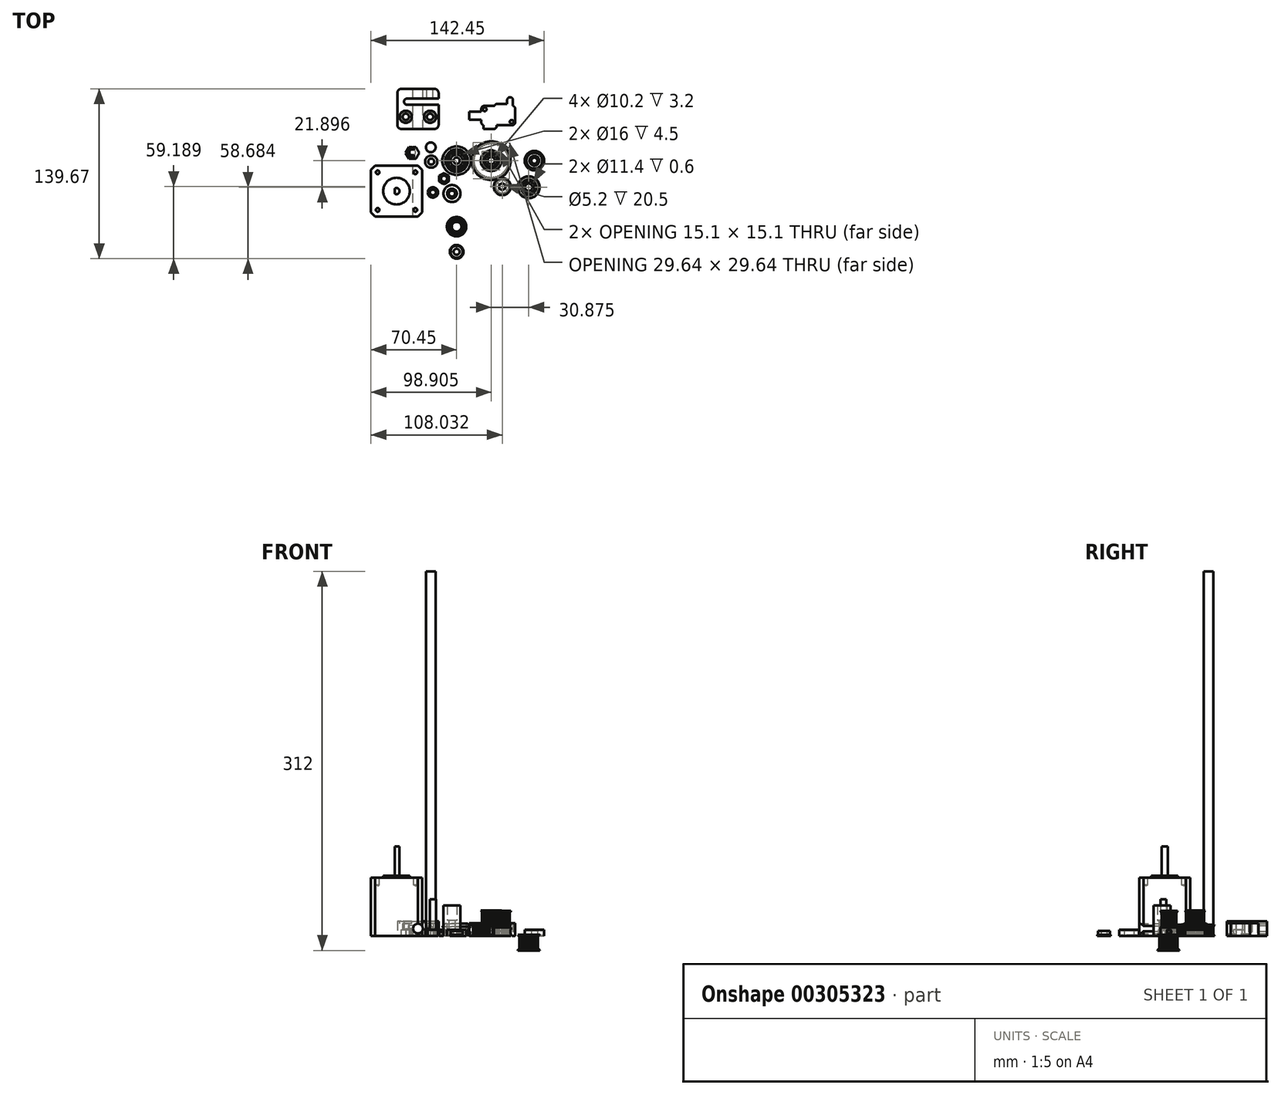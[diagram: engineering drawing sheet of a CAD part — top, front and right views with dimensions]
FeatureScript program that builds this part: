
annotation { "Feature Type Name" : "Feature", "Feature Type Description" : "" }
export const myFeature = defineFeature(function(context is Context, id is Id, definition is map)
    precondition{}
    {
        {
            var Q0;
            Q0=qCreatedBy(makeId("Front.planeOp"),FACE);
            var sketch = newSketch(context, id + "F0", { "sketchPlane" : qUnion([Q0])});
            skLineSegment(sketch, "E0", {"start": v(0, 0) * mm, "end": v(0, 10) * mm, "construction": true});
            skLineSegment(sketch, "E1", {"start": v(-9.25, 0) * mm, "end": v(-8, 0) * mm});
            skLineSegment(sketch, "E2", {"start": v(-8, 0) * mm, "end": v(-8, 10) * mm, "construction": true});
            skLineSegment(sketch, "E3", {"start": v(-8, 10) * mm, "end": v(-9.25, 10) * mm});
            skLineSegment(sketch, "E4", {"start": v(-8, 5) * mm, "end": v(-9.25, 5) * mm, "construction": true});
            skLineSegment(sketch, "E5", {"start": v(-9.25, 10) * mm, "end": v(-11.75, 7.5) * mm});
            skLineSegment(sketch, "E6", {"start": v(-11.75, 7.5) * mm, "end": v(-9.25, 5) * mm});
            skLineSegment(sketch, "E7", {"start": v(-9.25, 5) * mm, "end": v(-11.75, 2.5) * mm});
            skLineSegment(sketch, "E8", {"start": v(-11.75, 2.5) * mm, "end": v(-9.25, 0) * mm});
            skLineSegment(sketch, "E9.bottom", {"start": v(-8, 5.5) * mm, "end": v(-7, 5.5) * mm});
            skLineSegment(sketch, "E9.top", {"start": v(-8, 4.5) * mm, "end": v(-7, 4.5) * mm});
            skLineSegment(sketch, "E9.left", {"start": v(-8, 5.5) * mm, "end": v(-8, 4.5) * mm, "construction": true});
            skLineSegment(sketch, "E9.right", {"start": v(-7, 5.5) * mm, "end": v(-7, 4.5) * mm});
            skLineSegment(sketch, "E10", {"start": v(-8, 5.5) * mm, "end": v(-8, 10) * mm});
            skLineSegment(sketch, "E11", {"start": v(-8, 4.5) * mm, "end": v(-8, 0) * mm});
            skSolve(sketch);
        }
        {
            var Q0;
            Q0 = qSketchRegion(id + "F0", true);
            var Q1;
            Q1=sQuery(id+"F0.wireOp",EDGE,"E0");
            revolve(context, id + "F1", {"entities" : qUnion([Q0]), "axis" : qUnion([Q1]), "revolveType" : RevolveType.FULL});
        }
        {
            var Q0;
            Q0=qCreatedBy(makeId("Top.planeOp"),FACE);
            var sketch = newSketch(context, id + "F2", { "sketchPlane" : qUnion([Q0])});
            skCircle(sketch, "E12.cCircle", {"center": v(-36.35, 6.37) * mm, "radius": 4.9 * mm, "construction": true});
            skLineSegment(sketch, "E12.0", {"start": v(-33.52, 1.47) * mm, "end": v(-39.18, 1.47) * mm});
            skLineSegment(sketch, "E12.1", {"start": v(-39.18, 1.47) * mm, "end": v(-42.01, 6.37) * mm});
            skLineSegment(sketch, "E12.2", {"start": v(-42.01, 6.37) * mm, "end": v(-39.18, 11.27) * mm});
            skLineSegment(sketch, "E12.3", {"start": v(-39.18, 11.27) * mm, "end": v(-33.52, 11.27) * mm});
            skLineSegment(sketch, "E12.4", {"start": v(-33.52, 11.27) * mm, "end": v(-30.7, 6.37) * mm});
            skLineSegment(sketch, "E12.5", {"start": v(-30.7, 6.37) * mm, "end": v(-33.52, 1.47) * mm});
            skPoint(sketch, "E12.0.midPoint", {"position": v(-36.35, 1.47) * mm});
            skSolve(sketch);
        }
        {
            var Q0;
            Q0 = qSketchRegion(id + "F2", true);
            extrude(context, id + "F3", {"entities" : qUnion([Q0]), "depth" : 6 * mm});
        }
        {
            var Q0;
            Q0=makeQuery(id+"F3.opExtrude","CAP_FACE",FACE,{"disambiguationData":[OSD([sQuery(id+"F2.wireOp",EDGE,"E12.0"),sQuery(id+"F2.wireOp",EDGE,"E12.1"),sQuery(id+"F2.wireOp",EDGE,"E12.2"),sQuery(id+"F2.wireOp",EDGE,"E12.3"),sQuery(id+"F2.wireOp",EDGE,"E12.4"),sQuery(id+"F2.wireOp",EDGE,"E12.5")])],"isStart":false});
            var sketch = newSketch(context, id + "F4", { "sketchPlane" : qUnion([Q0])});
            skCircle(sketch, "E13", {"center": v(-36.35, 6.37) * mm, "radius": 3.5 * mm});
            skPoint(sketch, "E13.centerSnap0", {"position": v(-36.35, 11.27) * mm});
            skSolve(sketch);
        }
        {
            var Q0;
            Q0 = qSketchRegion(id + "F4", true);
            extrude(context, id + "F5", {"entities" : qUnion([Q0]), "operationType" : NewBodyOperationType.ADD, "depth" : 2.5 * mm});
        }
        {
            var Q0;
            Q0=makeQuery(id+"F5.opExtrude","CAP_FACE",FACE,{"disambiguationData":[OSD([sQuery(id+"F4.wireOp",EDGE,"E13")])],"isStart":false});
            var sketch = newSketch(context, id + "F6", { "sketchPlane" : qUnion([Q0])});
            skCircle(sketch, "E14", {"center": v(-36.35, 6.87) * mm, "radius": 2.5 * mm});
            skLineSegment(sketch, "E15", {"start": v(-37.24, 11.9) * mm, "end": v(-36.35, 10.37) * mm});
            skLineSegment(sketch, "E16", {"start": v(-36.35, 10.37) * mm, "end": v(-35.47, 11.9) * mm});
            skLineSegment(sketch, "E17", {"start": v(-35.47, 11.9) * mm, "end": v(-37.24, 11.9) * mm});
            skLineSegment(sketch, "E18", {"start": v(-36.35, 1.47) * mm, "end": v(-36.35, 6.87) * mm, "construction": true});
            skLineSegment(sketch, "E19", {"start": v(-36.35, 11.9) * mm, "end": v(-36.35, 10.37) * mm, "construction": true});
            skSolve(sketch);
        }
        {
            var Q0;
            Q0 = qSketchRegion(id + "F6", true);
            extrude(context, id + "F7", {"entities" : qUnion([Q0]), "operationType" : NewBodyOperationType.REMOVE, "endBound" : BoundingType.THROUGH_ALL, "oppositeDirection" : true, "depth" : 25 * mm});
        }
        {
            var Q0;
            Q0=makeQuery(id+"F7.boolean.opBoolean","COPY",EDGE,{"derivedFrom":makeQuery(id+"F7.opExtrude","SWEPT_EDGE",EDGE,{"disambiguationData":[OSD([sQuery(id+"F6.wireOp",EDGE,"E15"),sQuery(id+"F6.wireOp",EDGE,"E16")])]})});
            fillet(context, id + "F8", {"entities" : qUnion([Q0]), "radius" : 0.5 * mm, "tangentPropagation" : true, "allowEdgeOverflow" : false});
        }
        {
            var Q0;
            Q0=qCreatedBy(makeId("Top.planeOp"),FACE);
            var sketch = newSketch(context, id + "F9", { "sketchPlane" : qUnion([Q0])});
            skCircle(sketch, "E20", {"center": v(-20.9, -0.8) * mm, "radius": 5 * mm});
            skCircle(sketch, "E21", {"center": v(-20.9, -0.8) * mm, "radius": 2.5 * mm});
            skSolve(sketch);
        }
        {
            var Q0;
            Q0 = qSketchRegion(id + "F9", true);
            extrude(context, id + "F10", {"entities" : qUnion([Q0]), "depth" : 6 * mm});
        }
        {
            var Q0;
            Q0=qCreatedBy(makeId("Top.planeOp"),FACE);
            var sketch = newSketch(context, id + "F11", { "sketchPlane" : qUnion([Q0])});
            skLineSegment(sketch, "E22.bottom", {"start": v(-28.45, -4.05) * mm, "end": v(-70.45, -4.05) * mm});
            skLineSegment(sketch, "E22.top", {"start": v(-28.45, -46.05) * mm, "end": v(-70.45, -46.05) * mm});
            skLineSegment(sketch, "E22.left", {"start": v(-28.45, -4.05) * mm, "end": v(-28.45, -46.05) * mm});
            skLineSegment(sketch, "E22.right", {"start": v(-70.45, -4.05) * mm, "end": v(-70.45, -46.05) * mm});
            skSolve(sketch);
        }
        {
            var Q0;
            Q0 = qSketchRegion(id + "F11", true);
            extrude(context, id + "F12", {"entities" : qUnion([Q0]), "depth" : 48 * mm});
        }
        {
            var Q0;
            Q0=makeQuery(id+"F12.opExtrude","CAP_FACE",FACE,{"disambiguationData":[OSD([sQuery(id+"F11.wireOp",EDGE,"E22.bottom"),sQuery(id+"F11.wireOp",EDGE,"E22.top"),sQuery(id+"F11.wireOp",EDGE,"E22.left"),sQuery(id+"F11.wireOp",EDGE,"E22.right")])],"isStart":false});
            var sketch = newSketch(context, id + "F13", { "sketchPlane" : qUnion([Q0])});
            skCircle(sketch, "E23", {"center": v(-49.45, -25.05) * mm, "radius": 11 * mm});
            skPoint(sketch, "E23.centerSnap0", {"position": v(-49.45, -46.05) * mm});
            skLineSegment(sketch, "E24", {"start": v(-49.45, -4.05) * mm, "end": v(-49.45, -25.05) * mm, "construction": true});
            skLineSegment(sketch, "E25", {"start": v(-49.45, -25.05) * mm, "end": v(-28.45, -25.05) * mm, "construction": true});
            skSolve(sketch);
        }
        {
            var Q0;
            Q0 = qSketchRegion(id + "F13", true);
            extrude(context, id + "F14", {"entities" : qUnion([Q0]), "operationType" : NewBodyOperationType.ADD, "depth" : 1.5 * mm});
        }
        {
            var Q0;
            Q0=makeQuery(id+"F14.opExtrude","CAP_FACE",FACE,{"disambiguationData":[OSD([sQuery(id+"F13.wireOp",EDGE,"E23")])],"isStart":false});
            var sketch = newSketch(context, id + "F15", { "sketchPlane" : qUnion([Q0])});
            skArc(sketch, "E26", {"start": v(-50.95, -27.05) * mm, "mid": v(-46.95, -25.05) * mm, "end": v(-50.95, -23.05) * mm});
            skLineSegment(sketch, "E27", {"start": v(-50.95, -23.05) * mm, "end": v(-50.95, -27.05) * mm});
            skSolve(sketch);
        }
        {
            var Q0;
            Q0 = qSketchRegion(id + "F15", true);
            extrude(context, id + "F16", {"entities" : qUnion([Q0]), "operationType" : NewBodyOperationType.ADD, "depth" : 24 * mm});
        }
        {
            var Q0;
            Q0=makeQuery(id+"F12.opExtrude","SWEPT_EDGE",EDGE,{"disambiguationData":[OSD([sQuery(id+"F11.wireOp",EDGE,"E22.bottom"),sQuery(id+"F11.wireOp",EDGE,"E22.right")])]});
            var Q1;
            Q1=makeQuery(id+"F12.opExtrude","SWEPT_EDGE",EDGE,{"disambiguationData":[OSD([sQuery(id+"F11.wireOp",EDGE,"E22.top"),sQuery(id+"F11.wireOp",EDGE,"E22.right")])]});
            var Q2;
            Q2=makeQuery(id+"F12.opExtrude","SWEPT_EDGE",EDGE,{"disambiguationData":[OSD([sQuery(id+"F11.wireOp",EDGE,"E22.top"),sQuery(id+"F11.wireOp",EDGE,"E22.left")])]});
            var Q3;
            Q3=makeQuery(id+"F12.opExtrude","SWEPT_EDGE",EDGE,{"disambiguationData":[OSD([sQuery(id+"F11.wireOp",EDGE,"E22.bottom"),sQuery(id+"F11.wireOp",EDGE,"E22.left")])]});
            chamfer(context, id + "F17", {"entities" : qUnion([Q0, Q1, Q2, Q3]), "width" : 3.5 * mm, "tangentPropagation" : true});
        }
        {
            var Q0;
            Q0=makeQuery(id+"F12.opExtrude","CAP_FACE",FACE,{"disambiguationData":[OSD([sQuery(id+"F11.wireOp",EDGE,"E22.bottom"),sQuery(id+"F11.wireOp",EDGE,"E22.top"),sQuery(id+"F11.wireOp",EDGE,"E22.left"),sQuery(id+"F11.wireOp",EDGE,"E22.right")])],"isStart":false});
            var sketch = newSketch(context, id + "F18", { "sketchPlane" : qUnion([Q0])});
            skPoint(sketch, "E28", {"position": v(-64.95, -9.55) * mm});
            skPoint(sketch, "E29", {"position": v(-33.95, -9.55) * mm});
            skPoint(sketch, "E30", {"position": v(-33.95, -40.55) * mm});
            skPoint(sketch, "E31", {"position": v(-64.95, -40.55) * mm});
            skSolve(sketch);
        }
        {
            var Q0;
            Q0=sQuery(id+"F18.wireOp",VERTEX,"E28");
            var Q1;
            Q1=sQuery(id+"F18.wireOp",VERTEX,"E29");
            var Q2;
            Q2=sQuery(id+"F18.wireOp",VERTEX,"E30");
            var Q3;
            Q3=sQuery(id+"F18.wireOp",VERTEX,"E31");
            var Q4;
            Q4=makeQuery(id+"F12.opExtrude","SWEPT_BODY",BODY,{"disambiguationData":[OSD([sQuery(id+"F11.wireOp",EDGE,"E22.bottom"),sQuery(id+"F11.wireOp",EDGE,"E22.top"),sQuery(id+"F11.wireOp",EDGE,"E22.left"),sQuery(id+"F11.wireOp",EDGE,"E22.right")])]});
            hole(context, id + "F19", {"style" : HoleStyle.SIMPLE, "endStyle" : HoleEndStyle.BLIND, "holeDiameter" : 3 * mm, "holeDepth" : 6 * mm, "tappedDepth" : 12 * mm, "tapClearance" : 3, "startFromSketch" : true, "locations" : qUnion([Q0, Q1, Q2, Q3]), "scope" : qUnion([Q4])});
        }
        {
            var Q0;
            Q0=qCreatedBy(makeId("Top.planeOp"),FACE);
            var sketch = newSketch(context, id + "F20", { "sketchPlane" : qUnion([Q0])});
            skCircle(sketch, "E32", {"center": v(-3.83, -27.08) * mm, "radius": 2.5 * mm});
            skCircle(sketch, "E33", {"center": v(-3.83, -27.08) * mm, "radius": 7 * mm});
            skSolve(sketch);
        }
        {
            var Q0;
            Q0 = qSketchRegion(id + "F20", true);
            extrude(context, id + "F21", {"entities" : qUnion([Q0]), "depth" : 12.5 * mm});
        }
        {
            var Q0;
            Q0=makeQuery(id+"F21.opExtrude","CAP_FACE",FACE,{"disambiguationData":[OSD([sQuery(id+"F20.wireOp",EDGE,"E32"),sQuery(id+"F20.wireOp",EDGE,"E33")])],"isStart":false});
            var sketch = newSketch(context, id + "F22", { "sketchPlane" : qUnion([Q0])});
            skCircle(sketch, "E34", {"center": v(-3.83, -27.08) * mm, "radius": 4 * mm});
            skCircle(sketch, "E35.0", {"center": v(-3.83, -27.08) * mm, "radius": 7 * mm});
            skSolve(sketch);
        }
        {
            var Q0;
            Q0 = qSketchRegion(id + "F22", true);
            extrude(context, id + "F23", {"entities" : qUnion([Q0]), "operationType" : NewBodyOperationType.ADD, "depth" : 12.5 * mm});
        }
        {
            var Q0;
            Q0=qCreatedBy(makeId("Top.planeOp"),FACE);
            var sketch = newSketch(context, id + "F24", { "sketchPlane" : qUnion([Q0])});
            skCircle(sketch, "E36", {"center": v(-21.25, 10.98) * mm, "radius": 4 * mm});
            skSolve(sketch);
        }
        {
            var Q0;
            Q0 = qSketchRegion(id + "F24", true);
            extrude(context, id + "F25", {"entities" : qUnion([Q0]), "depth" : 300 * mm});
        }
        {
            var Q0;
            Q0=qCreatedBy(makeId("Top.planeOp"),FACE);
            var sketch = newSketch(context, id + "F26", { "sketchPlane" : qUnion([Q0])});
            skCircle(sketch, "E37", {"center": v(37.58, -21.4) * mm, "radius": 2.6 * mm});
            skCircle(sketch, "E38", {"center": v(37.58, -21.4) * mm, "radius": 7 * mm});
            skLineSegment(sketch, "E39.bottom", {"start": v(32.18, -18.5) * mm, "end": v(34.48, -18.5) * mm});
            skLineSegment(sketch, "E39.top", {"start": v(32.18, -24.3) * mm, "end": v(34.48, -24.3) * mm});
            skLineSegment(sketch, "E39.left", {"start": v(32.18, -18.5) * mm, "end": v(32.18, -24.3) * mm});
            skLineSegment(sketch, "E39.right", {"start": v(34.48, -18.5) * mm, "end": v(34.48, -24.3) * mm});
            skLineSegment(sketch, "E40", {"start": v(32.18, -21.4) * mm, "end": v(37.58, -21.4) * mm, "construction": true});
            skLineSegment(sketch, "E41", {"start": v(37.58, -21.4) * mm, "end": v(37.58, -14.4) * mm, "construction": true});
            skLineSegment(sketch, "E42.MirrorCS", {"start": v(40.68, -18.5) * mm, "end": v(40.68, -24.3) * mm});
            skLineSegment(sketch, "E43.MirrorCS", {"start": v(42.98, -18.5) * mm, "end": v(40.68, -18.5) * mm});
            skLineSegment(sketch, "E44.MirrorCS", {"start": v(42.98, -18.5) * mm, "end": v(42.98, -24.3) * mm});
            skLineSegment(sketch, "E45.MirrorCS", {"start": v(42.98, -24.3) * mm, "end": v(40.68, -24.3) * mm});
            skSolve(sketch);
        }
        {
            var Q0;
            Q0 = qSketchRegion(id + "F26", true);
            extrude(context, id + "F27", {"entities" : qUnion([Q0]), "depth" : 7 * mm});
        }
        {
            var Q0;
            Q0=makeQuery(id+"F27.opExtrude","CAP_FACE",FACE,{"disambiguationData":[OSD([sQuery(id+"F26.wireOp",EDGE,"E37"),sQuery(id+"F26.wireOp",EDGE,"E38"),sQuery(id+"F26.wireOp",EDGE,"E39.bottom"),sQuery(id+"F26.wireOp",EDGE,"E39.top"),sQuery(id+"F26.wireOp",EDGE,"E39.left"),sQuery(id+"F26.wireOp",EDGE,"E39.right"),sQuery(id+"F26.wireOp",EDGE,"E42.MirrorCS"),sQuery(id+"F26.wireOp",EDGE,"E43.MirrorCS"),sQuery(id+"F26.wireOp",EDGE,"E44.MirrorCS"),sQuery(id+"F26.wireOp",EDGE,"E45.MirrorCS")])],"isStart":false});
            var sketch = newSketch(context, id + "F28", { "sketchPlane" : qUnion([Q0])});
            skCircle(sketch, "E46.0", {"center": v(37.58, -21.4) * mm, "radius": 2.6 * mm});
            skCircle(sketch, "E47.0", {"center": v(37.58, -21.4) * mm, "radius": 7 * mm});
            skSolve(sketch);
        }
        {
            var Q0;
            Q0 = qSketchRegion(id + "F28", true);
            extrude(context, id + "F29", {"entities" : qUnion([Q0]), "operationType" : NewBodyOperationType.ADD, "depth" : 1 * mm});
        }
        {
            var Q0;
            Q0=makeQuery(id+"F29.opExtrude","CAP_FACE",FACE,{"disambiguationData":[OSD([sQuery(id+"F28.wireOp",EDGE,"E46.0"),sQuery(id+"F28.wireOp",EDGE,"E47.0")])],"isStart":false});
            var sketch = newSketch(context, id + "F30", { "sketchPlane" : qUnion([Q0])});
            skCircle(sketch, "E48.0", {"center": v(37.58, -21.4) * mm, "radius": 2.6 * mm});
            skCircle(sketch, "E49", {"center": v(37.58, -21.4) * mm, "radius": 6.1 * mm, "construction": true});
            skCircle(sketch, "E50.0", {"center": v(37.58, -21.4) * mm, "radius": 5.2 * mm, "construction": true});
            skLineSegment(sketch, "E51", {"start": v(37.58, -21.4) * mm, "end": v(37.58, -15.3) * mm, "construction": true});
            skLineSegment(sketch, "E52", {"start": v(36.98, -16.23) * mm, "end": v(38.18, -16.23) * mm});
            skLineSegment(sketch, "E53", {"start": v(36.98, -16.23) * mm, "end": v(36.67, -15.36) * mm});
            skLineSegment(sketch, "E54.MirrorCS", {"start": v(38.18, -16.23) * mm, "end": v(38.5, -15.36) * mm});
            skLineSegment(sketch, "E55.1.0", {"start": v(35.05, -16.85) * mm, "end": v(34.43, -16.17) * mm});
            skLineSegment(sketch, "E55.1.1", {"start": v(35.05, -16.85) * mm, "end": v(36.16, -16.39) * mm});
            skLineSegment(sketch, "E55.1.2", {"start": v(36.16, -16.39) * mm, "end": v(36.12, -15.47) * mm});
            skLineSegment(sketch, "E55.2.0", {"start": v(33.5, -18.16) * mm, "end": v(32.67, -17.77) * mm});
            skLineSegment(sketch, "E55.2.1", {"start": v(33.5, -18.16) * mm, "end": v(34.35, -17.31) * mm});
            skLineSegment(sketch, "E55.2.2", {"start": v(34.35, -17.31) * mm, "end": v(33.96, -16.48) * mm});
            skLineSegment(sketch, "E55.3.0", {"start": v(32.58, -19.97) * mm, "end": v(31.66, -19.93) * mm});
            skLineSegment(sketch, "E55.3.1", {"start": v(32.58, -19.97) * mm, "end": v(33.04, -18.86) * mm});
            skLineSegment(sketch, "E55.3.2", {"start": v(33.04, -18.86) * mm, "end": v(32.36, -18.24) * mm});
            skLineSegment(sketch, "E55.4.0", {"start": v(32.42, -22) * mm, "end": v(31.55, -22.3) * mm});
            skLineSegment(sketch, "E55.4.1", {"start": v(32.42, -22) * mm, "end": v(32.42, -20.8) * mm});
            skLineSegment(sketch, "E55.4.2", {"start": v(32.42, -20.8) * mm, "end": v(31.55, -20.48) * mm});
            skLineSegment(sketch, "E55.5.0", {"start": v(33.04, -23.92) * mm, "end": v(32.36, -24.54) * mm});
            skLineSegment(sketch, "E55.5.1", {"start": v(33.04, -23.92) * mm, "end": v(32.58, -22.81) * mm});
            skLineSegment(sketch, "E55.5.2", {"start": v(32.58, -22.81) * mm, "end": v(31.66, -22.85) * mm});
            skLineSegment(sketch, "E55.6.0", {"start": v(34.35, -25.47) * mm, "end": v(33.96, -26.3) * mm});
            skLineSegment(sketch, "E55.6.1", {"start": v(34.35, -25.47) * mm, "end": v(33.5, -24.62) * mm});
            skLineSegment(sketch, "E55.6.2", {"start": v(33.5, -24.62) * mm, "end": v(32.67, -25) * mm});
            skLineSegment(sketch, "E55.7.0", {"start": v(36.16, -26.4) * mm, "end": v(36.12, -27.31) * mm});
            skLineSegment(sketch, "E55.7.1", {"start": v(36.16, -26.4) * mm, "end": v(35.05, -25.93) * mm});
            skLineSegment(sketch, "E55.7.2", {"start": v(35.05, -25.93) * mm, "end": v(34.43, -26.61) * mm});
            skLineSegment(sketch, "E55.8.0", {"start": v(38.18, -26.56) * mm, "end": v(38.5, -27.42) * mm});
            skLineSegment(sketch, "E55.8.1", {"start": v(38.18, -26.56) * mm, "end": v(36.98, -26.56) * mm});
            skLineSegment(sketch, "E55.8.2", {"start": v(36.98, -26.56) * mm, "end": v(36.67, -27.42) * mm});
            skLineSegment(sketch, "E55.9.0", {"start": v(40.11, -25.93) * mm, "end": v(40.74, -26.61) * mm});
            skLineSegment(sketch, "E55.9.1", {"start": v(40.11, -25.93) * mm, "end": v(39, -26.4) * mm});
            skLineSegment(sketch, "E55.9.2", {"start": v(39, -26.4) * mm, "end": v(39.04, -27.31) * mm});
            skLineSegment(sketch, "E55.10.0", {"start": v(41.66, -24.62) * mm, "end": v(42.5, -25) * mm});
            skLineSegment(sketch, "E55.10.1", {"start": v(41.66, -24.62) * mm, "end": v(40.8, -25.47) * mm});
            skLineSegment(sketch, "E55.10.2", {"start": v(40.8, -25.47) * mm, "end": v(41.2, -26.3) * mm});
            skLineSegment(sketch, "E55.11.0", {"start": v(42.58, -22.81) * mm, "end": v(43.5, -22.85) * mm});
            skLineSegment(sketch, "E55.11.1", {"start": v(42.58, -22.81) * mm, "end": v(42.12, -23.92) * mm});
            skLineSegment(sketch, "E55.11.2", {"start": v(42.12, -23.92) * mm, "end": v(42.8, -24.54) * mm});
            skLineSegment(sketch, "E55.12.0", {"start": v(42.75, -20.8) * mm, "end": v(43.61, -20.48) * mm});
            skLineSegment(sketch, "E55.12.1", {"start": v(42.75, -20.8) * mm, "end": v(42.75, -22) * mm});
            skLineSegment(sketch, "E55.12.2", {"start": v(42.75, -22) * mm, "end": v(43.61, -22.3) * mm});
            skLineSegment(sketch, "E55.13.0", {"start": v(42.12, -18.86) * mm, "end": v(42.8, -18.24) * mm});
            skLineSegment(sketch, "E55.13.1", {"start": v(42.12, -18.86) * mm, "end": v(42.58, -19.97) * mm});
            skLineSegment(sketch, "E55.13.2", {"start": v(42.58, -19.97) * mm, "end": v(43.5, -19.93) * mm});
            skLineSegment(sketch, "E55.14.0", {"start": v(40.8, -17.31) * mm, "end": v(41.2, -16.48) * mm});
            skLineSegment(sketch, "E55.14.1", {"start": v(40.8, -17.31) * mm, "end": v(41.66, -18.16) * mm});
            skLineSegment(sketch, "E55.14.2", {"start": v(41.66, -18.16) * mm, "end": v(42.5, -17.77) * mm});
            skLineSegment(sketch, "E55.15.0", {"start": v(39, -16.39) * mm, "end": v(39.04, -15.47) * mm});
            skLineSegment(sketch, "E55.15.1", {"start": v(39, -16.39) * mm, "end": v(40.11, -16.85) * mm});
            skLineSegment(sketch, "E55.15.2", {"start": v(40.11, -16.85) * mm, "end": v(40.74, -16.17) * mm});
            skPoint(sketch, "E56.1.0", {"position": v(-0.27, 43.24) * mm});
            skPoint(sketch, "E56.2.0", {"position": v(-37.32, -21.85) * mm});
            skPoint(sketch, "E56.center", {"position": v(0, 0) * mm});
            skArc(sketch, "E57", {"start": v(38.5, -15.36) * mm, "mid": v(38.77, -15.4) * mm, "end": v(39.04, -15.47) * mm});
            skCircle(sketch, "E58.1.0", {"center": v(-0.27, 43.24) * mm, "radius": 6.1 * mm, "construction": true});
            skCircle(sketch, "E58.2.0", {"center": v(-37.32, -21.85) * mm, "radius": 6.1 * mm, "construction": true});
            skArc(sketch, "E59.1.0", {"start": v(36.12, -15.47) * mm, "mid": v(36.4, -15.4) * mm, "end": v(36.67, -15.36) * mm});
            skArc(sketch, "E59.2.0", {"start": v(33.96, -16.48) * mm, "mid": v(34.2, -16.32) * mm, "end": v(34.43, -16.17) * mm});
            skArc(sketch, "E59.3.0", {"start": v(32.36, -18.24) * mm, "mid": v(32.5, -18) * mm, "end": v(32.67, -17.77) * mm});
            skArc(sketch, "E59.4.0", {"start": v(31.55, -20.48) * mm, "mid": v(31.6, -20.2) * mm, "end": v(31.66, -19.93) * mm});
            skArc(sketch, "E59.5.0", {"start": v(31.66, -22.85) * mm, "mid": v(31.6, -22.58) * mm, "end": v(31.55, -22.3) * mm});
            skArc(sketch, "E59.6.0", {"start": v(32.67, -25) * mm, "mid": v(32.5, -24.78) * mm, "end": v(32.36, -24.54) * mm});
            skArc(sketch, "E59.7.0", {"start": v(34.43, -26.61) * mm, "mid": v(34.2, -26.46) * mm, "end": v(33.96, -26.3) * mm});
            skArc(sketch, "E59.8.0", {"start": v(36.67, -27.42) * mm, "mid": v(36.4, -27.37) * mm, "end": v(36.12, -27.31) * mm});
            skArc(sketch, "E59.9.0", {"start": v(39.04, -27.31) * mm, "mid": v(38.77, -27.37) * mm, "end": v(38.5, -27.42) * mm});
            skArc(sketch, "E59.10.0", {"start": v(41.2, -26.3) * mm, "mid": v(40.97, -26.46) * mm, "end": v(40.74, -26.61) * mm});
            skArc(sketch, "E59.11.0", {"start": v(42.8, -24.54) * mm, "mid": v(42.65, -24.78) * mm, "end": v(42.5, -25) * mm});
            skArc(sketch, "E59.12.0", {"start": v(43.61, -22.3) * mm, "mid": v(43.56, -22.58) * mm, "end": v(43.5, -22.85) * mm});
            skArc(sketch, "E59.13.0", {"start": v(43.5, -19.93) * mm, "mid": v(43.56, -20.2) * mm, "end": v(43.61, -20.48) * mm});
            skArc(sketch, "E59.14.0", {"start": v(42.5, -17.77) * mm, "mid": v(42.65, -18) * mm, "end": v(42.8, -18.24) * mm});
            skArc(sketch, "E59.15.0", {"start": v(40.74, -16.17) * mm, "mid": v(40.97, -16.32) * mm, "end": v(41.2, -16.48) * mm});
            skSolve(sketch);
        }
        {
            var Q0;
            Q0 = qSketchRegion(id + "F30", true);
            extrude(context, id + "F31", {"entities" : qUnion([Q0]), "operationType" : NewBodyOperationType.ADD, "depth" : 11 * mm});
        }
        {
            var Q0;
            Q0=makeQuery(id+"F31.opExtrude","CAP_FACE",FACE,{"disambiguationData":[OSD([sQuery(id+"F30.wireOp",EDGE,"E48.0"),sQuery(id+"F30.wireOp",EDGE,"E52"),sQuery(id+"F30.wireOp",EDGE,"E53"),sQuery(id+"F30.wireOp",EDGE,"E54.MirrorCS"),sQuery(id+"F30.wireOp",EDGE,"E55.1.0"),sQuery(id+"F30.wireOp",EDGE,"E55.1.1"),sQuery(id+"F30.wireOp",EDGE,"E55.1.2"),sQuery(id+"F30.wireOp",EDGE,"E55.2.0"),sQuery(id+"F30.wireOp",EDGE,"E55.2.1"),sQuery(id+"F30.wireOp",EDGE,"E55.2.2"),sQuery(id+"F30.wireOp",EDGE,"E55.3.0"),sQuery(id+"F30.wireOp",EDGE,"E55.3.1"),sQuery(id+"F30.wireOp",EDGE,"E55.3.2"),sQuery(id+"F30.wireOp",EDGE,"E55.4.0"),sQuery(id+"F30.wireOp",EDGE,"E55.4.1"),sQuery(id+"F30.wireOp",EDGE,"E55.4.2"),sQuery(id+"F30.wireOp",EDGE,"E55.5.0"),sQuery(id+"F30.wireOp",EDGE,"E55.5.1"),sQuery(id+"F30.wireOp",EDGE,"E55.5.2"),sQuery(id+"F30.wireOp",EDGE,"E55.6.0"),sQuery(id+"F30.wireOp",EDGE,"E55.6.1"),sQuery(id+"F30.wireOp",EDGE,"E55.6.2"),sQuery(id+"F30.wireOp",EDGE,"E55.7.0"),sQuery(id+"F30.wireOp",EDGE,"E55.7.1"),sQuery(id+"F30.wireOp",EDGE,"E55.7.2"),sQuery(id+"F30.wireOp",EDGE,"E55.8.0"),sQuery(id+"F30.wireOp",EDGE,"E55.8.1"),sQuery(id+"F30.wireOp",EDGE,"E55.8.2"),sQuery(id+"F30.wireOp",EDGE,"E55.9.0"),sQuery(id+"F30.wireOp",EDGE,"E55.9.1"),sQuery(id+"F30.wireOp",EDGE,"E55.9.2"),sQuery(id+"F30.wireOp",EDGE,"E55.10.0"),sQuery(id+"F30.wireOp",EDGE,"E55.10.1"),sQuery(id+"F30.wireOp",EDGE,"E55.10.2"),sQuery(id+"F30.wireOp",EDGE,"E55.11.0"),sQuery(id+"F30.wireOp",EDGE,"E55.11.1"),sQuery(id+"F30.wireOp",EDGE,"E55.11.2"),sQuery(id+"F30.wireOp",EDGE,"E55.12.0"),sQuery(id+"F30.wireOp",EDGE,"E55.12.1"),sQuery(id+"F30.wireOp",EDGE,"E55.12.2"),sQuery(id+"F30.wireOp",EDGE,"E55.13.0"),sQuery(id+"F30.wireOp",EDGE,"E55.13.1"),sQuery(id+"F30.wireOp",EDGE,"E55.13.2"),sQuery(id+"F30.wireOp",EDGE,"E55.14.0"),sQuery(id+"F30.wireOp",EDGE,"E55.14.1"),sQuery(id+"F30.wireOp",EDGE,"E55.14.2"),sQuery(id+"F30.wireOp",EDGE,"E55.15.0"),sQuery(id+"F30.wireOp",EDGE,"E55.15.1"),sQuery(id+"F30.wireOp",EDGE,"E55.15.2"),sQuery(id+"F30.wireOp",EDGE,"E57"),sQuery(id+"F30.wireOp",EDGE,"E59.1.0"),sQuery(id+"F30.wireOp",EDGE,"E59.2.0"),sQuery(id+"F30.wireOp",EDGE,"E59.3.0"),sQuery(id+"F30.wireOp",EDGE,"E59.4.0"),sQuery(id+"F30.wireOp",EDGE,"E59.5.0"),sQuery(id+"F30.wireOp",EDGE,"E59.6.0"),sQuery(id+"F30.wireOp",EDGE,"E59.7.0"),sQuery(id+"F30.wireOp",EDGE,"E59.8.0"),sQuery(id+"F30.wireOp",EDGE,"E59.9.0"),sQuery(id+"F30.wireOp",EDGE,"E59.10.0"),sQuery(id+"F30.wireOp",EDGE,"E59.11.0"),sQuery(id+"F30.wireOp",EDGE,"E59.12.0"),sQuery(id+"F30.wireOp",EDGE,"E59.13.0"),sQuery(id+"F30.wireOp",EDGE,"E59.14.0"),sQuery(id+"F30.wireOp",EDGE,"E59.15.0")])],"isStart":false});
            var sketch = newSketch(context, id + "F32", { "sketchPlane" : qUnion([Q0])});
            skCircle(sketch, "E60.0", {"center": v(37.58, -21.4) * mm, "radius": 2.6 * mm});
            skCircle(sketch, "E61.0", {"center": v(37.58, -21.4) * mm, "radius": 7 * mm});
            skSolve(sketch);
        }
        {
            var Q0;
            Q0 = qSketchRegion(id + "F32", true);
            extrude(context, id + "F33", {"entities" : qUnion([Q0]), "operationType" : NewBodyOperationType.ADD, "depth" : 1.5 * mm});
        }
        {
            var Q0;
            Q0=makeQuery(id+"F33.opExtrude","CAP_EDGE",EDGE,{"disambiguationData":[OSD([sQuery(id+"F32.wireOp",EDGE,"E61.0")])],"isStart":true});
            var Q1;
            Q1=makeQuery(id+"F29.opExtrude","CAP_EDGE",EDGE,{"disambiguationData":[OSD([sQuery(id+"F28.wireOp",EDGE,"E47.0")])],"isStart":false});
            chamfer(context, id + "F34", {"entities" : qUnion([Q0, Q1]), "width" : 1 * mm, "tangentPropagation" : true});
        }
        {
            var Q0;
            Q0=makeQuery(id+"F31.opExtrude","SWEPT_EDGE",EDGE,{"disambiguationData":[OSD([sQuery(id+"F30.wireOp",EDGE,"E55.9.2"),sQuery(id+"F30.wireOp",EDGE,"E59.9.0")])]});
            var Q1;
            Q1=makeQuery(id+"F31.opExtrude","SWEPT_EDGE",EDGE,{"disambiguationData":[OSD([sQuery(id+"F30.wireOp",EDGE,"E55.9.0"),sQuery(id+"F30.wireOp",EDGE,"E59.10.0")])]});
            var Q2;
            Q2=makeQuery(id+"F31.opExtrude","SWEPT_EDGE",EDGE,{"disambiguationData":[OSD([sQuery(id+"F30.wireOp",EDGE,"E55.8.0"),sQuery(id+"F30.wireOp",EDGE,"E59.9.0")])]});
            var Q3;
            Q3=makeQuery(id+"F31.opExtrude","SWEPT_EDGE",EDGE,{"disambiguationData":[OSD([sQuery(id+"F30.wireOp",EDGE,"E55.8.2"),sQuery(id+"F30.wireOp",EDGE,"E59.8.0")])]});
            var Q4;
            Q4=makeQuery(id+"F31.opExtrude","SWEPT_EDGE",EDGE,{"disambiguationData":[OSD([sQuery(id+"F30.wireOp",EDGE,"E55.7.0"),sQuery(id+"F30.wireOp",EDGE,"E59.8.0")])]});
            var Q5;
            Q5=makeQuery(id+"F31.opExtrude","SWEPT_EDGE",EDGE,{"disambiguationData":[OSD([sQuery(id+"F30.wireOp",EDGE,"E55.7.2"),sQuery(id+"F30.wireOp",EDGE,"E59.7.0")])]});
            var Q6;
            Q6=makeQuery(id+"F31.opExtrude","SWEPT_EDGE",EDGE,{"disambiguationData":[OSD([sQuery(id+"F30.wireOp",EDGE,"E55.6.0"),sQuery(id+"F30.wireOp",EDGE,"E59.7.0")])]});
            var Q7;
            Q7=makeQuery(id+"F31.opExtrude","SWEPT_EDGE",EDGE,{"disambiguationData":[OSD([sQuery(id+"F30.wireOp",EDGE,"E55.6.2"),sQuery(id+"F30.wireOp",EDGE,"E59.6.0")])]});
            var Q8;
            Q8=makeQuery(id+"F31.opExtrude","SWEPT_EDGE",EDGE,{"disambiguationData":[OSD([sQuery(id+"F30.wireOp",EDGE,"E55.10.2"),sQuery(id+"F30.wireOp",EDGE,"E59.10.0")])]});
            var Q9;
            Q9=makeQuery(id+"F31.opExtrude","SWEPT_EDGE",EDGE,{"disambiguationData":[OSD([sQuery(id+"F30.wireOp",EDGE,"E55.10.0"),sQuery(id+"F30.wireOp",EDGE,"E59.11.0")])]});
            var Q10;
            Q10=makeQuery(id+"F31.opExtrude","SWEPT_EDGE",EDGE,{"disambiguationData":[OSD([sQuery(id+"F30.wireOp",EDGE,"E55.11.2"),sQuery(id+"F30.wireOp",EDGE,"E59.11.0")])]});
            var Q11;
            Q11=makeQuery(id+"F31.opExtrude","SWEPT_EDGE",EDGE,{"disambiguationData":[OSD([sQuery(id+"F30.wireOp",EDGE,"E55.11.0"),sQuery(id+"F30.wireOp",EDGE,"E59.12.0")])]});
            var Q12;
            Q12=makeQuery(id+"F31.opExtrude","SWEPT_EDGE",EDGE,{"disambiguationData":[OSD([sQuery(id+"F30.wireOp",EDGE,"E55.12.2"),sQuery(id+"F30.wireOp",EDGE,"E59.12.0")])]});
            var Q13;
            Q13=makeQuery(id+"F31.opExtrude","SWEPT_EDGE",EDGE,{"disambiguationData":[OSD([sQuery(id+"F30.wireOp",EDGE,"E55.12.0"),sQuery(id+"F30.wireOp",EDGE,"E59.13.0")])]});
            var Q14;
            Q14=makeQuery(id+"F31.opExtrude","SWEPT_EDGE",EDGE,{"disambiguationData":[OSD([sQuery(id+"F30.wireOp",EDGE,"E55.13.2"),sQuery(id+"F30.wireOp",EDGE,"E59.13.0")])]});
            var Q15;
            Q15=makeQuery(id+"F31.opExtrude","SWEPT_EDGE",EDGE,{"disambiguationData":[OSD([sQuery(id+"F30.wireOp",EDGE,"E55.13.0"),sQuery(id+"F30.wireOp",EDGE,"E59.14.0")])]});
            var Q16;
            Q16=makeQuery(id+"F31.opExtrude","SWEPT_EDGE",EDGE,{"disambiguationData":[OSD([sQuery(id+"F30.wireOp",EDGE,"E55.14.2"),sQuery(id+"F30.wireOp",EDGE,"E59.14.0")])]});
            var Q17;
            Q17=makeQuery(id+"F31.opExtrude","SWEPT_EDGE",EDGE,{"disambiguationData":[OSD([sQuery(id+"F30.wireOp",EDGE,"E55.14.0"),sQuery(id+"F30.wireOp",EDGE,"E59.15.0")])]});
            var Q18;
            Q18=makeQuery(id+"F31.opExtrude","SWEPT_EDGE",EDGE,{"disambiguationData":[OSD([sQuery(id+"F30.wireOp",EDGE,"E55.15.2"),sQuery(id+"F30.wireOp",EDGE,"E59.15.0")])]});
            var Q19;
            Q19=makeQuery(id+"F31.opExtrude","SWEPT_EDGE",EDGE,{"disambiguationData":[OSD([sQuery(id+"F30.wireOp",EDGE,"E55.15.0"),sQuery(id+"F30.wireOp",EDGE,"E57")])]});
            var Q20;
            Q20=makeQuery(id+"F31.opExtrude","SWEPT_EDGE",EDGE,{"disambiguationData":[OSD([sQuery(id+"F30.wireOp",EDGE,"E54.MirrorCS"),sQuery(id+"F30.wireOp",EDGE,"E57")])]});
            var Q21;
            Q21=makeQuery(id+"F31.opExtrude","SWEPT_EDGE",EDGE,{"disambiguationData":[OSD([sQuery(id+"F30.wireOp",EDGE,"E53"),sQuery(id+"F30.wireOp",EDGE,"E59.1.0")])]});
            var Q22;
            Q22=makeQuery(id+"F31.opExtrude","SWEPT_EDGE",EDGE,{"disambiguationData":[OSD([sQuery(id+"F30.wireOp",EDGE,"E55.1.2"),sQuery(id+"F30.wireOp",EDGE,"E59.1.0")])]});
            var Q23;
            Q23=makeQuery(id+"F31.opExtrude","SWEPT_EDGE",EDGE,{"disambiguationData":[OSD([sQuery(id+"F30.wireOp",EDGE,"E55.1.0"),sQuery(id+"F30.wireOp",EDGE,"E59.2.0")])]});
            var Q24;
            Q24=makeQuery(id+"F31.opExtrude","SWEPT_EDGE",EDGE,{"disambiguationData":[OSD([sQuery(id+"F30.wireOp",EDGE,"E55.2.2"),sQuery(id+"F30.wireOp",EDGE,"E59.2.0")])]});
            var Q25;
            Q25=makeQuery(id+"F31.opExtrude","SWEPT_EDGE",EDGE,{"disambiguationData":[OSD([sQuery(id+"F30.wireOp",EDGE,"E55.2.0"),sQuery(id+"F30.wireOp",EDGE,"E59.3.0")])]});
            var Q26;
            Q26=makeQuery(id+"F31.opExtrude","SWEPT_EDGE",EDGE,{"disambiguationData":[OSD([sQuery(id+"F30.wireOp",EDGE,"E55.3.2"),sQuery(id+"F30.wireOp",EDGE,"E59.3.0")])]});
            var Q27;
            Q27=makeQuery(id+"F31.opExtrude","SWEPT_EDGE",EDGE,{"disambiguationData":[OSD([sQuery(id+"F30.wireOp",EDGE,"E55.3.0"),sQuery(id+"F30.wireOp",EDGE,"E59.4.0")])]});
            var Q28;
            Q28=makeQuery(id+"F31.opExtrude","SWEPT_EDGE",EDGE,{"disambiguationData":[OSD([sQuery(id+"F30.wireOp",EDGE,"E55.4.2"),sQuery(id+"F30.wireOp",EDGE,"E59.4.0")])]});
            var Q29;
            Q29=makeQuery(id+"F31.opExtrude","SWEPT_EDGE",EDGE,{"disambiguationData":[OSD([sQuery(id+"F30.wireOp",EDGE,"E55.4.0"),sQuery(id+"F30.wireOp",EDGE,"E59.5.0")])]});
            var Q30;
            Q30=makeQuery(id+"F31.opExtrude","SWEPT_EDGE",EDGE,{"disambiguationData":[OSD([sQuery(id+"F30.wireOp",EDGE,"E55.5.2"),sQuery(id+"F30.wireOp",EDGE,"E59.5.0")])]});
            var Q31;
            Q31=makeQuery(id+"F31.opExtrude","SWEPT_EDGE",EDGE,{"disambiguationData":[OSD([sQuery(id+"F30.wireOp",EDGE,"E55.5.0"),sQuery(id+"F30.wireOp",EDGE,"E59.6.0")])]});
            fillet(context, id + "F35", {"entities" : qUnion([Q0, Q1, Q2, Q3, Q4, Q5, Q6, Q7, Q8, Q9, Q10, Q11, Q12, Q13, Q14, Q15, Q16, Q17, Q18, Q19, Q20, Q21, Q22, Q23, Q24, Q25, Q26, Q27, Q28, Q29, Q30, Q31]), "radius" : 0.2 * mm, "tangentPropagation" : true, "allowEdgeOverflow" : false});
        }
        {
            var Q0;
            Q0=makeQuery(id+"F31.opExtrude","SWEPT_FACE",FACE,{"disambiguationData":[OSD([sQuery(id+"F30.wireOp",EDGE,"E55.12.1")])]});
            var sketch = newSketch(context, id + "F36", { "sketchPlane" : qUnion([Q0])});
            skCircle(sketch, "E62.cCircle", {"center": v(-21.4, 3.5) * mm, "radius": 1.65 * mm, "construction": true});
            skPoint(sketch, "E62.cCircle.centerSnap0", {"position": v(-21.4, 8) * mm});
            skLineSegment(sketch, "E62.0", {"start": v(-20.44, 1.85) * mm, "end": v(-22.34, 1.85) * mm});
            skLineSegment(sketch, "E62.1", {"start": v(-22.34, 1.85) * mm, "end": v(-23.3, 3.5) * mm});
            skLineSegment(sketch, "E62.2", {"start": v(-23.3, 3.5) * mm, "end": v(-22.34, 5.15) * mm});
            skLineSegment(sketch, "E62.3", {"start": v(-22.34, 5.15) * mm, "end": v(-20.44, 5.15) * mm});
            skLineSegment(sketch, "E62.4", {"start": v(-20.44, 5.15) * mm, "end": v(-19.49, 3.5) * mm});
            skLineSegment(sketch, "E62.5", {"start": v(-19.49, 3.5) * mm, "end": v(-20.44, 1.85) * mm});
            skPoint(sketch, "E62.0.midPoint", {"position": v(-21.4, 1.85) * mm});
            skSolve(sketch);
        }
        {
            var Q0;
            Q0 = qSketchRegion(id + "F36", true);
            extrude(context, id + "F37", {"entities" : qUnion([Q0]), "operationType" : NewBodyOperationType.REMOVE, "oppositeDirection" : true, "depth" : 26 * mm, "symmetric" : true});
        }
        {
            var Q0;
            Q0=qCreatedBy(makeId("Top.planeOp"),FACE);
            var sketch = newSketch(context, id + "F38", { "sketchPlane" : qUnion([Q0])});
            skLineSegment(sketch, "E63.bottom", {"start": v(-48.83, 26.09) * mm, "end": v(-14.83, 26.09) * mm});
            skLineSegment(sketch, "E63.top", {"start": v(-48.83, 59.09) * mm, "end": v(-14.83, 59.09) * mm});
            skLineSegment(sketch, "E63.left", {"start": v(-48.83, 26.09) * mm, "end": v(-48.83, 59.09) * mm});
            skLineSegment(sketch, "E63.right", {"start": v(-14.83, 26.09) * mm, "end": v(-14.83, 46.09) * mm});
            skLineSegment(sketch, "E64.bottom", {"start": v(-40.83, 51.09) * mm, "end": v(-14.83, 51.09) * mm});
            skLineSegment(sketch, "E64.top", {"start": v(-40.83, 46.09) * mm, "end": v(-14.83, 46.09) * mm});
            skArc(sketch, "E65", {"start": v(-40.83, 51.09) * mm, "mid": v(-43.33, 48.59) * mm, "end": v(-40.83, 46.09) * mm});
            skLineSegment(sketch, "E66.trimOffspring", {"start": v(-14.83, 51.09) * mm, "end": v(-14.83, 59.09) * mm});
            skLineSegment(sketch, "E67", {"start": v(-31.83, 59.09) * mm, "end": v(-31.83, 26.09) * mm, "construction": true});
            skCircle(sketch, "E68", {"center": v(-21.83, 36.09) * mm, "radius": 2.6 * mm});
            skCircle(sketch, "E69.MirrorC", {"center": v(-41.83, 36.09) * mm, "radius": 2.6 * mm});
            skSolve(sketch);
        }
        {
            var Q0;
            Q0 = qSketchRegion(id + "F38", true);
            extrude(context, id + "F39", {"entities" : qUnion([Q0]), "depth" : 12 * mm});
        }
        {
            var Q0;
            Q0=makeQuery(id+"F39.opExtrude","SWEPT_FACE",FACE,{"disambiguationData":[OSD([sQuery(id+"F38.wireOp",EDGE,"E63.top")])]});
            var sketch = newSketch(context, id + "F40", { "sketchPlane" : qUnion([Q0])});
            skCircle(sketch, "E70", {"center": v(31.83, 6) * mm, "radius": 4 * mm});
            skPoint(sketch, "E70.centerSnap0", {"position": v(14.83, 6) * mm});
            skPoint(sketch, "E70.centerSnap1", {"position": v(31.83, 0) * mm});
            skSolve(sketch);
        }
        {
            var Q0;
            Q0 = qSketchRegion(id + "F40", true);
            extrude(context, id + "F41", {"entities" : qUnion([Q0]), "operationType" : NewBodyOperationType.REMOVE, "endBound" : BoundingType.THROUGH_ALL, "oppositeDirection" : true, "depth" : 25 * mm});
        }
        {
            var Q0;
            Q0=makeQuery(id+"F39.opExtrude","CAP_FACE",FACE,{"disambiguationData":[OSD([sQuery(id+"F38.wireOp",EDGE,"E63.bottom"),sQuery(id+"F38.wireOp",EDGE,"E63.top"),sQuery(id+"F38.wireOp",EDGE,"E63.left"),sQuery(id+"F38.wireOp",EDGE,"E63.right"),sQuery(id+"F38.wireOp",EDGE,"E64.bottom"),sQuery(id+"F38.wireOp",EDGE,"E64.top"),sQuery(id+"F38.wireOp",EDGE,"E65"),sQuery(id+"F38.wireOp",EDGE,"E66.trimOffspring"),sQuery(id+"F38.wireOp",EDGE,"E68"),sQuery(id+"F38.wireOp",EDGE,"E69.MirrorC")])],"isStart":false});
            var sketch = newSketch(context, id + "F42", { "sketchPlane" : qUnion([Q0])});
            skCircle(sketch, "E71", {"center": v(-21.83, 36.09) * mm, "radius": 5 * mm});
            skCircle(sketch, "E72", {"center": v(-41.83, 36.09) * mm, "radius": 5 * mm});
            skSolve(sketch);
        }
        {
            var Q0;
            Q0 = qSketchRegion(id + "F42", true);
            extrude(context, id + "F43", {"entities" : qUnion([Q0]), "operationType" : NewBodyOperationType.REMOVE, "oppositeDirection" : true, "depth" : 2 * mm});
        }
        {
            var Q0;
            Q0=makeQuery(id+"F39.opExtrude","CAP_FACE",FACE,{"disambiguationData":[OSD([sQuery(id+"F38.wireOp",EDGE,"E63.bottom"),sQuery(id+"F38.wireOp",EDGE,"E63.top"),sQuery(id+"F38.wireOp",EDGE,"E63.left"),sQuery(id+"F38.wireOp",EDGE,"E63.right"),sQuery(id+"F38.wireOp",EDGE,"E64.bottom"),sQuery(id+"F38.wireOp",EDGE,"E64.top"),sQuery(id+"F38.wireOp",EDGE,"E65"),sQuery(id+"F38.wireOp",EDGE,"E66.trimOffspring"),sQuery(id+"F38.wireOp",EDGE,"E68"),sQuery(id+"F38.wireOp",EDGE,"E69.MirrorC")])],"isStart":true});
            var sketch = newSketch(context, id + "F44", { "sketchPlane" : qUnion([Q0])});
            skCircle(sketch, "E73.cCircle", {"center": v(-21.83, -36.09) * mm, "radius": 4 * mm, "construction": true});
            skLineSegment(sketch, "E73.0", {"start": v(-17.83, -33.78) * mm, "end": v(-17.83, -38.4) * mm});
            skLineSegment(sketch, "E73.1", {"start": v(-17.83, -38.4) * mm, "end": v(-21.83, -40.7) * mm});
            skLineSegment(sketch, "E73.2", {"start": v(-21.83, -40.7) * mm, "end": v(-25.83, -38.4) * mm});
            skLineSegment(sketch, "E73.3", {"start": v(-25.83, -38.4) * mm, "end": v(-25.83, -33.78) * mm});
            skLineSegment(sketch, "E73.4", {"start": v(-25.83, -33.78) * mm, "end": v(-21.83, -31.47) * mm});
            skLineSegment(sketch, "E73.5", {"start": v(-21.83, -31.47) * mm, "end": v(-17.83, -33.78) * mm});
            skPoint(sketch, "E73.0.midPoint", {"position": v(-17.83, -36.09) * mm});
            skLineSegment(sketch, "E74", {"start": v(-31.83, -26.09) * mm, "end": v(-31.83, -46.09) * mm, "construction": true});
            skLineSegment(sketch, "E75.MirrorCS", {"start": v(-45.83, -38.4) * mm, "end": v(-41.83, -40.7) * mm});
            skLineSegment(sketch, "E76.MirrorCS", {"start": v(-45.83, -33.78) * mm, "end": v(-45.83, -38.4) * mm});
            skLineSegment(sketch, "E77.MirrorCS", {"start": v(-41.83, -31.47) * mm, "end": v(-45.83, -33.78) * mm});
            skLineSegment(sketch, "E78.MirrorCS", {"start": v(-41.83, -40.7) * mm, "end": v(-37.83, -38.4) * mm});
            skLineSegment(sketch, "E79.MirrorCS", {"start": v(-37.83, -33.78) * mm, "end": v(-41.83, -31.47) * mm});
            skLineSegment(sketch, "E80.MirrorCS", {"start": v(-37.83, -38.4) * mm, "end": v(-37.83, -33.78) * mm});
            skPoint(sketch, "E81.MirrorP", {"position": v(-45.83, -36.09) * mm});
            skCircle(sketch, "E82.MirrorC", {"center": v(-41.83, -36.09) * mm, "radius": 4 * mm, "construction": true});
            skSolve(sketch);
        }
        {
            var Q0;
            Q0 = qSketchRegion(id + "F44", true);
            extrude(context, id + "F45", {"entities" : qUnion([Q0]), "operationType" : NewBodyOperationType.REMOVE, "oppositeDirection" : true, "depth" : 5 * mm});
        }
        {
            var Q0;
            Q0=makeQuery(id+"F39.opExtrude","SWEPT_FACE",FACE,{"disambiguationData":[OSD([sQuery(id+"F38.wireOp",EDGE,"E63.top")])]});
            var sketch = newSketch(context, id + "F46", { "sketchPlane" : qUnion([Q0])});
            skCircle(sketch, "E83", {"center": v(21.98, 6) * mm, "radius": 2.4 * mm});
            skPoint(sketch, "E83.centerSnap0", {"position": v(14.83, 6) * mm});
            skSolve(sketch);
        }
        {
            var Q0;
            Q0 = qSketchRegion(id + "F46", true);
            extrude(context, id + "F47", {"entities" : qUnion([Q0]), "operationType" : NewBodyOperationType.REMOVE, "oppositeDirection" : true, "depth" : 9 * mm});
        }
        {
            var Q0;
            Q0=makeQuery(id+"F39.opExtrude","SWEPT_EDGE",EDGE,{"disambiguationData":[OSD([sQuery(id+"F38.wireOp",EDGE,"E63.top"),sQuery(id+"F38.wireOp",EDGE,"E63.left")])]});
            var Q1;
            Q1=makeQuery(id+"F39.opExtrude","SWEPT_EDGE",EDGE,{"disambiguationData":[OSD([sQuery(id+"F38.wireOp",EDGE,"E63.top"),sQuery(id+"F38.wireOp",EDGE,"E66.trimOffspring")])]});
            var Q2;
            Q2=makeQuery(id+"F39.opExtrude","SWEPT_EDGE",EDGE,{"disambiguationData":[OSD([sQuery(id+"F38.wireOp",EDGE,"E63.bottom"),sQuery(id+"F38.wireOp",EDGE,"E63.left")])]});
            var Q3;
            Q3=makeQuery(id+"F39.opExtrude","SWEPT_EDGE",EDGE,{"disambiguationData":[OSD([sQuery(id+"F38.wireOp",EDGE,"E63.bottom"),sQuery(id+"F38.wireOp",EDGE,"E63.right")])]});
            fillet(context, id + "F48", {"entities" : qUnion([Q0, Q1, Q2, Q3]), "radius" : 3.4 * mm, "tangentPropagation" : true, "allowEdgeOverflow" : false});
        }
        {
            var Q0;
            Q0=qCreatedBy(makeId("Right.planeOp"),FACE);
            var sketch = newSketch(context, id + "F49", { "sketchPlane" : qUnion([Q0])});
            skLineSegment(sketch, "E84", {"start": v(-54.32, 0) * mm, "end": v(-54.32, 5) * mm, "construction": true});
            skLineSegment(sketch, "E85", {"start": v(-58.32, 0) * mm, "end": v(-58.32, 5) * mm});
            skLineSegment(sketch, "E86", {"start": v(-58.32, 5) * mm, "end": v(-59.32, 5) * mm});
            skLineSegment(sketch, "E87", {"start": v(-59.32, 5) * mm, "end": v(-59.32, 4.5) * mm});
            skLineSegment(sketch, "E88", {"start": v(-61.32, 5) * mm, "end": v(-61.32, 4.5) * mm});
            skLineSegment(sketch, "E89", {"start": v(-61.32, 4.5) * mm, "end": v(-59.32, 4.5) * mm});
            skLineSegment(sketch, "E90", {"start": v(-61.32, 5) * mm, "end": v(-62.32, 5) * mm});
            skLineSegment(sketch, "E91", {"start": v(-62.32, 5) * mm, "end": v(-62.32, 0) * mm});
            skLineSegment(sketch, "E92", {"start": v(-62.32, 0) * mm, "end": v(-61.32, 0) * mm});
            skLineSegment(sketch, "E93", {"start": v(-61.32, 0) * mm, "end": v(-61.32, 0.5) * mm});
            skLineSegment(sketch, "E94", {"start": v(-58.32, 0) * mm, "end": v(-59.32, 0) * mm});
            skLineSegment(sketch, "E95", {"start": v(-59.32, 0) * mm, "end": v(-59.32, 0.5) * mm});
            skLineSegment(sketch, "E96", {"start": v(-59.32, 0.5) * mm, "end": v(-61.32, 0.5) * mm});
            skSolve(sketch);
        }
        {
            var Q0;
            Q0 = qSketchRegion(id + "F49", true);
            var Q1;
            Q1=sQuery(id+"F49.wireOp",EDGE,"E84");
            revolve(context, id + "F50", {"entities" : qUnion([Q0]), "axis" : qUnion([Q1]), "revolveType" : RevolveType.FULL});
        }
        {
            var Q0;
            Q0=makeQuery(id+"F50.opRevolve","SWEPT_EDGE",EDGE,{"disambiguationData":[OSD([sQuery(id+"F49.wireOp",EDGE,"E88"),sQuery(id+"F49.wireOp",EDGE,"E89")])]});
            var Q1;
            Q1=makeQuery(id+"F50.opRevolve","SWEPT_EDGE",EDGE,{"disambiguationData":[OSD([sQuery(id+"F49.wireOp",EDGE,"E87"),sQuery(id+"F49.wireOp",EDGE,"E89")])]});
            var Q2;
            Q2=makeQuery(id+"F50.opRevolve","SWEPT_EDGE",EDGE,{"disambiguationData":[OSD([sQuery(id+"F49.wireOp",EDGE,"E93"),sQuery(id+"F49.wireOp",EDGE,"E96")])]});
            var Q3;
            Q3=makeQuery(id+"F50.opRevolve","SWEPT_EDGE",EDGE,{"disambiguationData":[OSD([sQuery(id+"F49.wireOp",EDGE,"E95"),sQuery(id+"F49.wireOp",EDGE,"E96")])]});
            chamfer(context, id + "F51", {"entities" : qUnion([Q0, Q1, Q2, Q3]), "width" : 0.5 * mm, "tangentPropagation" : true});
        }
        {
            var Q0;
            Q0=qCreatedBy(makeId("Top.planeOp"),FACE);
            var sketch = newSketch(context, id + "F52", { "sketchPlane" : qUnion([Q0])});
            skCircle(sketch, "E97", {"center": v(0, 0) * mm, "radius": 5 * mm});
            skCircle(sketch, "E98", {"center": v(0, 0) * mm, "radius": 2.6 * mm});
            skSolve(sketch);
        }
        {
            var Q0;
            Q0 = qSketchRegion(id + "F52", true);
            extrude(context, id + "F53", {"entities" : qUnion([Q0]), "depth" : 1 * mm});
        }
        {
            var Q0;
            Q0=qCreatedBy(makeId("Front.planeOp"),FACE);
            var sketch = newSketch(context, id + "F54", { "sketchPlane" : qUnion([Q0])});
            skLineSegment(sketch, "E99", {"start": v(66.5, 0) * mm, "end": v(66.5, 5) * mm});
            skLineSegment(sketch, "E100", {"start": v(66.5, 5) * mm, "end": v(67.5, 5) * mm});
            skLineSegment(sketch, "E101", {"start": v(67.5, 5) * mm, "end": v(68, 4.5) * mm});
            skLineSegment(sketch, "E102", {"start": v(68, 4.5) * mm, "end": v(70.5, 4.5) * mm});
            skLineSegment(sketch, "E103", {"start": v(70.5, 4.5) * mm, "end": v(71, 5) * mm});
            skLineSegment(sketch, "E104", {"start": v(71, 5) * mm, "end": v(72, 5) * mm});
            skLineSegment(sketch, "E105", {"start": v(72, 5) * mm, "end": v(72, 0) * mm});
            skLineSegment(sketch, "E106", {"start": v(72, 0) * mm, "end": v(71, 0) * mm});
            skLineSegment(sketch, "E107", {"start": v(71, 0) * mm, "end": v(70.5, 0.5) * mm});
            skLineSegment(sketch, "E108", {"start": v(70.5, 0.5) * mm, "end": v(68, 0.5) * mm});
            skLineSegment(sketch, "E109", {"start": v(68, 0.5) * mm, "end": v(67.5, 0) * mm});
            skLineSegment(sketch, "E110", {"start": v(67.5, 0) * mm, "end": v(66.5, 0) * mm});
            skLineSegment(sketch, "E111", {"start": v(64, 0) * mm, "end": v(64, 5) * mm, "construction": true});
            skPoint(sketch, "E111.startSnap0", {"position": v(67, 0) * mm});
            skSolve(sketch);
        }
        {
            var Q0;
            Q0 = qSketchRegion(id + "F54", true);
            var Q1;
            Q1=sQuery(id+"F54.wireOp",EDGE,"E111");
            revolve(context, id + "F55", {"entities" : qUnion([Q0]), "axis" : qUnion([Q1]), "revolveType" : RevolveType.FULL});
        }
        {
            var Q0;
            Q0=qCreatedBy(makeId("Top.planeOp"),FACE);
            var sketch = newSketch(context, id + "F56", { "sketchPlane" : qUnion([Q0])});
            skCircle(sketch, "E112", {"center": v(-19.5, -26.12) * mm, "radius": 4.25 * mm});
            skCircle(sketch, "E113.cCircle", {"center": v(-19.5, -26.12) * mm, "radius": 2 * mm, "construction": true});
            skLineSegment(sketch, "E113.0", {"start": v(-17.5, -24.96) * mm, "end": v(-17.5, -27.27) * mm});
            skLineSegment(sketch, "E113.1", {"start": v(-17.5, -27.27) * mm, "end": v(-19.5, -28.43) * mm});
            skLineSegment(sketch, "E113.2", {"start": v(-19.5, -28.43) * mm, "end": v(-21.5, -27.27) * mm});
            skLineSegment(sketch, "E113.3", {"start": v(-21.5, -27.27) * mm, "end": v(-21.5, -24.96) * mm});
            skLineSegment(sketch, "E113.4", {"start": v(-21.5, -24.96) * mm, "end": v(-19.5, -23.8) * mm});
            skLineSegment(sketch, "E113.5", {"start": v(-19.5, -23.8) * mm, "end": v(-17.5, -24.96) * mm});
            skPoint(sketch, "E113.0.midPoint", {"position": v(-17.5, -26.12) * mm});
            skSolve(sketch);
        }
        {
            var Q0;
            Q0 = qSketchRegion(id + "F56", true);
            extrude(context, id + "F57", {"entities" : qUnion([Q0]), "depth" : 4 * mm});
        }
        {
            var Q0;
            Q0=makeQuery(id+"F57.opExtrude","CAP_FACE",FACE,{"disambiguationData":[OSD([sQuery(id+"F56.wireOp",EDGE,"E112"),sQuery(id+"F56.wireOp",EDGE,"E113.0"),sQuery(id+"F56.wireOp",EDGE,"E113.1"),sQuery(id+"F56.wireOp",EDGE,"E113.2"),sQuery(id+"F56.wireOp",EDGE,"E113.3"),sQuery(id+"F56.wireOp",EDGE,"E113.4"),sQuery(id+"F56.wireOp",EDGE,"E113.5")])],"isStart":false});
            var sketch = newSketch(context, id + "F58", { "sketchPlane" : qUnion([Q0])});
            skCircle(sketch, "E114.0", {"center": v(-19.5, -26.12) * mm, "radius": 4.25 * mm});
            skSolve(sketch);
        }
        {
            var Q0;
            Q0 = qSketchRegion(id + "F58", true);
            extrude(context, id + "F59", {"entities" : qUnion([Q0]), "operationType" : NewBodyOperationType.ADD, "depth" : 1 * mm});
        }
        {
            var Q0;
            Q0=makeQuery(id+"F59.opExtrude","CAP_FACE",FACE,{"disambiguationData":[OSD([sQuery(id+"F58.wireOp",EDGE,"E114.0")])],"isStart":false});
            var sketch = newSketch(context, id + "F60", { "sketchPlane" : qUnion([Q0])});
            skCircle(sketch, "E115", {"center": v(-19.5, -26.12) * mm, "radius": 2.45 * mm});
            skSolve(sketch);
        }
        {
            var Q0;
            Q0 = qSketchRegion(id + "F60", true);
            extrude(context, id + "F61", {"entities" : qUnion([Q0]), "operationType" : NewBodyOperationType.ADD, "depth" : 25 * mm});
        }
        {
            var Q0;
            Q0=qCreatedBy(makeId("Top.planeOp"),FACE);
            var sketch = newSketch(context, id + "F62", { "sketchPlane" : qUnion([Q0])});
            skCircle(sketch, "E116.cCircle", {"center": v(-10.34, -14.77) * mm, "radius": 4 * mm, "construction": true});
            skLineSegment(sketch, "E116.0", {"start": v(-14.34, -17.08) * mm, "end": v(-14.34, -12.46) * mm});
            skLineSegment(sketch, "E116.1", {"start": v(-14.34, -12.46) * mm, "end": v(-10.34, -10.15) * mm});
            skLineSegment(sketch, "E116.2", {"start": v(-10.34, -10.15) * mm, "end": v(-6.34, -12.46) * mm});
            skLineSegment(sketch, "E116.3", {"start": v(-6.34, -12.46) * mm, "end": v(-6.34, -17.08) * mm});
            skLineSegment(sketch, "E116.4", {"start": v(-6.34, -17.08) * mm, "end": v(-10.34, -19.39) * mm});
            skLineSegment(sketch, "E116.5", {"start": v(-10.34, -19.39) * mm, "end": v(-14.34, -17.08) * mm});
            skPoint(sketch, "E116.0.midPoint", {"position": v(-14.34, -14.77) * mm});
            skCircle(sketch, "E117", {"center": v(-10.34, -14.77) * mm, "radius": 2.5 * mm});
            skSolve(sketch);
        }
        {
            var Q0;
            Q0 = qSketchRegion(id + "F62", true);
            extrude(context, id + "F63", {"entities" : qUnion([Q0]), "depth" : 3.5 * mm});
        }
        {
            var Q0;
            Q0=makeQuery(id+"F63.opExtrude","CAP_FACE",FACE,{"disambiguationData":[OSD([sQuery(id+"F62.wireOp",EDGE,"E116.0"),sQuery(id+"F62.wireOp",EDGE,"E116.1"),sQuery(id+"F62.wireOp",EDGE,"E116.2"),sQuery(id+"F62.wireOp",EDGE,"E116.3"),sQuery(id+"F62.wireOp",EDGE,"E116.4"),sQuery(id+"F62.wireOp",EDGE,"E116.5"),sQuery(id+"F62.wireOp",EDGE,"E117")])],"isStart":false});
            var sketch = newSketch(context, id + "F64", { "sketchPlane" : qUnion([Q0])});
            skCircle(sketch, "E118.0", {"center": v(-10.34, -14.77) * mm, "radius": 2.5 * mm});
            skCircle(sketch, "E119", {"center": v(-10.34, -14.77) * mm, "radius": 4 * mm});
            skSolve(sketch);
        }
        {
            var Q0;
            Q0 = qSketchRegion(id + "F64", true);
            extrude(context, id + "F65", {"entities" : qUnion([Q0]), "operationType" : NewBodyOperationType.ADD, "depth" : 1.5 * mm});
        }
        {
            var Q0;
            Q0=makeQuery(id+"F65.opExtrude","CAP_EDGE",EDGE,{"disambiguationData":[OSD([sQuery(id+"F64.wireOp",EDGE,"E119")])],"isStart":false});
            fillet(context, id + "F66", {"entities" : qUnion([Q0]), "radius" : 1 * mm, "tangentPropagation" : true, "allowEdgeOverflow" : false});
        }
        {
            var Q0;
            Q0=qCreatedBy(makeId("Right.planeOp"),FACE);
            var sketch = newSketch(context, id + "F67", { "sketchPlane" : qUnion([Q0])});
            skLineSegment(sketch, "E120", {"start": v(-74.98, 0) * mm, "end": v(-74.98, 6) * mm, "construction": true});
            skLineSegment(sketch, "E121", {"start": v(-77.48, 0) * mm, "end": v(-80.58, 0) * mm});
            skLineSegment(sketch, "E122", {"start": v(-80.58, 0) * mm, "end": v(-80.58, 0.8) * mm});
            skLineSegment(sketch, "E123", {"start": v(-80.58, 0.8) * mm, "end": v(-79.98, 0.8) * mm});
            skLineSegment(sketch, "E124", {"start": v(-79.98, 0.8) * mm, "end": v(-79.98, 4) * mm});
            skLineSegment(sketch, "E125", {"start": v(-79.98, 4) * mm, "end": v(-77.48, 4) * mm});
            skLineSegment(sketch, "E126", {"start": v(-77.48, 4) * mm, "end": v(-77.48, 0) * mm});
            skSolve(sketch);
        }
        {
            var Q0;
            Q0 = qSketchRegion(id + "F67", true);
            var Q1;
            Q1=sQuery(id+"F67.wireOp",EDGE,"E120");
            revolve(context, id + "F68", {"entities" : qUnion([Q0]), "axis" : qUnion([Q1]), "revolveType" : RevolveType.FULL});
        }
        {
            var Q0;
            Q0=qCreatedBy(makeId("Top.planeOp"),FACE);
            var sketch = newSketch(context, id + "F69", { "sketchPlane" : qUnion([Q0])});
            skCircle(sketch, "E127", {"center": v(59.33, -21.9) * mm, "radius": 9 * mm});
            skCircle(sketch, "E128", {"center": v(59.33, -21.9) * mm, "radius": 5.75 * mm});
            skSolve(sketch);
        }
        {
            var Q0;
            Q0 = qSketchRegion(id + "F69", true);
            extrude(context, id + "F70", {"entities" : qUnion([Q0]), "depth" : 1 * mm});
        }
        {
            var Q0;
            Q0=makeQuery(id+"F70.opExtrude","CAP_FACE",FACE,{"disambiguationData":[OSD([sQuery(id+"F69.wireOp",EDGE,"E127"),sQuery(id+"F69.wireOp",EDGE,"E128")])],"isStart":true});
            var sketch = newSketch(context, id + "F71", { "sketchPlane" : qUnion([Q0])});
            skCircle(sketch, "E129", {"center": v(59.33, 21.9) * mm, "radius": 5.1 * mm});
            skCircle(sketch, "E130", {"center": v(59.33, 21.9) * mm, "radius": 7.6 * mm, "construction": true});
            skCircle(sketch, "E131.0", {"center": v(59.33, 21.9) * mm, "radius": 6.6 * mm, "construction": true});
            skLineSegment(sketch, "E132", {"start": v(59.33, 21.9) * mm, "end": v(59.33, 29.5) * mm, "construction": true});
            skLineSegment(sketch, "E133", {"start": v(58.48, 29.45) * mm, "end": v(58.83, 28.48) * mm});
            skLineSegment(sketch, "E134.MirrorCS", {"start": v(60.18, 29.45) * mm, "end": v(59.83, 28.48) * mm});
            skLineSegment(sketch, "E135.1.0", {"start": v(56.19, 28.82) * mm, "end": v(56.82, 28) * mm});
            skLineSegment(sketch, "E135.1.1", {"start": v(57.8, 29.34) * mm, "end": v(57.77, 28.3) * mm});
            skLineSegment(sketch, "E135.2.0", {"start": v(54.2, 27.5) * mm, "end": v(55.06, 26.93) * mm});
            skLineSegment(sketch, "E135.2.1", {"start": v(55.58, 28.5) * mm, "end": v(55.86, 27.51) * mm});
            skLineSegment(sketch, "E135.3.0", {"start": v(52.72, 25.65) * mm, "end": v(53.71, 25.36) * mm});
            skLineSegment(sketch, "E135.3.1", {"start": v(53.72, 27.02) * mm, "end": v(54.3, 26.17) * mm});
            skLineSegment(sketch, "E135.4.0", {"start": v(51.88, 23.42) * mm, "end": v(52.92, 23.46) * mm});
            skLineSegment(sketch, "E135.4.1", {"start": v(52.4, 25.04) * mm, "end": v(53.22, 24.4) * mm});
            skLineSegment(sketch, "E135.5.0", {"start": v(51.78, 21.05) * mm, "end": v(52.75, 21.4) * mm});
            skLineSegment(sketch, "E135.5.1", {"start": v(51.78, 22.75) * mm, "end": v(52.75, 22.4) * mm});
            skLineSegment(sketch, "E135.6.0", {"start": v(52.4, 18.75) * mm, "end": v(53.22, 19.4) * mm});
            skLineSegment(sketch, "E135.6.1", {"start": v(51.88, 20.37) * mm, "end": v(52.92, 20.33) * mm});
            skLineSegment(sketch, "E135.7.0", {"start": v(53.72, 16.77) * mm, "end": v(54.3, 17.63) * mm});
            skLineSegment(sketch, "E135.7.1", {"start": v(52.72, 18.14) * mm, "end": v(53.71, 18.43) * mm});
            skLineSegment(sketch, "E135.8.0", {"start": v(55.58, 15.29) * mm, "end": v(55.86, 16.28) * mm});
            skLineSegment(sketch, "E135.8.1", {"start": v(54.2, 16.29) * mm, "end": v(55.06, 16.86) * mm});
            skLineSegment(sketch, "E135.9.0", {"start": v(57.8, 14.45) * mm, "end": v(57.77, 15.48) * mm});
            skLineSegment(sketch, "E135.9.1", {"start": v(56.19, 14.98) * mm, "end": v(56.82, 15.8) * mm});
            skLineSegment(sketch, "E135.10.0", {"start": v(60.18, 14.34) * mm, "end": v(59.83, 15.32) * mm});
            skLineSegment(sketch, "E135.10.1", {"start": v(58.48, 14.34) * mm, "end": v(58.83, 15.32) * mm});
            skLineSegment(sketch, "E135.11.0", {"start": v(62.47, 14.98) * mm, "end": v(61.84, 15.8) * mm});
            skLineSegment(sketch, "E135.11.1", {"start": v(60.86, 14.45) * mm, "end": v(60.9, 15.48) * mm});
            skLineSegment(sketch, "E135.12.0", {"start": v(64.46, 16.29) * mm, "end": v(63.6, 16.86) * mm});
            skLineSegment(sketch, "E135.12.1", {"start": v(63.08, 15.29) * mm, "end": v(62.8, 16.28) * mm});
            skLineSegment(sketch, "E135.13.0", {"start": v(65.94, 18.14) * mm, "end": v(64.95, 18.43) * mm});
            skLineSegment(sketch, "E135.13.1", {"start": v(64.94, 16.77) * mm, "end": v(64.36, 17.63) * mm});
            skLineSegment(sketch, "E135.14.0", {"start": v(66.78, 20.37) * mm, "end": v(65.74, 20.33) * mm});
            skLineSegment(sketch, "E135.14.1", {"start": v(66.25, 18.75) * mm, "end": v(65.44, 19.4) * mm});
            skLineSegment(sketch, "E135.15.0", {"start": v(66.88, 22.75) * mm, "end": v(65.91, 22.4) * mm});
            skLineSegment(sketch, "E135.15.1", {"start": v(66.88, 21.05) * mm, "end": v(65.91, 21.4) * mm});
            skLineSegment(sketch, "E135.16.0", {"start": v(66.25, 25.04) * mm, "end": v(65.44, 24.4) * mm});
            skLineSegment(sketch, "E135.16.1", {"start": v(66.78, 23.42) * mm, "end": v(65.74, 23.46) * mm});
            skLineSegment(sketch, "E135.17.0", {"start": v(64.94, 27.02) * mm, "end": v(64.36, 26.17) * mm});
            skLineSegment(sketch, "E135.17.1", {"start": v(65.94, 25.65) * mm, "end": v(64.95, 25.36) * mm});
            skLineSegment(sketch, "E135.18.0", {"start": v(63.08, 28.5) * mm, "end": v(62.8, 27.51) * mm});
            skLineSegment(sketch, "E135.18.1", {"start": v(64.46, 27.5) * mm, "end": v(63.6, 26.93) * mm});
            skLineSegment(sketch, "E135.19.0", {"start": v(60.86, 29.34) * mm, "end": v(60.9, 28.3) * mm});
            skLineSegment(sketch, "E135.19.1", {"start": v(62.47, 28.82) * mm, "end": v(61.84, 28) * mm});
            skArc(sketch, "E136", {"start": v(60.18, 29.45) * mm, "mid": v(60.52, 29.4) * mm, "end": v(60.86, 29.34) * mm});
            skArc(sketch, "E137", {"start": v(60.9, 28.3) * mm, "mid": v(61.37, 28.17) * mm, "end": v(61.84, 28) * mm});
            skArc(sketch, "E138.1.0", {"start": v(57.8, 29.34) * mm, "mid": v(58.14, 29.4) * mm, "end": v(58.48, 29.45) * mm});
            skArc(sketch, "E138.1.1", {"start": v(58.83, 28.48) * mm, "mid": v(59.33, 28.5) * mm, "end": v(59.83, 28.48) * mm});
            skArc(sketch, "E138.2.0", {"start": v(55.58, 28.5) * mm, "mid": v(55.88, 28.67) * mm, "end": v(56.19, 28.82) * mm});
            skArc(sketch, "E138.2.1", {"start": v(56.82, 28) * mm, "mid": v(57.3, 28.17) * mm, "end": v(57.77, 28.3) * mm});
            skArc(sketch, "E138.3.0", {"start": v(53.72, 27.02) * mm, "mid": v(53.96, 27.27) * mm, "end": v(54.2, 27.5) * mm});
            skArc(sketch, "E138.3.1", {"start": v(55.06, 26.93) * mm, "mid": v(55.45, 27.24) * mm, "end": v(55.86, 27.51) * mm});
            skArc(sketch, "E138.4.0", {"start": v(52.4, 25.04) * mm, "mid": v(52.56, 25.35) * mm, "end": v(52.72, 25.65) * mm});
            skArc(sketch, "E138.4.1", {"start": v(53.71, 25.36) * mm, "mid": v(54, 25.78) * mm, "end": v(54.3, 26.17) * mm});
            skArc(sketch, "E138.5.0", {"start": v(51.78, 22.75) * mm, "mid": v(51.82, 23.09) * mm, "end": v(51.88, 23.42) * mm});
            skArc(sketch, "E138.5.1", {"start": v(52.92, 23.46) * mm, "mid": v(53.05, 23.94) * mm, "end": v(53.22, 24.4) * mm});
            skArc(sketch, "E138.6.0", {"start": v(51.88, 20.37) * mm, "mid": v(51.82, 20.7) * mm, "end": v(51.78, 21.05) * mm});
            skArc(sketch, "E138.6.1", {"start": v(52.75, 21.4) * mm, "mid": v(52.73, 21.9) * mm, "end": v(52.75, 22.4) * mm});
            skArc(sketch, "E138.7.0", {"start": v(52.72, 18.14) * mm, "mid": v(52.56, 18.45) * mm, "end": v(52.4, 18.75) * mm});
            skArc(sketch, "E138.7.1", {"start": v(53.22, 19.4) * mm, "mid": v(53.05, 19.86) * mm, "end": v(52.92, 20.33) * mm});
            skArc(sketch, "E138.8.0", {"start": v(54.2, 16.29) * mm, "mid": v(53.96, 16.52) * mm, "end": v(53.72, 16.77) * mm});
            skArc(sketch, "E138.8.1", {"start": v(54.3, 17.63) * mm, "mid": v(54, 18.02) * mm, "end": v(53.71, 18.43) * mm});
            skArc(sketch, "E138.9.0", {"start": v(56.19, 14.98) * mm, "mid": v(55.88, 15.12) * mm, "end": v(55.58, 15.29) * mm});
            skArc(sketch, "E138.9.1", {"start": v(55.86, 16.28) * mm, "mid": v(55.45, 16.56) * mm, "end": v(55.06, 16.86) * mm});
            skArc(sketch, "E138.10.0", {"start": v(58.48, 14.34) * mm, "mid": v(58.14, 14.39) * mm, "end": v(57.8, 14.45) * mm});
            skArc(sketch, "E138.10.1", {"start": v(57.77, 15.48) * mm, "mid": v(57.3, 15.62) * mm, "end": v(56.82, 15.8) * mm});
            skArc(sketch, "E138.11.0", {"start": v(60.86, 14.45) * mm, "mid": v(60.52, 14.39) * mm, "end": v(60.18, 14.34) * mm});
            skArc(sketch, "E138.11.1", {"start": v(59.83, 15.32) * mm, "mid": v(59.33, 15.3) * mm, "end": v(58.83, 15.32) * mm});
            skArc(sketch, "E138.12.0", {"start": v(63.08, 15.29) * mm, "mid": v(62.78, 15.12) * mm, "end": v(62.47, 14.98) * mm});
            skArc(sketch, "E138.12.1", {"start": v(61.84, 15.8) * mm, "mid": v(61.37, 15.62) * mm, "end": v(60.9, 15.48) * mm});
            skArc(sketch, "E138.13.0", {"start": v(64.94, 16.77) * mm, "mid": v(64.7, 16.52) * mm, "end": v(64.46, 16.29) * mm});
            skArc(sketch, "E138.13.1", {"start": v(63.6, 16.86) * mm, "mid": v(63.2, 16.56) * mm, "end": v(62.8, 16.28) * mm});
            skArc(sketch, "E138.14.0", {"start": v(66.25, 18.75) * mm, "mid": v(66.1, 18.45) * mm, "end": v(65.94, 18.14) * mm});
            skArc(sketch, "E138.14.1", {"start": v(64.95, 18.43) * mm, "mid": v(64.67, 18.02) * mm, "end": v(64.36, 17.63) * mm});
            skArc(sketch, "E138.15.0", {"start": v(66.88, 21.05) * mm, "mid": v(66.84, 20.7) * mm, "end": v(66.78, 20.37) * mm});
            skArc(sketch, "E138.15.1", {"start": v(65.74, 20.33) * mm, "mid": v(65.6, 19.86) * mm, "end": v(65.44, 19.4) * mm});
            skArc(sketch, "E138.16.0", {"start": v(66.78, 23.42) * mm, "mid": v(66.84, 23.09) * mm, "end": v(66.88, 22.75) * mm});
            skArc(sketch, "E138.16.1", {"start": v(65.91, 22.4) * mm, "mid": v(65.93, 21.9) * mm, "end": v(65.91, 21.4) * mm});
            skArc(sketch, "E138.17.0", {"start": v(65.94, 25.65) * mm, "mid": v(66.1, 25.35) * mm, "end": v(66.25, 25.04) * mm});
            skArc(sketch, "E138.17.1", {"start": v(65.44, 24.4) * mm, "mid": v(65.6, 23.94) * mm, "end": v(65.74, 23.46) * mm});
            skArc(sketch, "E138.18.0", {"start": v(64.46, 27.5) * mm, "mid": v(64.7, 27.27) * mm, "end": v(64.94, 27.02) * mm});
            skArc(sketch, "E138.18.1", {"start": v(64.36, 26.17) * mm, "mid": v(64.67, 25.78) * mm, "end": v(64.95, 25.36) * mm});
            skArc(sketch, "E138.19.0", {"start": v(62.47, 28.82) * mm, "mid": v(62.78, 28.67) * mm, "end": v(63.08, 28.5) * mm});
            skArc(sketch, "E138.19.1", {"start": v(62.8, 27.51) * mm, "mid": v(63.2, 27.24) * mm, "end": v(63.6, 26.93) * mm});
            skSolve(sketch);
        }
        {
            var Q0;
            Q0 = qSketchRegion(id + "F71", true);
            extrude(context, id + "F72", {"entities" : qUnion([Q0]), "operationType" : NewBodyOperationType.ADD, "depth" : 3.2 * mm});
        }
        {
            var Q0;
            Q0=makeQuery(id+"F72.opExtrude","CAP_FACE",FACE,{"disambiguationData":[OSD([sQuery(id+"F71.wireOp",EDGE,"E129"),sQuery(id+"F71.wireOp",EDGE,"E133"),sQuery(id+"F71.wireOp",EDGE,"E134.MirrorCS"),sQuery(id+"F71.wireOp",EDGE,"E135.1.0"),sQuery(id+"F71.wireOp",EDGE,"E135.1.1"),sQuery(id+"F71.wireOp",EDGE,"E135.2.0"),sQuery(id+"F71.wireOp",EDGE,"E135.2.1"),sQuery(id+"F71.wireOp",EDGE,"E135.3.0"),sQuery(id+"F71.wireOp",EDGE,"E135.3.1"),sQuery(id+"F71.wireOp",EDGE,"E135.4.0"),sQuery(id+"F71.wireOp",EDGE,"E135.4.1"),sQuery(id+"F71.wireOp",EDGE,"E135.5.0"),sQuery(id+"F71.wireOp",EDGE,"E135.5.1"),sQuery(id+"F71.wireOp",EDGE,"E135.6.0"),sQuery(id+"F71.wireOp",EDGE,"E135.6.1"),sQuery(id+"F71.wireOp",EDGE,"E135.7.0"),sQuery(id+"F71.wireOp",EDGE,"E135.7.1"),sQuery(id+"F71.wireOp",EDGE,"E135.8.0"),sQuery(id+"F71.wireOp",EDGE,"E135.8.1"),sQuery(id+"F71.wireOp",EDGE,"E135.9.0"),sQuery(id+"F71.wireOp",EDGE,"E135.9.1"),sQuery(id+"F71.wireOp",EDGE,"E135.10.0"),sQuery(id+"F71.wireOp",EDGE,"E135.10.1"),sQuery(id+"F71.wireOp",EDGE,"E135.11.0"),sQuery(id+"F71.wireOp",EDGE,"E135.11.1"),sQuery(id+"F71.wireOp",EDGE,"E135.12.0"),sQuery(id+"F71.wireOp",EDGE,"E135.12.1"),sQuery(id+"F71.wireOp",EDGE,"E135.13.0"),sQuery(id+"F71.wireOp",EDGE,"E135.13.1"),sQuery(id+"F71.wireOp",EDGE,"E135.14.0"),sQuery(id+"F71.wireOp",EDGE,"E135.14.1"),sQuery(id+"F71.wireOp",EDGE,"E135.15.0"),sQuery(id+"F71.wireOp",EDGE,"E135.15.1"),sQuery(id+"F71.wireOp",EDGE,"E135.16.0"),sQuery(id+"F71.wireOp",EDGE,"E135.16.1"),sQuery(id+"F71.wireOp",EDGE,"E135.17.0"),sQuery(id+"F71.wireOp",EDGE,"E135.17.1"),sQuery(id+"F71.wireOp",EDGE,"E135.18.0"),sQuery(id+"F71.wireOp",EDGE,"E135.18.1"),sQuery(id+"F71.wireOp",EDGE,"E135.19.0"),sQuery(id+"F71.wireOp",EDGE,"E135.19.1"),sQuery(id+"F71.wireOp",EDGE,"E136"),sQuery(id+"F71.wireOp",EDGE,"E137"),sQuery(id+"F71.wireOp",EDGE,"E138.1.0"),sQuery(id+"F71.wireOp",EDGE,"E138.1.1"),sQuery(id+"F71.wireOp",EDGE,"E138.2.0"),sQuery(id+"F71.wireOp",EDGE,"E138.2.1"),sQuery(id+"F71.wireOp",EDGE,"E138.3.0"),sQuery(id+"F71.wireOp",EDGE,"E138.3.1"),sQuery(id+"F71.wireOp",EDGE,"E138.4.0"),sQuery(id+"F71.wireOp",EDGE,"E138.4.1"),sQuery(id+"F71.wireOp",EDGE,"E138.5.0"),sQuery(id+"F71.wireOp",EDGE,"E138.5.1"),sQuery(id+"F71.wireOp",EDGE,"E138.6.0"),sQuery(id+"F71.wireOp",EDGE,"E138.6.1"),sQuery(id+"F71.wireOp",EDGE,"E138.7.0"),sQuery(id+"F71.wireOp",EDGE,"E138.7.1"),sQuery(id+"F71.wireOp",EDGE,"E138.8.0"),sQuery(id+"F71.wireOp",EDGE,"E138.8.1"),sQuery(id+"F71.wireOp",EDGE,"E138.9.0"),sQuery(id+"F71.wireOp",EDGE,"E138.9.1"),sQuery(id+"F71.wireOp",EDGE,"E138.10.0"),sQuery(id+"F71.wireOp",EDGE,"E138.10.1"),sQuery(id+"F71.wireOp",EDGE,"E138.11.0"),sQuery(id+"F71.wireOp",EDGE,"E138.11.1"),sQuery(id+"F71.wireOp",EDGE,"E138.12.0"),sQuery(id+"F71.wireOp",EDGE,"E138.12.1"),sQuery(id+"F71.wireOp",EDGE,"E138.13.0"),sQuery(id+"F71.wireOp",EDGE,"E138.13.1"),sQuery(id+"F71.wireOp",EDGE,"E138.14.0"),sQuery(id+"F71.wireOp",EDGE,"E138.14.1"),sQuery(id+"F71.wireOp",EDGE,"E138.15.0"),sQuery(id+"F71.wireOp",EDGE,"E138.15.1"),sQuery(id+"F71.wireOp",EDGE,"E138.16.0"),sQuery(id+"F71.wireOp",EDGE,"E138.16.1"),sQuery(id+"F71.wireOp",EDGE,"E138.17.0"),sQuery(id+"F71.wireOp",EDGE,"E138.17.1"),sQuery(id+"F71.wireOp",EDGE,"E138.18.0"),sQuery(id+"F71.wireOp",EDGE,"E138.18.1"),sQuery(id+"F71.wireOp",EDGE,"E138.19.0"),sQuery(id+"F71.wireOp",EDGE,"E138.19.1")])],"isStart":false});
            var sketch = newSketch(context, id + "F73", { "sketchPlane" : qUnion([Q0])});
            skLineSegment(sketch, "E139.0", {"start": v(60.18, 29.45) * mm, "end": v(59.83, 28.48) * mm});
            skArc(sketch, "E140.0", {"start": v(58.83, 28.48) * mm, "mid": v(59.33, 28.5) * mm, "end": v(59.83, 28.48) * mm});
            skLineSegment(sketch, "E141.0", {"start": v(58.48, 29.45) * mm, "end": v(58.83, 28.48) * mm});
            skArc(sketch, "E142.0", {"start": v(60.18, 29.45) * mm, "mid": v(60.52, 29.4) * mm, "end": v(60.86, 29.34) * mm});
            skLineSegment(sketch, "E143.1.0", {"start": v(56.19, 28.82) * mm, "end": v(56.82, 28) * mm});
            skArc(sketch, "E143.1.1", {"start": v(56.82, 28) * mm, "mid": v(57.3, 28.17) * mm, "end": v(57.77, 28.3) * mm});
            skLineSegment(sketch, "E143.1.2", {"start": v(57.8, 29.34) * mm, "end": v(57.77, 28.3) * mm});
            skArc(sketch, "E143.1.3", {"start": v(57.8, 29.34) * mm, "mid": v(58.14, 29.4) * mm, "end": v(58.48, 29.45) * mm});
            skLineSegment(sketch, "E143.2.0", {"start": v(54.2, 27.5) * mm, "end": v(55.06, 26.93) * mm});
            skArc(sketch, "E143.2.1", {"start": v(55.06, 26.93) * mm, "mid": v(55.45, 27.24) * mm, "end": v(55.86, 27.51) * mm});
            skLineSegment(sketch, "E143.2.2", {"start": v(55.58, 28.5) * mm, "end": v(55.86, 27.51) * mm});
            skArc(sketch, "E143.2.3", {"start": v(55.58, 28.5) * mm, "mid": v(55.88, 28.67) * mm, "end": v(56.19, 28.82) * mm});
            skLineSegment(sketch, "E143.3.0", {"start": v(52.72, 25.65) * mm, "end": v(53.71, 25.36) * mm});
            skArc(sketch, "E143.3.1", {"start": v(53.71, 25.36) * mm, "mid": v(54, 25.78) * mm, "end": v(54.3, 26.17) * mm});
            skLineSegment(sketch, "E143.3.2", {"start": v(53.72, 27.02) * mm, "end": v(54.3, 26.17) * mm});
            skArc(sketch, "E143.3.3", {"start": v(53.72, 27.02) * mm, "mid": v(53.96, 27.27) * mm, "end": v(54.2, 27.5) * mm});
            skLineSegment(sketch, "E143.4.0", {"start": v(51.88, 23.42) * mm, "end": v(52.92, 23.46) * mm});
            skArc(sketch, "E143.4.1", {"start": v(52.92, 23.46) * mm, "mid": v(53.05, 23.94) * mm, "end": v(53.22, 24.4) * mm});
            skLineSegment(sketch, "E143.4.2", {"start": v(52.4, 25.04) * mm, "end": v(53.22, 24.4) * mm});
            skArc(sketch, "E143.4.3", {"start": v(52.4, 25.04) * mm, "mid": v(52.56, 25.35) * mm, "end": v(52.72, 25.65) * mm});
            skLineSegment(sketch, "E143.5.0", {"start": v(51.78, 21.05) * mm, "end": v(52.75, 21.4) * mm});
            skArc(sketch, "E143.5.1", {"start": v(52.75, 21.4) * mm, "mid": v(52.73, 21.9) * mm, "end": v(52.75, 22.4) * mm});
            skLineSegment(sketch, "E143.5.2", {"start": v(51.78, 22.75) * mm, "end": v(52.75, 22.4) * mm});
            skArc(sketch, "E143.5.3", {"start": v(51.78, 22.75) * mm, "mid": v(51.82, 23.09) * mm, "end": v(51.88, 23.42) * mm});
            skLineSegment(sketch, "E143.6.0", {"start": v(52.4, 18.75) * mm, "end": v(53.22, 19.4) * mm});
            skArc(sketch, "E143.6.1", {"start": v(53.22, 19.4) * mm, "mid": v(53.05, 19.86) * mm, "end": v(52.92, 20.33) * mm});
            skLineSegment(sketch, "E143.6.2", {"start": v(51.88, 20.37) * mm, "end": v(52.92, 20.33) * mm});
            skArc(sketch, "E143.6.3", {"start": v(51.88, 20.37) * mm, "mid": v(51.82, 20.7) * mm, "end": v(51.78, 21.05) * mm});
            skLineSegment(sketch, "E143.7.0", {"start": v(53.72, 16.77) * mm, "end": v(54.3, 17.63) * mm});
            skArc(sketch, "E143.7.1", {"start": v(54.3, 17.63) * mm, "mid": v(54, 18.02) * mm, "end": v(53.71, 18.43) * mm});
            skLineSegment(sketch, "E143.7.2", {"start": v(52.72, 18.14) * mm, "end": v(53.71, 18.43) * mm});
            skArc(sketch, "E143.7.3", {"start": v(52.72, 18.14) * mm, "mid": v(52.56, 18.45) * mm, "end": v(52.4, 18.75) * mm});
            skLineSegment(sketch, "E143.8.0", {"start": v(55.58, 15.29) * mm, "end": v(55.86, 16.28) * mm});
            skArc(sketch, "E143.8.1", {"start": v(55.86, 16.28) * mm, "mid": v(55.45, 16.56) * mm, "end": v(55.06, 16.86) * mm});
            skLineSegment(sketch, "E143.8.2", {"start": v(54.2, 16.29) * mm, "end": v(55.06, 16.86) * mm});
            skArc(sketch, "E143.8.3", {"start": v(54.2, 16.29) * mm, "mid": v(53.96, 16.52) * mm, "end": v(53.72, 16.77) * mm});
            skLineSegment(sketch, "E143.9.0", {"start": v(57.8, 14.45) * mm, "end": v(57.77, 15.48) * mm});
            skArc(sketch, "E143.9.1", {"start": v(57.77, 15.48) * mm, "mid": v(57.3, 15.62) * mm, "end": v(56.82, 15.8) * mm});
            skLineSegment(sketch, "E143.9.2", {"start": v(56.19, 14.98) * mm, "end": v(56.82, 15.8) * mm});
            skArc(sketch, "E143.9.3", {"start": v(56.19, 14.98) * mm, "mid": v(55.88, 15.12) * mm, "end": v(55.58, 15.29) * mm});
            skLineSegment(sketch, "E143.10.0", {"start": v(60.18, 14.34) * mm, "end": v(59.83, 15.32) * mm});
            skArc(sketch, "E143.10.1", {"start": v(59.83, 15.32) * mm, "mid": v(59.33, 15.3) * mm, "end": v(58.83, 15.32) * mm});
            skLineSegment(sketch, "E143.10.2", {"start": v(58.48, 14.34) * mm, "end": v(58.83, 15.32) * mm});
            skArc(sketch, "E143.10.3", {"start": v(58.48, 14.34) * mm, "mid": v(58.14, 14.39) * mm, "end": v(57.8, 14.45) * mm});
            skLineSegment(sketch, "E143.11.0", {"start": v(62.47, 14.98) * mm, "end": v(61.84, 15.8) * mm});
            skArc(sketch, "E143.11.1", {"start": v(61.84, 15.8) * mm, "mid": v(61.37, 15.62) * mm, "end": v(60.9, 15.48) * mm});
            skLineSegment(sketch, "E143.11.2", {"start": v(60.86, 14.45) * mm, "end": v(60.9, 15.48) * mm});
            skArc(sketch, "E143.11.3", {"start": v(60.86, 14.45) * mm, "mid": v(60.52, 14.39) * mm, "end": v(60.18, 14.34) * mm});
            skLineSegment(sketch, "E143.12.0", {"start": v(64.46, 16.29) * mm, "end": v(63.6, 16.86) * mm});
            skArc(sketch, "E143.12.1", {"start": v(63.6, 16.86) * mm, "mid": v(63.2, 16.56) * mm, "end": v(62.8, 16.28) * mm});
            skLineSegment(sketch, "E143.12.2", {"start": v(63.08, 15.29) * mm, "end": v(62.8, 16.28) * mm});
            skArc(sketch, "E143.12.3", {"start": v(63.08, 15.29) * mm, "mid": v(62.78, 15.12) * mm, "end": v(62.47, 14.98) * mm});
            skLineSegment(sketch, "E143.13.0", {"start": v(65.94, 18.14) * mm, "end": v(64.95, 18.43) * mm});
            skArc(sketch, "E143.13.1", {"start": v(64.95, 18.43) * mm, "mid": v(64.67, 18.02) * mm, "end": v(64.36, 17.63) * mm});
            skLineSegment(sketch, "E143.13.2", {"start": v(64.94, 16.77) * mm, "end": v(64.36, 17.63) * mm});
            skArc(sketch, "E143.13.3", {"start": v(64.94, 16.77) * mm, "mid": v(64.7, 16.52) * mm, "end": v(64.46, 16.29) * mm});
            skLineSegment(sketch, "E143.14.0", {"start": v(66.78, 20.37) * mm, "end": v(65.74, 20.33) * mm});
            skArc(sketch, "E143.14.1", {"start": v(65.74, 20.33) * mm, "mid": v(65.6, 19.86) * mm, "end": v(65.44, 19.4) * mm});
            skLineSegment(sketch, "E143.14.2", {"start": v(66.25, 18.75) * mm, "end": v(65.44, 19.4) * mm});
            skArc(sketch, "E143.14.3", {"start": v(66.25, 18.75) * mm, "mid": v(66.1, 18.45) * mm, "end": v(65.94, 18.14) * mm});
            skLineSegment(sketch, "E143.15.0", {"start": v(66.88, 22.75) * mm, "end": v(65.91, 22.4) * mm});
            skArc(sketch, "E143.15.1", {"start": v(65.91, 22.4) * mm, "mid": v(65.93, 21.9) * mm, "end": v(65.91, 21.4) * mm});
            skLineSegment(sketch, "E143.15.2", {"start": v(66.88, 21.05) * mm, "end": v(65.91, 21.4) * mm});
            skArc(sketch, "E143.15.3", {"start": v(66.88, 21.05) * mm, "mid": v(66.84, 20.7) * mm, "end": v(66.78, 20.37) * mm});
            skLineSegment(sketch, "E143.16.0", {"start": v(66.25, 25.04) * mm, "end": v(65.44, 24.4) * mm});
            skArc(sketch, "E143.16.1", {"start": v(65.44, 24.4) * mm, "mid": v(65.6, 23.94) * mm, "end": v(65.74, 23.46) * mm});
            skLineSegment(sketch, "E143.16.2", {"start": v(66.78, 23.42) * mm, "end": v(65.74, 23.46) * mm});
            skArc(sketch, "E143.16.3", {"start": v(66.78, 23.42) * mm, "mid": v(66.84, 23.09) * mm, "end": v(66.88, 22.75) * mm});
            skLineSegment(sketch, "E143.17.0", {"start": v(64.94, 27.02) * mm, "end": v(64.36, 26.17) * mm});
            skArc(sketch, "E143.17.1", {"start": v(64.36, 26.17) * mm, "mid": v(64.67, 25.78) * mm, "end": v(64.95, 25.36) * mm});
            skLineSegment(sketch, "E143.17.2", {"start": v(65.94, 25.65) * mm, "end": v(64.95, 25.36) * mm});
            skArc(sketch, "E143.17.3", {"start": v(65.94, 25.65) * mm, "mid": v(66.1, 25.35) * mm, "end": v(66.25, 25.04) * mm});
            skLineSegment(sketch, "E143.18.0", {"start": v(63.08, 28.5) * mm, "end": v(62.8, 27.51) * mm});
            skArc(sketch, "E143.18.1", {"start": v(62.8, 27.51) * mm, "mid": v(63.2, 27.24) * mm, "end": v(63.6, 26.93) * mm});
            skLineSegment(sketch, "E143.18.2", {"start": v(64.46, 27.5) * mm, "end": v(63.6, 26.93) * mm});
            skArc(sketch, "E143.18.3", {"start": v(64.46, 27.5) * mm, "mid": v(64.7, 27.27) * mm, "end": v(64.94, 27.02) * mm});
            skLineSegment(sketch, "E143.19.0", {"start": v(60.86, 29.34) * mm, "end": v(60.9, 28.3) * mm});
            skArc(sketch, "E143.19.1", {"start": v(60.9, 28.3) * mm, "mid": v(61.37, 28.17) * mm, "end": v(61.84, 28) * mm});
            skLineSegment(sketch, "E143.19.2", {"start": v(62.47, 28.82) * mm, "end": v(61.84, 28) * mm});
            skArc(sketch, "E143.19.3", {"start": v(62.47, 28.82) * mm, "mid": v(62.78, 28.67) * mm, "end": v(63.08, 28.5) * mm});
            skCircle(sketch, "E144", {"center": v(59.33, 21.9) * mm, "radius": 3 * mm});
            skSolve(sketch);
        }
        {
            var Q0;
            Q0 = qSketchRegion(id + "F73", true);
            extrude(context, id + "F74", {"entities" : qUnion([Q0]), "operationType" : NewBodyOperationType.ADD, "depth" : 4.6 * mm});
        }
        {
            var Q0;
            Q0=makeQuery(id+"F74.opExtrude","CAP_FACE",FACE,{"disambiguationData":[OSD([sQuery(id+"F73.wireOp",EDGE,"E139.0"),sQuery(id+"F73.wireOp",EDGE,"E140.0"),sQuery(id+"F73.wireOp",EDGE,"E141.0"),sQuery(id+"F73.wireOp",EDGE,"E142.0"),sQuery(id+"F73.wireOp",EDGE,"E143.1.0"),sQuery(id+"F73.wireOp",EDGE,"E143.1.1"),sQuery(id+"F73.wireOp",EDGE,"E143.1.2"),sQuery(id+"F73.wireOp",EDGE,"E143.1.3"),sQuery(id+"F73.wireOp",EDGE,"E143.2.0"),sQuery(id+"F73.wireOp",EDGE,"E143.2.1"),sQuery(id+"F73.wireOp",EDGE,"E143.2.2"),sQuery(id+"F73.wireOp",EDGE,"E143.2.3"),sQuery(id+"F73.wireOp",EDGE,"E143.3.0"),sQuery(id+"F73.wireOp",EDGE,"E143.3.1"),sQuery(id+"F73.wireOp",EDGE,"E143.3.2"),sQuery(id+"F73.wireOp",EDGE,"E143.3.3"),sQuery(id+"F73.wireOp",EDGE,"E143.4.0"),sQuery(id+"F73.wireOp",EDGE,"E143.4.1"),sQuery(id+"F73.wireOp",EDGE,"E143.4.2"),sQuery(id+"F73.wireOp",EDGE,"E143.4.3"),sQuery(id+"F73.wireOp",EDGE,"E143.5.0"),sQuery(id+"F73.wireOp",EDGE,"E143.5.1"),sQuery(id+"F73.wireOp",EDGE,"E143.5.2"),sQuery(id+"F73.wireOp",EDGE,"E143.5.3"),sQuery(id+"F73.wireOp",EDGE,"E143.6.0"),sQuery(id+"F73.wireOp",EDGE,"E143.6.1"),sQuery(id+"F73.wireOp",EDGE,"E143.6.2"),sQuery(id+"F73.wireOp",EDGE,"E143.6.3"),sQuery(id+"F73.wireOp",EDGE,"E143.7.0"),sQuery(id+"F73.wireOp",EDGE,"E143.7.1"),sQuery(id+"F73.wireOp",EDGE,"E143.7.2"),sQuery(id+"F73.wireOp",EDGE,"E143.7.3"),sQuery(id+"F73.wireOp",EDGE,"E143.8.0"),sQuery(id+"F73.wireOp",EDGE,"E143.8.1"),sQuery(id+"F73.wireOp",EDGE,"E143.8.2"),sQuery(id+"F73.wireOp",EDGE,"E143.8.3"),sQuery(id+"F73.wireOp",EDGE,"E143.9.0"),sQuery(id+"F73.wireOp",EDGE,"E143.9.1"),sQuery(id+"F73.wireOp",EDGE,"E143.9.2"),sQuery(id+"F73.wireOp",EDGE,"E143.9.3"),sQuery(id+"F73.wireOp",EDGE,"E143.10.0"),sQuery(id+"F73.wireOp",EDGE,"E143.10.1"),sQuery(id+"F73.wireOp",EDGE,"E143.10.2"),sQuery(id+"F73.wireOp",EDGE,"E143.10.3"),sQuery(id+"F73.wireOp",EDGE,"E143.11.0"),sQuery(id+"F73.wireOp",EDGE,"E143.11.1"),sQuery(id+"F73.wireOp",EDGE,"E143.11.2"),sQuery(id+"F73.wireOp",EDGE,"E143.11.3"),sQuery(id+"F73.wireOp",EDGE,"E143.12.0"),sQuery(id+"F73.wireOp",EDGE,"E143.12.1"),sQuery(id+"F73.wireOp",EDGE,"E143.12.2"),sQuery(id+"F73.wireOp",EDGE,"E143.12.3"),sQuery(id+"F73.wireOp",EDGE,"E143.13.0"),sQuery(id+"F73.wireOp",EDGE,"E143.13.1"),sQuery(id+"F73.wireOp",EDGE,"E143.13.2"),sQuery(id+"F73.wireOp",EDGE,"E143.13.3"),sQuery(id+"F73.wireOp",EDGE,"E143.14.0"),sQuery(id+"F73.wireOp",EDGE,"E143.14.1"),sQuery(id+"F73.wireOp",EDGE,"E143.14.2"),sQuery(id+"F73.wireOp",EDGE,"E143.14.3"),sQuery(id+"F73.wireOp",EDGE,"E143.15.0"),sQuery(id+"F73.wireOp",EDGE,"E143.15.1"),sQuery(id+"F73.wireOp",EDGE,"E143.15.2"),sQuery(id+"F73.wireOp",EDGE,"E143.15.3"),sQuery(id+"F73.wireOp",EDGE,"E143.16.0"),sQuery(id+"F73.wireOp",EDGE,"E143.16.1"),sQuery(id+"F73.wireOp",EDGE,"E143.16.2"),sQuery(id+"F73.wireOp",EDGE,"E143.16.3"),sQuery(id+"F73.wireOp",EDGE,"E143.17.0"),sQuery(id+"F73.wireOp",EDGE,"E143.17.1"),sQuery(id+"F73.wireOp",EDGE,"E143.17.2"),sQuery(id+"F73.wireOp",EDGE,"E143.17.3"),sQuery(id+"F73.wireOp",EDGE,"E143.18.0"),sQuery(id+"F73.wireOp",EDGE,"E143.18.1"),sQuery(id+"F73.wireOp",EDGE,"E143.18.2"),sQuery(id+"F73.wireOp",EDGE,"E143.18.3"),sQuery(id+"F73.wireOp",EDGE,"E143.19.0"),sQuery(id+"F73.wireOp",EDGE,"E143.19.1"),sQuery(id+"F73.wireOp",EDGE,"E143.19.2"),sQuery(id+"F73.wireOp",EDGE,"E143.19.3"),sQuery(id+"F73.wireOp",EDGE,"E144")])],"isStart":false});
            var sketch = newSketch(context, id + "F75", { "sketchPlane" : qUnion([Q0])});
            skCircle(sketch, "E145", {"center": v(59.33, 21.9) * mm, "radius": 5.1 * mm});
            skLineSegment(sketch, "E146.0", {"start": v(58.48, 29.45) * mm, "end": v(58.83, 28.48) * mm});
            skArc(sketch, "E147.0", {"start": v(58.83, 28.48) * mm, "mid": v(59.33, 28.5) * mm, "end": v(59.83, 28.48) * mm});
            skLineSegment(sketch, "E148.0", {"start": v(60.18, 29.45) * mm, "end": v(59.83, 28.48) * mm});
            skArc(sketch, "E149.0", {"start": v(60.18, 29.45) * mm, "mid": v(60.52, 29.4) * mm, "end": v(60.86, 29.34) * mm});
            skLineSegment(sketch, "E150.1.0", {"start": v(56.19, 28.82) * mm, "end": v(56.82, 28) * mm});
            skLineSegment(sketch, "E150.1.1", {"start": v(57.8, 29.34) * mm, "end": v(57.77, 28.3) * mm});
            skArc(sketch, "E150.1.2", {"start": v(56.82, 28) * mm, "mid": v(57.3, 28.17) * mm, "end": v(57.77, 28.3) * mm});
            skArc(sketch, "E150.1.3", {"start": v(57.8, 29.34) * mm, "mid": v(58.14, 29.4) * mm, "end": v(58.48, 29.45) * mm});
            skLineSegment(sketch, "E150.2.0", {"start": v(54.2, 27.5) * mm, "end": v(55.06, 26.93) * mm});
            skLineSegment(sketch, "E150.2.1", {"start": v(55.58, 28.5) * mm, "end": v(55.86, 27.51) * mm});
            skArc(sketch, "E150.2.2", {"start": v(55.06, 26.93) * mm, "mid": v(55.45, 27.24) * mm, "end": v(55.86, 27.51) * mm});
            skArc(sketch, "E150.2.3", {"start": v(55.58, 28.5) * mm, "mid": v(55.88, 28.67) * mm, "end": v(56.19, 28.82) * mm});
            skLineSegment(sketch, "E150.3.0", {"start": v(52.72, 25.65) * mm, "end": v(53.71, 25.36) * mm});
            skLineSegment(sketch, "E150.3.1", {"start": v(53.72, 27.02) * mm, "end": v(54.3, 26.17) * mm});
            skArc(sketch, "E150.3.2", {"start": v(53.71, 25.36) * mm, "mid": v(54, 25.78) * mm, "end": v(54.3, 26.17) * mm});
            skArc(sketch, "E150.3.3", {"start": v(53.72, 27.02) * mm, "mid": v(53.96, 27.27) * mm, "end": v(54.2, 27.5) * mm});
            skLineSegment(sketch, "E150.4.0", {"start": v(51.88, 23.42) * mm, "end": v(52.92, 23.46) * mm});
            skLineSegment(sketch, "E150.4.1", {"start": v(52.4, 25.04) * mm, "end": v(53.22, 24.4) * mm});
            skArc(sketch, "E150.4.2", {"start": v(52.92, 23.46) * mm, "mid": v(53.05, 23.94) * mm, "end": v(53.22, 24.4) * mm});
            skArc(sketch, "E150.4.3", {"start": v(52.4, 25.04) * mm, "mid": v(52.56, 25.35) * mm, "end": v(52.72, 25.65) * mm});
            skLineSegment(sketch, "E150.5.0", {"start": v(51.78, 21.05) * mm, "end": v(52.75, 21.4) * mm});
            skLineSegment(sketch, "E150.5.1", {"start": v(51.78, 22.75) * mm, "end": v(52.75, 22.4) * mm});
            skArc(sketch, "E150.5.2", {"start": v(52.75, 21.4) * mm, "mid": v(52.73, 21.9) * mm, "end": v(52.75, 22.4) * mm});
            skArc(sketch, "E150.5.3", {"start": v(51.78, 22.75) * mm, "mid": v(51.82, 23.09) * mm, "end": v(51.88, 23.42) * mm});
            skLineSegment(sketch, "E150.6.0", {"start": v(52.4, 18.75) * mm, "end": v(53.22, 19.4) * mm});
            skLineSegment(sketch, "E150.6.1", {"start": v(51.88, 20.37) * mm, "end": v(52.92, 20.33) * mm});
            skArc(sketch, "E150.6.2", {"start": v(53.22, 19.4) * mm, "mid": v(53.05, 19.86) * mm, "end": v(52.92, 20.33) * mm});
            skArc(sketch, "E150.6.3", {"start": v(51.88, 20.37) * mm, "mid": v(51.82, 20.7) * mm, "end": v(51.78, 21.05) * mm});
            skLineSegment(sketch, "E150.7.0", {"start": v(53.72, 16.77) * mm, "end": v(54.3, 17.63) * mm});
            skLineSegment(sketch, "E150.7.1", {"start": v(52.72, 18.14) * mm, "end": v(53.71, 18.43) * mm});
            skArc(sketch, "E150.7.2", {"start": v(54.3, 17.63) * mm, "mid": v(54, 18.02) * mm, "end": v(53.71, 18.43) * mm});
            skArc(sketch, "E150.7.3", {"start": v(52.72, 18.14) * mm, "mid": v(52.56, 18.45) * mm, "end": v(52.4, 18.75) * mm});
            skLineSegment(sketch, "E150.8.0", {"start": v(55.58, 15.29) * mm, "end": v(55.86, 16.28) * mm});
            skLineSegment(sketch, "E150.8.1", {"start": v(54.2, 16.29) * mm, "end": v(55.06, 16.86) * mm});
            skArc(sketch, "E150.8.2", {"start": v(55.86, 16.28) * mm, "mid": v(55.45, 16.56) * mm, "end": v(55.06, 16.86) * mm});
            skArc(sketch, "E150.8.3", {"start": v(54.2, 16.29) * mm, "mid": v(53.96, 16.52) * mm, "end": v(53.72, 16.77) * mm});
            skLineSegment(sketch, "E150.9.0", {"start": v(57.8, 14.45) * mm, "end": v(57.77, 15.48) * mm});
            skLineSegment(sketch, "E150.9.1", {"start": v(56.19, 14.98) * mm, "end": v(56.82, 15.8) * mm});
            skArc(sketch, "E150.9.2", {"start": v(57.77, 15.48) * mm, "mid": v(57.3, 15.62) * mm, "end": v(56.82, 15.8) * mm});
            skArc(sketch, "E150.9.3", {"start": v(56.19, 14.98) * mm, "mid": v(55.88, 15.12) * mm, "end": v(55.58, 15.29) * mm});
            skLineSegment(sketch, "E150.10.0", {"start": v(60.18, 14.34) * mm, "end": v(59.83, 15.32) * mm});
            skLineSegment(sketch, "E150.10.1", {"start": v(58.48, 14.34) * mm, "end": v(58.83, 15.32) * mm});
            skArc(sketch, "E150.10.2", {"start": v(59.83, 15.32) * mm, "mid": v(59.33, 15.3) * mm, "end": v(58.83, 15.32) * mm});
            skArc(sketch, "E150.10.3", {"start": v(58.48, 14.34) * mm, "mid": v(58.14, 14.39) * mm, "end": v(57.8, 14.45) * mm});
            skLineSegment(sketch, "E150.11.0", {"start": v(62.47, 14.98) * mm, "end": v(61.84, 15.8) * mm});
            skLineSegment(sketch, "E150.11.1", {"start": v(60.86, 14.45) * mm, "end": v(60.9, 15.48) * mm});
            skArc(sketch, "E150.11.2", {"start": v(61.84, 15.8) * mm, "mid": v(61.37, 15.62) * mm, "end": v(60.9, 15.48) * mm});
            skArc(sketch, "E150.11.3", {"start": v(60.86, 14.45) * mm, "mid": v(60.52, 14.39) * mm, "end": v(60.18, 14.34) * mm});
            skLineSegment(sketch, "E150.12.0", {"start": v(64.46, 16.29) * mm, "end": v(63.6, 16.86) * mm});
            skLineSegment(sketch, "E150.12.1", {"start": v(63.08, 15.29) * mm, "end": v(62.8, 16.28) * mm});
            skArc(sketch, "E150.12.2", {"start": v(63.6, 16.86) * mm, "mid": v(63.2, 16.56) * mm, "end": v(62.8, 16.28) * mm});
            skArc(sketch, "E150.12.3", {"start": v(63.08, 15.29) * mm, "mid": v(62.78, 15.12) * mm, "end": v(62.47, 14.98) * mm});
            skLineSegment(sketch, "E150.13.0", {"start": v(65.94, 18.14) * mm, "end": v(64.95, 18.43) * mm});
            skLineSegment(sketch, "E150.13.1", {"start": v(64.94, 16.77) * mm, "end": v(64.36, 17.63) * mm});
            skArc(sketch, "E150.13.2", {"start": v(64.95, 18.43) * mm, "mid": v(64.67, 18.02) * mm, "end": v(64.36, 17.63) * mm});
            skArc(sketch, "E150.13.3", {"start": v(64.94, 16.77) * mm, "mid": v(64.7, 16.52) * mm, "end": v(64.46, 16.29) * mm});
            skLineSegment(sketch, "E150.14.0", {"start": v(66.78, 20.37) * mm, "end": v(65.74, 20.33) * mm});
            skLineSegment(sketch, "E150.14.1", {"start": v(66.25, 18.75) * mm, "end": v(65.44, 19.4) * mm});
            skArc(sketch, "E150.14.2", {"start": v(65.74, 20.33) * mm, "mid": v(65.6, 19.86) * mm, "end": v(65.44, 19.4) * mm});
            skArc(sketch, "E150.14.3", {"start": v(66.25, 18.75) * mm, "mid": v(66.1, 18.45) * mm, "end": v(65.94, 18.14) * mm});
            skLineSegment(sketch, "E150.15.0", {"start": v(66.88, 22.75) * mm, "end": v(65.91, 22.4) * mm});
            skLineSegment(sketch, "E150.15.1", {"start": v(66.88, 21.05) * mm, "end": v(65.91, 21.4) * mm});
            skArc(sketch, "E150.15.2", {"start": v(65.91, 22.4) * mm, "mid": v(65.93, 21.9) * mm, "end": v(65.91, 21.4) * mm});
            skArc(sketch, "E150.15.3", {"start": v(66.88, 21.05) * mm, "mid": v(66.84, 20.7) * mm, "end": v(66.78, 20.37) * mm});
            skLineSegment(sketch, "E150.16.0", {"start": v(66.25, 25.04) * mm, "end": v(65.44, 24.4) * mm});
            skLineSegment(sketch, "E150.16.1", {"start": v(66.78, 23.42) * mm, "end": v(65.74, 23.46) * mm});
            skArc(sketch, "E150.16.2", {"start": v(65.44, 24.4) * mm, "mid": v(65.6, 23.94) * mm, "end": v(65.74, 23.46) * mm});
            skArc(sketch, "E150.16.3", {"start": v(66.78, 23.42) * mm, "mid": v(66.84, 23.09) * mm, "end": v(66.88, 22.75) * mm});
            skLineSegment(sketch, "E150.17.0", {"start": v(64.94, 27.02) * mm, "end": v(64.36, 26.17) * mm});
            skLineSegment(sketch, "E150.17.1", {"start": v(65.94, 25.65) * mm, "end": v(64.95, 25.36) * mm});
            skArc(sketch, "E150.17.2", {"start": v(64.36, 26.17) * mm, "mid": v(64.67, 25.78) * mm, "end": v(64.95, 25.36) * mm});
            skArc(sketch, "E150.17.3", {"start": v(65.94, 25.65) * mm, "mid": v(66.1, 25.35) * mm, "end": v(66.25, 25.04) * mm});
            skLineSegment(sketch, "E150.18.0", {"start": v(63.08, 28.5) * mm, "end": v(62.8, 27.51) * mm});
            skLineSegment(sketch, "E150.18.1", {"start": v(64.46, 27.5) * mm, "end": v(63.6, 26.93) * mm});
            skArc(sketch, "E150.18.2", {"start": v(62.8, 27.51) * mm, "mid": v(63.2, 27.24) * mm, "end": v(63.6, 26.93) * mm});
            skArc(sketch, "E150.18.3", {"start": v(64.46, 27.5) * mm, "mid": v(64.7, 27.27) * mm, "end": v(64.94, 27.02) * mm});
            skLineSegment(sketch, "E150.19.0", {"start": v(60.86, 29.34) * mm, "end": v(60.9, 28.3) * mm});
            skLineSegment(sketch, "E150.19.1", {"start": v(62.47, 28.82) * mm, "end": v(61.84, 28) * mm});
            skArc(sketch, "E150.19.2", {"start": v(60.9, 28.3) * mm, "mid": v(61.37, 28.17) * mm, "end": v(61.84, 28) * mm});
            skArc(sketch, "E150.19.3", {"start": v(62.47, 28.82) * mm, "mid": v(62.78, 28.67) * mm, "end": v(63.08, 28.5) * mm});
            skSolve(sketch);
        }
        {
            var Q0;
            Q0 = qSketchRegion(id + "F75", true);
            extrude(context, id + "F76", {"entities" : qUnion([Q0]), "operationType" : NewBodyOperationType.ADD, "depth" : 3.2 * mm});
        }
        {
            var Q0;
            Q0=makeQuery(id+"F76.opExtrude","CAP_FACE",FACE,{"disambiguationData":[OSD([sQuery(id+"F75.wireOp",EDGE,"E145"),sQuery(id+"F75.wireOp",EDGE,"E146.0"),sQuery(id+"F75.wireOp",EDGE,"E147.0"),sQuery(id+"F75.wireOp",EDGE,"E148.0"),sQuery(id+"F75.wireOp",EDGE,"E149.0"),sQuery(id+"F75.wireOp",EDGE,"E150.1.0"),sQuery(id+"F75.wireOp",EDGE,"E150.1.1"),sQuery(id+"F75.wireOp",EDGE,"E150.1.2"),sQuery(id+"F75.wireOp",EDGE,"E150.1.3"),sQuery(id+"F75.wireOp",EDGE,"E150.2.0"),sQuery(id+"F75.wireOp",EDGE,"E150.2.1"),sQuery(id+"F75.wireOp",EDGE,"E150.2.2"),sQuery(id+"F75.wireOp",EDGE,"E150.2.3"),sQuery(id+"F75.wireOp",EDGE,"E150.3.0"),sQuery(id+"F75.wireOp",EDGE,"E150.3.1"),sQuery(id+"F75.wireOp",EDGE,"E150.3.2"),sQuery(id+"F75.wireOp",EDGE,"E150.3.3"),sQuery(id+"F75.wireOp",EDGE,"E150.4.0"),sQuery(id+"F75.wireOp",EDGE,"E150.4.1"),sQuery(id+"F75.wireOp",EDGE,"E150.4.2"),sQuery(id+"F75.wireOp",EDGE,"E150.4.3"),sQuery(id+"F75.wireOp",EDGE,"E150.5.0"),sQuery(id+"F75.wireOp",EDGE,"E150.5.1"),sQuery(id+"F75.wireOp",EDGE,"E150.5.2"),sQuery(id+"F75.wireOp",EDGE,"E150.5.3"),sQuery(id+"F75.wireOp",EDGE,"E150.6.0"),sQuery(id+"F75.wireOp",EDGE,"E150.6.1"),sQuery(id+"F75.wireOp",EDGE,"E150.6.2"),sQuery(id+"F75.wireOp",EDGE,"E150.6.3"),sQuery(id+"F75.wireOp",EDGE,"E150.7.0"),sQuery(id+"F75.wireOp",EDGE,"E150.7.1"),sQuery(id+"F75.wireOp",EDGE,"E150.7.2"),sQuery(id+"F75.wireOp",EDGE,"E150.7.3"),sQuery(id+"F75.wireOp",EDGE,"E150.8.0"),sQuery(id+"F75.wireOp",EDGE,"E150.8.1"),sQuery(id+"F75.wireOp",EDGE,"E150.8.2"),sQuery(id+"F75.wireOp",EDGE,"E150.8.3"),sQuery(id+"F75.wireOp",EDGE,"E150.9.0"),sQuery(id+"F75.wireOp",EDGE,"E150.9.1"),sQuery(id+"F75.wireOp",EDGE,"E150.9.2"),sQuery(id+"F75.wireOp",EDGE,"E150.9.3"),sQuery(id+"F75.wireOp",EDGE,"E150.10.0"),sQuery(id+"F75.wireOp",EDGE,"E150.10.1"),sQuery(id+"F75.wireOp",EDGE,"E150.10.2"),sQuery(id+"F75.wireOp",EDGE,"E150.10.3"),sQuery(id+"F75.wireOp",EDGE,"E150.11.0"),sQuery(id+"F75.wireOp",EDGE,"E150.11.1"),sQuery(id+"F75.wireOp",EDGE,"E150.11.2"),sQuery(id+"F75.wireOp",EDGE,"E150.11.3"),sQuery(id+"F75.wireOp",EDGE,"E150.12.0"),sQuery(id+"F75.wireOp",EDGE,"E150.12.1"),sQuery(id+"F75.wireOp",EDGE,"E150.12.2"),sQuery(id+"F75.wireOp",EDGE,"E150.12.3"),sQuery(id+"F75.wireOp",EDGE,"E150.13.0"),sQuery(id+"F75.wireOp",EDGE,"E150.13.1"),sQuery(id+"F75.wireOp",EDGE,"E150.13.2"),sQuery(id+"F75.wireOp",EDGE,"E150.13.3"),sQuery(id+"F75.wireOp",EDGE,"E150.14.0"),sQuery(id+"F75.wireOp",EDGE,"E150.14.1"),sQuery(id+"F75.wireOp",EDGE,"E150.14.2"),sQuery(id+"F75.wireOp",EDGE,"E150.14.3"),sQuery(id+"F75.wireOp",EDGE,"E150.15.0"),sQuery(id+"F75.wireOp",EDGE,"E150.15.1"),sQuery(id+"F75.wireOp",EDGE,"E150.15.2"),sQuery(id+"F75.wireOp",EDGE,"E150.15.3"),sQuery(id+"F75.wireOp",EDGE,"E150.16.0"),sQuery(id+"F75.wireOp",EDGE,"E150.16.1"),sQuery(id+"F75.wireOp",EDGE,"E150.16.2"),sQuery(id+"F75.wireOp",EDGE,"E150.16.3"),sQuery(id+"F75.wireOp",EDGE,"E150.17.0"),sQuery(id+"F75.wireOp",EDGE,"E150.17.1"),sQuery(id+"F75.wireOp",EDGE,"E150.17.2"),sQuery(id+"F75.wireOp",EDGE,"E150.17.3"),sQuery(id+"F75.wireOp",EDGE,"E150.18.0"),sQuery(id+"F75.wireOp",EDGE,"E150.18.1"),sQuery(id+"F75.wireOp",EDGE,"E150.18.2"),sQuery(id+"F75.wireOp",EDGE,"E150.18.3"),sQuery(id+"F75.wireOp",EDGE,"E150.19.0"),sQuery(id+"F75.wireOp",EDGE,"E150.19.1"),sQuery(id+"F75.wireOp",EDGE,"E150.19.2"),sQuery(id+"F75.wireOp",EDGE,"E150.19.3")])],"isStart":false});
            var sketch = newSketch(context, id + "F77", { "sketchPlane" : qUnion([Q0])});
            skCircle(sketch, "E151", {"center": v(59.33, 21.9) * mm, "radius": 5.7 * mm});
            skCircle(sketch, "E152.0", {"center": v(59.33, 21.9) * mm, "radius": 9 * mm});
            skSolve(sketch);
        }
        {
            var Q0;
            Q0 = qSketchRegion(id + "F77", true);
            extrude(context, id + "F78", {"entities" : qUnion([Q0]), "operationType" : NewBodyOperationType.ADD, "depth" : 1 * mm});
        }
        {
            var Q0;
            Q0=makeQuery(id+"F74.opExtrude","CAP_EDGE",EDGE,{"disambiguationData":[OSD([sQuery(id+"F73.wireOp",EDGE,"E144")])],"isStart":false});
            chamfer(context, id + "F79", {"entities" : qUnion([Q0]), "width" : 1.6 * mm, "tangentPropagation" : true});
        }
        {
            var Q0;
            Q0=makeQuery(id+"F70.opExtrude","CAP_EDGE",EDGE,{"disambiguationData":[OSD([sQuery(id+"F69.wireOp",EDGE,"E127")])],"isStart":true});
            var Q1;
            Q1=makeQuery(id+"F78.opExtrude","CAP_EDGE",EDGE,{"disambiguationData":[OSD([sQuery(id+"F77.wireOp",EDGE,"E152.0")])],"isStart":true});
            chamfer(context, id + "F80", {"entities" : qUnion([Q0, Q1]), "width" : 0.8 * mm, "tangentPropagation" : true});
        }
        {
            var Q0;
            Q0=makeQuery(id+"F70.opExtrude","CAP_EDGE",EDGE,{"disambiguationData":[OSD([sQuery(id+"F69.wireOp",EDGE,"E128")])],"isStart":false});
            var Q1;
            Q1=makeQuery(id+"F78.opExtrude","CAP_EDGE",EDGE,{"disambiguationData":[OSD([sQuery(id+"F77.wireOp",EDGE,"E151")])],"isStart":false});
            chamfer(context, id + "F81", {"entities" : qUnion([Q0, Q1]), "width" : 0.4 * mm, "tangentPropagation" : true});
        }
        {
            var Q0;
            Q0=qCreatedBy(makeId("Top.planeOp"),FACE);
            var sketch = newSketch(context, id + "F82", { "sketchPlane" : qUnion([Q0])});
            skCircle(sketch, "E153", {"center": v(28.46, 0) * mm, "radius": 16 * mm});
            skCircle(sketch, "E154", {"center": v(28.46, 0) * mm, "radius": 5.7 * mm});
            skSolve(sketch);
        }
        {
            var Q0;
            Q0 = qSketchRegion(id + "F82", true);
            extrude(context, id + "F83", {"entities" : qUnion([Q0]), "depth" : 1 * mm});
        }
        {
            var Q0;
            Q0=makeQuery(id+"F83.opExtrude","CAP_FACE",FACE,{"disambiguationData":[OSD([sQuery(id+"F82.wireOp",EDGE,"E153"),sQuery(id+"F82.wireOp",EDGE,"E154")])],"isStart":false});
            var sketch = newSketch(context, id + "F84", { "sketchPlane" : qUnion([Q0])});
            skCircle(sketch, "E155", {"center": v(28.46, 0) * mm, "radius": 5.1 * mm});
            skCircle(sketch, "E156", {"center": v(28.46, 0) * mm, "radius": 14.85 * mm, "construction": true});
            skLineSegment(sketch, "E157", {"start": v(28.46, 0) * mm, "end": v(28.46, 14.85) * mm, "construction": true});
            skCircle(sketch, "E158.0", {"center": v(28.46, 0) * mm, "radius": 13.85 * mm, "construction": true});
            skCircle(sketch, "E159", {"center": v(28.46, 14.56) * mm, "radius": 0.7 * mm, "construction": true});
            skLineSegment(sketch, "E160", {"start": v(28.46, 0) * mm, "end": v(27.74, 14.83) * mm, "construction": true});
            skLineSegment(sketch, "E161.MirrorCS", {"start": v(28.46, 0) * mm, "end": v(29.17, 14.83) * mm, "construction": true});
            skArc(sketch, "E162", {"start": v(27.75, 14.52) * mm, "mid": v(28.46, 13.85) * mm, "end": v(29.16, 14.52) * mm});
            skCircle(sketch, "E163.1.0", {"center": v(26.56, 14.43) * mm, "radius": 0.7 * mm, "construction": true});
            skCircle(sketch, "E163.2.0", {"center": v(24.69, 14.06) * mm, "radius": 0.7 * mm, "construction": true});
            skCircle(sketch, "E163.3.0", {"center": v(22.89, 13.45) * mm, "radius": 0.7 * mm, "construction": true});
            skCircle(sketch, "E163.4.0", {"center": v(21.18, 12.6) * mm, "radius": 0.7 * mm, "construction": true});
            skCircle(sketch, "E163.5.0", {"center": v(19.6, 11.55) * mm, "radius": 0.7 * mm, "construction": true});
            skCircle(sketch, "E163.6.0", {"center": v(18.16, 10.3) * mm, "radius": 0.7 * mm, "construction": true});
            skCircle(sketch, "E163.7.0", {"center": v(16.9, 8.86) * mm, "radius": 0.7 * mm, "construction": true});
            skCircle(sketch, "E163.8.0", {"center": v(15.85, 7.28) * mm, "radius": 0.7 * mm, "construction": true});
            skCircle(sketch, "E163.9.0", {"center": v(15, 5.57) * mm, "radius": 0.7 * mm, "construction": true});
            skCircle(sketch, "E163.10.0", {"center": v(14.4, 3.77) * mm, "radius": 0.7 * mm, "construction": true});
            skCircle(sketch, "E163.11.0", {"center": v(14.02, 1.9) * mm, "radius": 0.7 * mm, "construction": true});
            skCircle(sketch, "E163.12.0", {"center": v(13.9, 0) * mm, "radius": 0.7 * mm, "construction": true});
            skCircle(sketch, "E163.13.0", {"center": v(14.02, -1.9) * mm, "radius": 0.7 * mm, "construction": true});
            skCircle(sketch, "E163.14.0", {"center": v(14.4, -3.77) * mm, "radius": 0.7 * mm, "construction": true});
            skCircle(sketch, "E163.15.0", {"center": v(15, -5.57) * mm, "radius": 0.7 * mm, "construction": true});
            skCircle(sketch, "E163.16.0", {"center": v(15.85, -7.28) * mm, "radius": 0.7 * mm, "construction": true});
            skCircle(sketch, "E163.17.0", {"center": v(16.9, -8.86) * mm, "radius": 0.7 * mm, "construction": true});
            skCircle(sketch, "E163.18.0", {"center": v(18.16, -10.3) * mm, "radius": 0.7 * mm, "construction": true});
            skCircle(sketch, "E163.19.0", {"center": v(19.6, -11.55) * mm, "radius": 0.7 * mm, "construction": true});
            skCircle(sketch, "E163.20.0", {"center": v(21.18, -12.6) * mm, "radius": 0.7 * mm, "construction": true});
            skCircle(sketch, "E163.21.0", {"center": v(22.89, -13.45) * mm, "radius": 0.7 * mm, "construction": true});
            skCircle(sketch, "E163.22.0", {"center": v(24.69, -14.06) * mm, "radius": 0.7 * mm, "construction": true});
            skCircle(sketch, "E163.23.0", {"center": v(26.56, -14.43) * mm, "radius": 0.7 * mm, "construction": true});
            skCircle(sketch, "E163.24.0", {"center": v(28.46, -14.56) * mm, "radius": 0.7 * mm, "construction": true});
            skCircle(sketch, "E163.25.0", {"center": v(30.35, -14.43) * mm, "radius": 0.7 * mm, "construction": true});
            skCircle(sketch, "E163.26.0", {"center": v(32.22, -14.06) * mm, "radius": 0.7 * mm, "construction": true});
            skCircle(sketch, "E163.27.0", {"center": v(34.02, -13.45) * mm, "radius": 0.7 * mm, "construction": true});
            skCircle(sketch, "E163.28.0", {"center": v(35.73, -12.6) * mm, "radius": 0.7 * mm, "construction": true});
            skCircle(sketch, "E163.29.0", {"center": v(37.32, -11.55) * mm, "radius": 0.7 * mm, "construction": true});
            skCircle(sketch, "E163.30.0", {"center": v(38.75, -10.3) * mm, "radius": 0.7 * mm, "construction": true});
            skCircle(sketch, "E163.31.0", {"center": v(40, -8.86) * mm, "radius": 0.7 * mm, "construction": true});
            skCircle(sketch, "E163.32.0", {"center": v(41.06, -7.28) * mm, "radius": 0.7 * mm, "construction": true});
            skCircle(sketch, "E163.33.0", {"center": v(41.9, -5.57) * mm, "radius": 0.7 * mm, "construction": true});
            skCircle(sketch, "E163.34.0", {"center": v(42.51, -3.77) * mm, "radius": 0.7 * mm, "construction": true});
            skCircle(sketch, "E163.35.0", {"center": v(42.89, -1.9) * mm, "radius": 0.7 * mm, "construction": true});
            skCircle(sketch, "E163.36.0", {"center": v(43.01, 0) * mm, "radius": 0.7 * mm, "construction": true});
            skCircle(sketch, "E163.37.0", {"center": v(42.89, 1.9) * mm, "radius": 0.7 * mm, "construction": true});
            skCircle(sketch, "E163.38.0", {"center": v(42.51, 3.77) * mm, "radius": 0.7 * mm, "construction": true});
            skCircle(sketch, "E163.39.0", {"center": v(41.9, 5.57) * mm, "radius": 0.7 * mm, "construction": true});
            skCircle(sketch, "E163.40.0", {"center": v(41.06, 7.28) * mm, "radius": 0.7 * mm, "construction": true});
            skCircle(sketch, "E163.41.0", {"center": v(40, 8.86) * mm, "radius": 0.7 * mm, "construction": true});
            skCircle(sketch, "E163.42.0", {"center": v(38.75, 10.3) * mm, "radius": 0.7 * mm, "construction": true});
            skCircle(sketch, "E163.43.0", {"center": v(37.32, 11.55) * mm, "radius": 0.7 * mm, "construction": true});
            skCircle(sketch, "E163.44.0", {"center": v(35.73, 12.6) * mm, "radius": 0.7 * mm, "construction": true});
            skCircle(sketch, "E163.45.0", {"center": v(34.02, 13.45) * mm, "radius": 0.7 * mm, "construction": true});
            skCircle(sketch, "E163.46.0", {"center": v(32.22, 14.06) * mm, "radius": 0.7 * mm, "construction": true});
            skCircle(sketch, "E163.47.0", {"center": v(30.35, 14.43) * mm, "radius": 0.7 * mm, "construction": true});
            skLineSegment(sketch, "E164", {"start": v(28.46, 0) * mm, "end": v(29.68, 14.8) * mm, "construction": true});
            skArc(sketch, "E165", {"start": v(29.66, 14.55) * mm, "mid": v(29.43, 14.82) * mm, "end": v(29.16, 14.58) * mm});
            skLineSegment(sketch, "E166", {"start": v(29.16, 14.58) * mm, "end": v(29.16, 14.52) * mm});
            skLineSegment(sketch, "E167.MirrorCS", {"start": v(27.75, 14.58) * mm, "end": v(27.75, 14.52) * mm});
            skArc(sketch, "E168.1.0", {"start": v(25.86, 14.3) * mm, "mid": v(26.65, 13.73) * mm, "end": v(27.26, 14.49) * mm});
            skLineSegment(sketch, "E168.1.1", {"start": v(25.85, 14.37) * mm, "end": v(25.86, 14.3) * mm});
            skArc(sketch, "E168.1.2", {"start": v(27.75, 14.58) * mm, "mid": v(27.48, 14.82) * mm, "end": v(27.25, 14.55) * mm});
            skLineSegment(sketch, "E168.1.3", {"start": v(27.25, 14.55) * mm, "end": v(27.26, 14.49) * mm});
            skArc(sketch, "E168.2.0", {"start": v(24.02, 13.84) * mm, "mid": v(24.87, 13.38) * mm, "end": v(25.38, 14.2) * mm});
            skLineSegment(sketch, "E168.2.1", {"start": v(24, 13.9) * mm, "end": v(24.02, 13.84) * mm});
            skArc(sketch, "E168.2.2", {"start": v(25.85, 14.37) * mm, "mid": v(25.56, 14.56) * mm, "end": v(25.36, 14.27) * mm});
            skLineSegment(sketch, "E168.2.3", {"start": v(25.36, 14.27) * mm, "end": v(25.38, 14.2) * mm});
            skArc(sketch, "E168.3.0", {"start": v(22.25, 13.15) * mm, "mid": v(23.15, 12.8) * mm, "end": v(23.55, 13.68) * mm});
            skLineSegment(sketch, "E168.3.1", {"start": v(22.22, 13.2) * mm, "end": v(22.25, 13.15) * mm});
            skArc(sketch, "E168.3.2", {"start": v(24, 13.9) * mm, "mid": v(23.68, 14.06) * mm, "end": v(23.53, 13.74) * mm});
            skLineSegment(sketch, "E168.3.3", {"start": v(23.53, 13.74) * mm, "end": v(23.55, 13.68) * mm});
            skArc(sketch, "E168.4.0", {"start": v(20.58, 12.22) * mm, "mid": v(21.53, 12) * mm, "end": v(21.8, 12.93) * mm});
            skLineSegment(sketch, "E168.4.1", {"start": v(20.55, 12.28) * mm, "end": v(20.58, 12.22) * mm});
            skArc(sketch, "E168.4.2", {"start": v(22.22, 13.2) * mm, "mid": v(21.89, 13.32) * mm, "end": v(21.78, 12.98) * mm});
            skLineSegment(sketch, "E168.4.3", {"start": v(21.78, 12.98) * mm, "end": v(21.8, 12.93) * mm});
            skArc(sketch, "E168.5.0", {"start": v(19.06, 11.1) * mm, "mid": v(20.02, 10.99) * mm, "end": v(20.17, 11.95) * mm});
            skLineSegment(sketch, "E168.5.1", {"start": v(19.02, 11.14) * mm, "end": v(19.06, 11.1) * mm});
            skArc(sketch, "E168.5.2", {"start": v(20.55, 12.28) * mm, "mid": v(20.2, 12.35) * mm, "end": v(20.14, 12) * mm});
            skLineSegment(sketch, "E168.5.3", {"start": v(20.14, 12) * mm, "end": v(20.17, 11.95) * mm});
            skArc(sketch, "E168.6.0", {"start": v(17.69, 9.77) * mm, "mid": v(18.66, 9.8) * mm, "end": v(18.69, 10.77) * mm});
            skLineSegment(sketch, "E168.6.1", {"start": v(17.64, 9.81) * mm, "end": v(17.69, 9.77) * mm});
            skArc(sketch, "E168.6.2", {"start": v(19.02, 11.14) * mm, "mid": v(18.66, 11.16) * mm, "end": v(18.64, 10.81) * mm});
            skLineSegment(sketch, "E168.6.3", {"start": v(18.64, 10.81) * mm, "end": v(18.69, 10.77) * mm});
            skArc(sketch, "E168.7.0", {"start": v(16.5, 8.28) * mm, "mid": v(17.47, 8.43) * mm, "end": v(17.36, 9.4) * mm});
            skLineSegment(sketch, "E168.7.1", {"start": v(16.46, 8.32) * mm, "end": v(16.5, 8.28) * mm});
            skArc(sketch, "E168.7.2", {"start": v(17.64, 9.81) * mm, "mid": v(17.3, 9.8) * mm, "end": v(17.32, 9.44) * mm});
            skLineSegment(sketch, "E168.7.3", {"start": v(17.32, 9.44) * mm, "end": v(17.36, 9.4) * mm});
            skArc(sketch, "E168.8.0", {"start": v(15.53, 6.65) * mm, "mid": v(16.46, 6.92) * mm, "end": v(16.23, 7.87) * mm});
            skLineSegment(sketch, "E168.8.1", {"start": v(15.47, 6.68) * mm, "end": v(15.53, 6.65) * mm});
            skArc(sketch, "E168.8.2", {"start": v(16.46, 8.32) * mm, "mid": v(16.1, 8.25) * mm, "end": v(16.18, 7.9) * mm});
            skLineSegment(sketch, "E168.8.3", {"start": v(16.18, 7.9) * mm, "end": v(16.23, 7.87) * mm});
            skArc(sketch, "E168.9.0", {"start": v(14.77, 4.9) * mm, "mid": v(15.66, 5.3) * mm, "end": v(15.3, 6.2) * mm});
            skLineSegment(sketch, "E168.9.1", {"start": v(14.71, 4.93) * mm, "end": v(14.77, 4.9) * mm});
            skArc(sketch, "E168.9.2", {"start": v(15.47, 6.68) * mm, "mid": v(15.14, 6.57) * mm, "end": v(15.25, 6.23) * mm});
            skLineSegment(sketch, "E168.9.3", {"start": v(15.25, 6.23) * mm, "end": v(15.3, 6.2) * mm});
            skArc(sketch, "E168.10.0", {"start": v(14.25, 3.08) * mm, "mid": v(15.08, 3.58) * mm, "end": v(14.61, 4.44) * mm});
            skLineSegment(sketch, "E168.10.1", {"start": v(14.19, 3.1) * mm, "end": v(14.25, 3.08) * mm});
            skArc(sketch, "E168.10.2", {"start": v(14.71, 4.93) * mm, "mid": v(14.4, 4.77) * mm, "end": v(14.55, 4.46) * mm});
            skLineSegment(sketch, "E168.10.3", {"start": v(14.55, 4.46) * mm, "end": v(14.61, 4.44) * mm});
            skArc(sketch, "E168.11.0", {"start": v(13.97, 1.2) * mm, "mid": v(14.72, 1.8) * mm, "end": v(14.15, 2.6) * mm});
            skLineSegment(sketch, "E168.11.1", {"start": v(13.9, 1.2) * mm, "end": v(13.97, 1.2) * mm});
            skArc(sketch, "E168.11.2", {"start": v(14.19, 3.1) * mm, "mid": v(13.9, 2.9) * mm, "end": v(14.09, 2.6) * mm});
            skLineSegment(sketch, "E168.11.3", {"start": v(14.09, 2.6) * mm, "end": v(14.15, 2.6) * mm});
            skArc(sketch, "E168.12.0", {"start": v(13.93, -0.7) * mm, "mid": v(14.6, 0) * mm, "end": v(13.93, 0.7) * mm});
            skLineSegment(sketch, "E168.12.1", {"start": v(13.87, -0.7) * mm, "end": v(13.93, -0.7) * mm});
            skArc(sketch, "E168.12.2", {"start": v(13.9, 1.2) * mm, "mid": v(13.64, 0.97) * mm, "end": v(13.87, 0.7) * mm});
            skLineSegment(sketch, "E168.12.3", {"start": v(13.87, 0.7) * mm, "end": v(13.93, 0.7) * mm});
            skArc(sketch, "E168.13.0", {"start": v(14.15, -2.6) * mm, "mid": v(14.72, -1.8) * mm, "end": v(13.97, -1.2) * mm});
            skLineSegment(sketch, "E168.13.1", {"start": v(14.09, -2.6) * mm, "end": v(14.15, -2.6) * mm});
            skArc(sketch, "E168.13.2", {"start": v(13.87, -0.7) * mm, "mid": v(13.64, -0.97) * mm, "end": v(13.9, -1.2) * mm});
            skLineSegment(sketch, "E168.13.3", {"start": v(13.9, -1.2) * mm, "end": v(13.97, -1.2) * mm});
            skArc(sketch, "E168.14.0", {"start": v(14.61, -4.44) * mm, "mid": v(15.08, -3.58) * mm, "end": v(14.25, -3.08) * mm});
            skLineSegment(sketch, "E168.14.1", {"start": v(14.55, -4.46) * mm, "end": v(14.61, -4.44) * mm});
            skArc(sketch, "E168.14.2", {"start": v(14.09, -2.6) * mm, "mid": v(13.9, -2.9) * mm, "end": v(14.19, -3.1) * mm});
            skLineSegment(sketch, "E168.14.3", {"start": v(14.19, -3.1) * mm, "end": v(14.25, -3.08) * mm});
            skArc(sketch, "E168.15.0", {"start": v(15.3, -6.2) * mm, "mid": v(15.66, -5.3) * mm, "end": v(14.77, -4.9) * mm});
            skLineSegment(sketch, "E168.15.1", {"start": v(15.25, -6.23) * mm, "end": v(15.3, -6.2) * mm});
            skArc(sketch, "E168.15.2", {"start": v(14.55, -4.46) * mm, "mid": v(14.4, -4.77) * mm, "end": v(14.71, -4.93) * mm});
            skLineSegment(sketch, "E168.15.3", {"start": v(14.71, -4.93) * mm, "end": v(14.77, -4.9) * mm});
            skArc(sketch, "E168.16.0", {"start": v(16.23, -7.87) * mm, "mid": v(16.46, -6.93) * mm, "end": v(15.53, -6.65) * mm});
            skLineSegment(sketch, "E168.16.1", {"start": v(16.18, -7.9) * mm, "end": v(16.23, -7.87) * mm});
            skArc(sketch, "E168.16.2", {"start": v(15.25, -6.23) * mm, "mid": v(15.14, -6.57) * mm, "end": v(15.47, -6.68) * mm});
            skLineSegment(sketch, "E168.16.3", {"start": v(15.47, -6.68) * mm, "end": v(15.53, -6.65) * mm});
            skArc(sketch, "E168.17.0", {"start": v(17.36, -9.4) * mm, "mid": v(17.47, -8.43) * mm, "end": v(16.5, -8.28) * mm});
            skLineSegment(sketch, "E168.17.1", {"start": v(17.32, -9.44) * mm, "end": v(17.36, -9.4) * mm});
            skArc(sketch, "E168.17.2", {"start": v(16.18, -7.9) * mm, "mid": v(16.1, -8.25) * mm, "end": v(16.46, -8.32) * mm});
            skLineSegment(sketch, "E168.17.3", {"start": v(16.46, -8.32) * mm, "end": v(16.5, -8.28) * mm});
            skArc(sketch, "E168.18.0", {"start": v(18.69, -10.77) * mm, "mid": v(18.66, -9.8) * mm, "end": v(17.69, -9.77) * mm});
            skLineSegment(sketch, "E168.18.1", {"start": v(18.64, -10.81) * mm, "end": v(18.69, -10.77) * mm});
            skArc(sketch, "E168.18.2", {"start": v(17.32, -9.44) * mm, "mid": v(17.3, -9.8) * mm, "end": v(17.64, -9.81) * mm});
            skLineSegment(sketch, "E168.18.3", {"start": v(17.64, -9.81) * mm, "end": v(17.69, -9.77) * mm});
            skArc(sketch, "E168.19.0", {"start": v(20.17, -11.95) * mm, "mid": v(20.02, -10.99) * mm, "end": v(19.06, -11.1) * mm});
            skLineSegment(sketch, "E168.19.1", {"start": v(20.14, -12) * mm, "end": v(20.17, -11.95) * mm});
            skArc(sketch, "E168.19.2", {"start": v(18.64, -10.81) * mm, "mid": v(18.66, -11.16) * mm, "end": v(19.02, -11.14) * mm});
            skLineSegment(sketch, "E168.19.3", {"start": v(19.02, -11.14) * mm, "end": v(19.06, -11.1) * mm});
            skArc(sketch, "E168.20.0", {"start": v(21.8, -12.93) * mm, "mid": v(21.53, -12) * mm, "end": v(20.58, -12.22) * mm});
            skLineSegment(sketch, "E168.20.1", {"start": v(21.78, -12.98) * mm, "end": v(21.8, -12.93) * mm});
            skArc(sketch, "E168.20.2", {"start": v(20.14, -12) * mm, "mid": v(20.2, -12.35) * mm, "end": v(20.55, -12.28) * mm});
            skLineSegment(sketch, "E168.20.3", {"start": v(20.55, -12.28) * mm, "end": v(20.58, -12.22) * mm});
            skArc(sketch, "E168.21.0", {"start": v(23.55, -13.68) * mm, "mid": v(23.15, -12.8) * mm, "end": v(22.25, -13.15) * mm});
            skLineSegment(sketch, "E168.21.1", {"start": v(23.53, -13.74) * mm, "end": v(23.55, -13.68) * mm});
            skArc(sketch, "E168.21.2", {"start": v(21.78, -12.98) * mm, "mid": v(21.89, -13.32) * mm, "end": v(22.22, -13.2) * mm});
            skLineSegment(sketch, "E168.21.3", {"start": v(22.22, -13.2) * mm, "end": v(22.25, -13.15) * mm});
            skArc(sketch, "E168.22.0", {"start": v(25.38, -14.2) * mm, "mid": v(24.87, -13.38) * mm, "end": v(24.02, -13.84) * mm});
            skLineSegment(sketch, "E168.22.1", {"start": v(25.36, -14.27) * mm, "end": v(25.38, -14.2) * mm});
            skArc(sketch, "E168.22.2", {"start": v(23.53, -13.74) * mm, "mid": v(23.68, -14.06) * mm, "end": v(24, -13.9) * mm});
            skLineSegment(sketch, "E168.22.3", {"start": v(24, -13.9) * mm, "end": v(24.02, -13.84) * mm});
            skArc(sketch, "E168.23.0", {"start": v(27.26, -14.49) * mm, "mid": v(26.65, -13.73) * mm, "end": v(25.86, -14.3) * mm});
            skLineSegment(sketch, "E168.23.1", {"start": v(27.25, -14.55) * mm, "end": v(27.26, -14.49) * mm});
            skArc(sketch, "E168.23.2", {"start": v(25.36, -14.27) * mm, "mid": v(25.56, -14.56) * mm, "end": v(25.85, -14.37) * mm});
            skLineSegment(sketch, "E168.23.3", {"start": v(25.85, -14.37) * mm, "end": v(25.86, -14.3) * mm});
            skArc(sketch, "E168.24.0", {"start": v(29.16, -14.52) * mm, "mid": v(28.46, -13.85) * mm, "end": v(27.75, -14.52) * mm});
            skLineSegment(sketch, "E168.24.1", {"start": v(29.16, -14.58) * mm, "end": v(29.16, -14.52) * mm});
            skArc(sketch, "E168.24.2", {"start": v(27.25, -14.55) * mm, "mid": v(27.48, -14.82) * mm, "end": v(27.75, -14.58) * mm});
            skLineSegment(sketch, "E168.24.3", {"start": v(27.75, -14.58) * mm, "end": v(27.75, -14.52) * mm});
            skArc(sketch, "E168.25.0", {"start": v(31.05, -14.3) * mm, "mid": v(30.26, -13.73) * mm, "end": v(29.65, -14.49) * mm});
            skLineSegment(sketch, "E168.25.1", {"start": v(31.06, -14.37) * mm, "end": v(31.05, -14.3) * mm});
            skArc(sketch, "E168.25.2", {"start": v(29.16, -14.58) * mm, "mid": v(29.43, -14.82) * mm, "end": v(29.66, -14.55) * mm});
            skLineSegment(sketch, "E168.25.3", {"start": v(29.66, -14.55) * mm, "end": v(29.65, -14.49) * mm});
            skArc(sketch, "E168.26.0", {"start": v(32.9, -13.84) * mm, "mid": v(32.04, -13.38) * mm, "end": v(31.53, -14.2) * mm});
            skLineSegment(sketch, "E168.26.1", {"start": v(32.91, -13.9) * mm, "end": v(32.9, -13.84) * mm});
            skArc(sketch, "E168.26.2", {"start": v(31.06, -14.37) * mm, "mid": v(31.35, -14.56) * mm, "end": v(31.55, -14.27) * mm});
            skLineSegment(sketch, "E168.26.3", {"start": v(31.55, -14.27) * mm, "end": v(31.53, -14.2) * mm});
            skArc(sketch, "E168.27.0", {"start": v(34.66, -13.15) * mm, "mid": v(33.76, -12.8) * mm, "end": v(33.36, -13.68) * mm});
            skLineSegment(sketch, "E168.27.1", {"start": v(34.69, -13.2) * mm, "end": v(34.66, -13.15) * mm});
            skArc(sketch, "E168.27.2", {"start": v(32.91, -13.9) * mm, "mid": v(33.23, -14.06) * mm, "end": v(33.38, -13.74) * mm});
            skLineSegment(sketch, "E168.27.3", {"start": v(33.38, -13.74) * mm, "end": v(33.36, -13.68) * mm});
            skArc(sketch, "E168.28.0", {"start": v(36.33, -12.22) * mm, "mid": v(35.38, -12) * mm, "end": v(35.1, -12.93) * mm});
            skLineSegment(sketch, "E168.28.1", {"start": v(36.36, -12.28) * mm, "end": v(36.33, -12.22) * mm});
            skArc(sketch, "E168.28.2", {"start": v(34.69, -13.2) * mm, "mid": v(35.02, -13.32) * mm, "end": v(35.13, -12.98) * mm});
            skLineSegment(sketch, "E168.28.3", {"start": v(35.13, -12.98) * mm, "end": v(35.1, -12.93) * mm});
            skArc(sketch, "E168.29.0", {"start": v(37.85, -11.1) * mm, "mid": v(36.89, -10.99) * mm, "end": v(36.74, -11.95) * mm});
            skLineSegment(sketch, "E168.29.1", {"start": v(37.9, -11.14) * mm, "end": v(37.85, -11.1) * mm});
            skArc(sketch, "E168.29.2", {"start": v(36.36, -12.28) * mm, "mid": v(36.7, -12.35) * mm, "end": v(36.77, -12) * mm});
            skLineSegment(sketch, "E168.29.3", {"start": v(36.77, -12) * mm, "end": v(36.74, -11.95) * mm});
            skArc(sketch, "E168.30.0", {"start": v(39.22, -9.77) * mm, "mid": v(38.25, -9.8) * mm, "end": v(38.22, -10.77) * mm});
            skLineSegment(sketch, "E168.30.1", {"start": v(39.27, -9.81) * mm, "end": v(39.22, -9.77) * mm});
            skArc(sketch, "E168.30.2", {"start": v(37.9, -11.14) * mm, "mid": v(38.25, -11.16) * mm, "end": v(38.27, -10.81) * mm});
            skLineSegment(sketch, "E168.30.3", {"start": v(38.27, -10.81) * mm, "end": v(38.22, -10.77) * mm});
            skArc(sketch, "E168.31.0", {"start": v(40.4, -8.28) * mm, "mid": v(39.44, -8.43) * mm, "end": v(39.55, -9.4) * mm});
            skLineSegment(sketch, "E168.31.1", {"start": v(40.45, -8.32) * mm, "end": v(40.4, -8.28) * mm});
            skArc(sketch, "E168.31.2", {"start": v(39.27, -9.81) * mm, "mid": v(39.62, -9.8) * mm, "end": v(39.6, -9.44) * mm});
            skLineSegment(sketch, "E168.31.3", {"start": v(39.6, -9.44) * mm, "end": v(39.55, -9.4) * mm});
            skArc(sketch, "E168.32.0", {"start": v(41.38, -6.65) * mm, "mid": v(40.45, -6.92) * mm, "end": v(40.68, -7.87) * mm});
            skLineSegment(sketch, "E168.32.1", {"start": v(41.44, -6.68) * mm, "end": v(41.38, -6.65) * mm});
            skArc(sketch, "E168.32.2", {"start": v(40.45, -8.32) * mm, "mid": v(40.8, -8.25) * mm, "end": v(40.73, -7.9) * mm});
            skLineSegment(sketch, "E168.32.3", {"start": v(40.73, -7.9) * mm, "end": v(40.68, -7.87) * mm});
            skArc(sketch, "E168.33.0", {"start": v(42.14, -4.9) * mm, "mid": v(41.25, -5.3) * mm, "end": v(41.6, -6.2) * mm});
            skLineSegment(sketch, "E168.33.1", {"start": v(42.2, -4.93) * mm, "end": v(42.14, -4.9) * mm});
            skArc(sketch, "E168.33.2", {"start": v(41.44, -6.68) * mm, "mid": v(41.77, -6.57) * mm, "end": v(41.66, -6.23) * mm});
            skLineSegment(sketch, "E168.33.3", {"start": v(41.66, -6.23) * mm, "end": v(41.6, -6.2) * mm});
            skArc(sketch, "E168.34.0", {"start": v(42.66, -3.08) * mm, "mid": v(41.83, -3.58) * mm, "end": v(42.3, -4.44) * mm});
            skLineSegment(sketch, "E168.34.1", {"start": v(42.72, -3.1) * mm, "end": v(42.66, -3.08) * mm});
            skArc(sketch, "E168.34.2", {"start": v(42.2, -4.93) * mm, "mid": v(42.52, -4.77) * mm, "end": v(42.36, -4.46) * mm});
            skLineSegment(sketch, "E168.34.3", {"start": v(42.36, -4.46) * mm, "end": v(42.3, -4.44) * mm});
            skArc(sketch, "E168.35.0", {"start": v(42.94, -1.2) * mm, "mid": v(42.19, -1.8) * mm, "end": v(42.76, -2.6) * mm});
            skLineSegment(sketch, "E168.35.1", {"start": v(43, -1.2) * mm, "end": v(42.94, -1.2) * mm});
            skArc(sketch, "E168.35.2", {"start": v(42.72, -3.1) * mm, "mid": v(43.02, -2.9) * mm, "end": v(42.82, -2.6) * mm});
            skLineSegment(sketch, "E168.35.3", {"start": v(42.82, -2.6) * mm, "end": v(42.76, -2.6) * mm});
            skArc(sketch, "E168.36.0", {"start": v(42.98, 0.7) * mm, "mid": v(42.3, 0) * mm, "end": v(42.98, -0.7) * mm});
            skLineSegment(sketch, "E168.36.1", {"start": v(43.04, 0.7) * mm, "end": v(42.98, 0.7) * mm});
            skArc(sketch, "E168.36.2", {"start": v(43, -1.2) * mm, "mid": v(43.27, -0.97) * mm, "end": v(43.04, -0.7) * mm});
            skLineSegment(sketch, "E168.36.3", {"start": v(43.04, -0.7) * mm, "end": v(42.98, -0.7) * mm});
            skArc(sketch, "E168.37.0", {"start": v(42.76, 2.6) * mm, "mid": v(42.19, 1.8) * mm, "end": v(42.94, 1.2) * mm});
            skLineSegment(sketch, "E168.37.1", {"start": v(42.82, 2.6) * mm, "end": v(42.76, 2.6) * mm});
            skArc(sketch, "E168.37.2", {"start": v(43.04, 0.7) * mm, "mid": v(43.27, 0.97) * mm, "end": v(43, 1.2) * mm});
            skLineSegment(sketch, "E168.37.3", {"start": v(43, 1.2) * mm, "end": v(42.94, 1.2) * mm});
            skArc(sketch, "E168.38.0", {"start": v(42.3, 4.44) * mm, "mid": v(41.83, 3.58) * mm, "end": v(42.66, 3.08) * mm});
            skLineSegment(sketch, "E168.38.1", {"start": v(42.36, 4.46) * mm, "end": v(42.3, 4.44) * mm});
            skArc(sketch, "E168.38.2", {"start": v(42.82, 2.6) * mm, "mid": v(43.02, 2.9) * mm, "end": v(42.72, 3.1) * mm});
            skLineSegment(sketch, "E168.38.3", {"start": v(42.72, 3.1) * mm, "end": v(42.66, 3.08) * mm});
            skArc(sketch, "E168.39.0", {"start": v(41.6, 6.2) * mm, "mid": v(41.25, 5.3) * mm, "end": v(42.14, 4.9) * mm});
            skLineSegment(sketch, "E168.39.1", {"start": v(41.66, 6.23) * mm, "end": v(41.6, 6.2) * mm});
            skArc(sketch, "E168.39.2", {"start": v(42.36, 4.46) * mm, "mid": v(42.52, 4.77) * mm, "end": v(42.2, 4.93) * mm});
            skLineSegment(sketch, "E168.39.3", {"start": v(42.2, 4.93) * mm, "end": v(42.14, 4.9) * mm});
            skArc(sketch, "E168.40.0", {"start": v(40.68, 7.87) * mm, "mid": v(40.45, 6.93) * mm, "end": v(41.38, 6.65) * mm});
            skLineSegment(sketch, "E168.40.1", {"start": v(40.73, 7.9) * mm, "end": v(40.68, 7.87) * mm});
            skArc(sketch, "E168.40.2", {"start": v(41.66, 6.23) * mm, "mid": v(41.77, 6.57) * mm, "end": v(41.44, 6.68) * mm});
            skLineSegment(sketch, "E168.40.3", {"start": v(41.44, 6.68) * mm, "end": v(41.38, 6.65) * mm});
            skArc(sketch, "E168.41.0", {"start": v(39.55, 9.4) * mm, "mid": v(39.44, 8.43) * mm, "end": v(40.4, 8.28) * mm});
            skLineSegment(sketch, "E168.41.1", {"start": v(39.6, 9.44) * mm, "end": v(39.55, 9.4) * mm});
            skArc(sketch, "E168.41.2", {"start": v(40.73, 7.9) * mm, "mid": v(40.8, 8.25) * mm, "end": v(40.45, 8.32) * mm});
            skLineSegment(sketch, "E168.41.3", {"start": v(40.45, 8.32) * mm, "end": v(40.4, 8.28) * mm});
            skArc(sketch, "E168.42.0", {"start": v(38.22, 10.77) * mm, "mid": v(38.25, 9.8) * mm, "end": v(39.22, 9.77) * mm});
            skLineSegment(sketch, "E168.42.1", {"start": v(38.27, 10.81) * mm, "end": v(38.22, 10.77) * mm});
            skArc(sketch, "E168.42.2", {"start": v(39.6, 9.44) * mm, "mid": v(39.62, 9.8) * mm, "end": v(39.27, 9.81) * mm});
            skLineSegment(sketch, "E168.42.3", {"start": v(39.27, 9.81) * mm, "end": v(39.22, 9.77) * mm});
            skArc(sketch, "E168.43.0", {"start": v(36.74, 11.95) * mm, "mid": v(36.89, 10.99) * mm, "end": v(37.85, 11.1) * mm});
            skLineSegment(sketch, "E168.43.1", {"start": v(36.77, 12) * mm, "end": v(36.74, 11.95) * mm});
            skArc(sketch, "E168.43.2", {"start": v(38.27, 10.81) * mm, "mid": v(38.25, 11.16) * mm, "end": v(37.9, 11.14) * mm});
            skLineSegment(sketch, "E168.43.3", {"start": v(37.9, 11.14) * mm, "end": v(37.85, 11.1) * mm});
            skArc(sketch, "E168.44.0", {"start": v(35.1, 12.93) * mm, "mid": v(35.38, 12) * mm, "end": v(36.33, 12.22) * mm});
            skLineSegment(sketch, "E168.44.1", {"start": v(35.13, 12.98) * mm, "end": v(35.1, 12.93) * mm});
            skArc(sketch, "E168.44.2", {"start": v(36.77, 12) * mm, "mid": v(36.7, 12.35) * mm, "end": v(36.36, 12.28) * mm});
            skLineSegment(sketch, "E168.44.3", {"start": v(36.36, 12.28) * mm, "end": v(36.33, 12.22) * mm});
            skArc(sketch, "E168.45.0", {"start": v(33.36, 13.68) * mm, "mid": v(33.76, 12.8) * mm, "end": v(34.66, 13.15) * mm});
            skLineSegment(sketch, "E168.45.1", {"start": v(33.38, 13.74) * mm, "end": v(33.36, 13.68) * mm});
            skArc(sketch, "E168.45.2", {"start": v(35.13, 12.98) * mm, "mid": v(35.02, 13.32) * mm, "end": v(34.69, 13.2) * mm});
            skLineSegment(sketch, "E168.45.3", {"start": v(34.69, 13.2) * mm, "end": v(34.66, 13.15) * mm});
            skArc(sketch, "E168.46.0", {"start": v(31.53, 14.2) * mm, "mid": v(32.04, 13.38) * mm, "end": v(32.9, 13.84) * mm});
            skLineSegment(sketch, "E168.46.1", {"start": v(31.55, 14.27) * mm, "end": v(31.53, 14.2) * mm});
            skArc(sketch, "E168.46.2", {"start": v(33.38, 13.74) * mm, "mid": v(33.23, 14.06) * mm, "end": v(32.91, 13.9) * mm});
            skLineSegment(sketch, "E168.46.3", {"start": v(32.91, 13.9) * mm, "end": v(32.9, 13.84) * mm});
            skArc(sketch, "E168.47.0", {"start": v(29.65, 14.49) * mm, "mid": v(30.26, 13.73) * mm, "end": v(31.05, 14.3) * mm});
            skLineSegment(sketch, "E168.47.1", {"start": v(29.66, 14.55) * mm, "end": v(29.65, 14.49) * mm});
            skArc(sketch, "E168.47.2", {"start": v(31.55, 14.27) * mm, "mid": v(31.35, 14.56) * mm, "end": v(31.06, 14.37) * mm});
            skLineSegment(sketch, "E168.47.3", {"start": v(31.06, 14.37) * mm, "end": v(31.05, 14.3) * mm});
            skSolve(sketch);
        }
        {
            var Q0;
            Q0 = qSketchRegion(id + "F84", true);
            extrude(context, id + "F85", {"entities" : qUnion([Q0]), "operationType" : NewBodyOperationType.ADD, "depth" : 3.2 * mm});
        }
        {
            var Q0;
            Q0=makeQuery(id+"F85.opExtrude","CAP_FACE",FACE,{"disambiguationData":[OSD([sQuery(id+"F84.wireOp",EDGE,"E155"),sQuery(id+"F84.wireOp",EDGE,"E162"),sQuery(id+"F84.wireOp",EDGE,"E165"),sQuery(id+"F84.wireOp",EDGE,"E166"),sQuery(id+"F84.wireOp",EDGE,"E167.MirrorCS"),sQuery(id+"F84.wireOp",EDGE,"E168.1.0"),sQuery(id+"F84.wireOp",EDGE,"E168.1.1"),sQuery(id+"F84.wireOp",EDGE,"E168.1.2"),sQuery(id+"F84.wireOp",EDGE,"E168.1.3"),sQuery(id+"F84.wireOp",EDGE,"E168.2.0"),sQuery(id+"F84.wireOp",EDGE,"E168.2.1"),sQuery(id+"F84.wireOp",EDGE,"E168.2.2"),sQuery(id+"F84.wireOp",EDGE,"E168.2.3"),sQuery(id+"F84.wireOp",EDGE,"E168.3.0"),sQuery(id+"F84.wireOp",EDGE,"E168.3.1"),sQuery(id+"F84.wireOp",EDGE,"E168.3.2"),sQuery(id+"F84.wireOp",EDGE,"E168.3.3"),sQuery(id+"F84.wireOp",EDGE,"E168.4.0"),sQuery(id+"F84.wireOp",EDGE,"E168.4.1"),sQuery(id+"F84.wireOp",EDGE,"E168.4.2"),sQuery(id+"F84.wireOp",EDGE,"E168.4.3"),sQuery(id+"F84.wireOp",EDGE,"E168.5.0"),sQuery(id+"F84.wireOp",EDGE,"E168.5.1"),sQuery(id+"F84.wireOp",EDGE,"E168.5.2"),sQuery(id+"F84.wireOp",EDGE,"E168.5.3"),sQuery(id+"F84.wireOp",EDGE,"E168.6.0"),sQuery(id+"F84.wireOp",EDGE,"E168.6.1"),sQuery(id+"F84.wireOp",EDGE,"E168.6.2"),sQuery(id+"F84.wireOp",EDGE,"E168.6.3"),sQuery(id+"F84.wireOp",EDGE,"E168.7.0"),sQuery(id+"F84.wireOp",EDGE,"E168.7.1"),sQuery(id+"F84.wireOp",EDGE,"E168.7.2"),sQuery(id+"F84.wireOp",EDGE,"E168.7.3"),sQuery(id+"F84.wireOp",EDGE,"E168.8.0"),sQuery(id+"F84.wireOp",EDGE,"E168.8.1"),sQuery(id+"F84.wireOp",EDGE,"E168.8.2"),sQuery(id+"F84.wireOp",EDGE,"E168.8.3"),sQuery(id+"F84.wireOp",EDGE,"E168.9.0"),sQuery(id+"F84.wireOp",EDGE,"E168.9.1"),sQuery(id+"F84.wireOp",EDGE,"E168.9.2"),sQuery(id+"F84.wireOp",EDGE,"E168.9.3"),sQuery(id+"F84.wireOp",EDGE,"E168.10.0"),sQuery(id+"F84.wireOp",EDGE,"E168.10.1"),sQuery(id+"F84.wireOp",EDGE,"E168.10.2"),sQuery(id+"F84.wireOp",EDGE,"E168.10.3"),sQuery(id+"F84.wireOp",EDGE,"E168.11.0"),sQuery(id+"F84.wireOp",EDGE,"E168.11.1"),sQuery(id+"F84.wireOp",EDGE,"E168.11.2"),sQuery(id+"F84.wireOp",EDGE,"E168.11.3"),sQuery(id+"F84.wireOp",EDGE,"E168.12.0"),sQuery(id+"F84.wireOp",EDGE,"E168.12.1"),sQuery(id+"F84.wireOp",EDGE,"E168.12.2"),sQuery(id+"F84.wireOp",EDGE,"E168.12.3"),sQuery(id+"F84.wireOp",EDGE,"E168.13.0"),sQuery(id+"F84.wireOp",EDGE,"E168.13.1"),sQuery(id+"F84.wireOp",EDGE,"E168.13.2"),sQuery(id+"F84.wireOp",EDGE,"E168.13.3"),sQuery(id+"F84.wireOp",EDGE,"E168.14.0"),sQuery(id+"F84.wireOp",EDGE,"E168.14.1"),sQuery(id+"F84.wireOp",EDGE,"E168.14.2"),sQuery(id+"F84.wireOp",EDGE,"E168.14.3"),sQuery(id+"F84.wireOp",EDGE,"E168.15.0"),sQuery(id+"F84.wireOp",EDGE,"E168.15.1"),sQuery(id+"F84.wireOp",EDGE,"E168.15.2"),sQuery(id+"F84.wireOp",EDGE,"E168.15.3"),sQuery(id+"F84.wireOp",EDGE,"E168.16.0"),sQuery(id+"F84.wireOp",EDGE,"E168.16.1"),sQuery(id+"F84.wireOp",EDGE,"E168.16.2"),sQuery(id+"F84.wireOp",EDGE,"E168.16.3"),sQuery(id+"F84.wireOp",EDGE,"E168.17.0"),sQuery(id+"F84.wireOp",EDGE,"E168.17.1"),sQuery(id+"F84.wireOp",EDGE,"E168.17.2"),sQuery(id+"F84.wireOp",EDGE,"E168.17.3"),sQuery(id+"F84.wireOp",EDGE,"E168.18.0"),sQuery(id+"F84.wireOp",EDGE,"E168.18.1"),sQuery(id+"F84.wireOp",EDGE,"E168.18.2"),sQuery(id+"F84.wireOp",EDGE,"E168.18.3"),sQuery(id+"F84.wireOp",EDGE,"E168.19.0"),sQuery(id+"F84.wireOp",EDGE,"E168.19.1"),sQuery(id+"F84.wireOp",EDGE,"E168.19.2"),sQuery(id+"F84.wireOp",EDGE,"E168.19.3"),sQuery(id+"F84.wireOp",EDGE,"E168.20.0"),sQuery(id+"F84.wireOp",EDGE,"E168.20.1"),sQuery(id+"F84.wireOp",EDGE,"E168.20.2"),sQuery(id+"F84.wireOp",EDGE,"E168.20.3"),sQuery(id+"F84.wireOp",EDGE,"E168.21.0"),sQuery(id+"F84.wireOp",EDGE,"E168.21.1"),sQuery(id+"F84.wireOp",EDGE,"E168.21.2"),sQuery(id+"F84.wireOp",EDGE,"E168.21.3"),sQuery(id+"F84.wireOp",EDGE,"E168.22.0"),sQuery(id+"F84.wireOp",EDGE,"E168.22.1"),sQuery(id+"F84.wireOp",EDGE,"E168.22.2"),sQuery(id+"F84.wireOp",EDGE,"E168.22.3"),sQuery(id+"F84.wireOp",EDGE,"E168.23.0"),sQuery(id+"F84.wireOp",EDGE,"E168.23.1"),sQuery(id+"F84.wireOp",EDGE,"E168.23.2"),sQuery(id+"F84.wireOp",EDGE,"E168.23.3"),sQuery(id+"F84.wireOp",EDGE,"E168.24.0"),sQuery(id+"F84.wireOp",EDGE,"E168.24.1"),sQuery(id+"F84.wireOp",EDGE,"E168.24.2"),sQuery(id+"F84.wireOp",EDGE,"E168.24.3"),sQuery(id+"F84.wireOp",EDGE,"E168.25.0"),sQuery(id+"F84.wireOp",EDGE,"E168.25.1"),sQuery(id+"F84.wireOp",EDGE,"E168.25.2"),sQuery(id+"F84.wireOp",EDGE,"E168.25.3"),sQuery(id+"F84.wireOp",EDGE,"E168.26.0"),sQuery(id+"F84.wireOp",EDGE,"E168.26.1"),sQuery(id+"F84.wireOp",EDGE,"E168.26.2"),sQuery(id+"F84.wireOp",EDGE,"E168.26.3"),sQuery(id+"F84.wireOp",EDGE,"E168.27.0"),sQuery(id+"F84.wireOp",EDGE,"E168.27.1"),sQuery(id+"F84.wireOp",EDGE,"E168.27.2"),sQuery(id+"F84.wireOp",EDGE,"E168.27.3"),sQuery(id+"F84.wireOp",EDGE,"E168.28.0"),sQuery(id+"F84.wireOp",EDGE,"E168.28.1"),sQuery(id+"F84.wireOp",EDGE,"E168.28.2"),sQuery(id+"F84.wireOp",EDGE,"E168.28.3"),sQuery(id+"F84.wireOp",EDGE,"E168.29.0"),sQuery(id+"F84.wireOp",EDGE,"E168.29.1"),sQuery(id+"F84.wireOp",EDGE,"E168.29.2"),sQuery(id+"F84.wireOp",EDGE,"E168.29.3"),sQuery(id+"F84.wireOp",EDGE,"E168.30.0"),sQuery(id+"F84.wireOp",EDGE,"E168.30.1"),sQuery(id+"F84.wireOp",EDGE,"E168.30.2"),sQuery(id+"F84.wireOp",EDGE,"E168.30.3"),sQuery(id+"F84.wireOp",EDGE,"E168.31.0"),sQuery(id+"F84.wireOp",EDGE,"E168.31.1"),sQuery(id+"F84.wireOp",EDGE,"E168.31.2"),sQuery(id+"F84.wireOp",EDGE,"E168.31.3"),sQuery(id+"F84.wireOp",EDGE,"E168.32.0"),sQuery(id+"F84.wireOp",EDGE,"E168.32.1"),sQuery(id+"F84.wireOp",EDGE,"E168.32.2"),sQuery(id+"F84.wireOp",EDGE,"E168.32.3"),sQuery(id+"F84.wireOp",EDGE,"E168.33.0"),sQuery(id+"F84.wireOp",EDGE,"E168.33.1"),sQuery(id+"F84.wireOp",EDGE,"E168.33.2"),sQuery(id+"F84.wireOp",EDGE,"E168.33.3"),sQuery(id+"F84.wireOp",EDGE,"E168.34.0"),sQuery(id+"F84.wireOp",EDGE,"E168.34.1"),sQuery(id+"F84.wireOp",EDGE,"E168.34.2"),sQuery(id+"F84.wireOp",EDGE,"E168.34.3"),sQuery(id+"F84.wireOp",EDGE,"E168.35.0"),sQuery(id+"F84.wireOp",EDGE,"E168.35.1"),sQuery(id+"F84.wireOp",EDGE,"E168.35.2"),sQuery(id+"F84.wireOp",EDGE,"E168.35.3"),sQuery(id+"F84.wireOp",EDGE,"E168.36.0"),sQuery(id+"F84.wireOp",EDGE,"E168.36.1"),sQuery(id+"F84.wireOp",EDGE,"E168.36.2"),sQuery(id+"F84.wireOp",EDGE,"E168.36.3"),sQuery(id+"F84.wireOp",EDGE,"E168.37.0"),sQuery(id+"F84.wireOp",EDGE,"E168.37.1"),sQuery(id+"F84.wireOp",EDGE,"E168.37.2"),sQuery(id+"F84.wireOp",EDGE,"E168.37.3"),sQuery(id+"F84.wireOp",EDGE,"E168.38.0"),sQuery(id+"F84.wireOp",EDGE,"E168.38.1"),sQuery(id+"F84.wireOp",EDGE,"E168.38.2"),sQuery(id+"F84.wireOp",EDGE,"E168.38.3"),sQuery(id+"F84.wireOp",EDGE,"E168.39.0"),sQuery(id+"F84.wireOp",EDGE,"E168.39.1"),sQuery(id+"F84.wireOp",EDGE,"E168.39.2"),sQuery(id+"F84.wireOp",EDGE,"E168.39.3"),sQuery(id+"F84.wireOp",EDGE,"E168.40.0"),sQuery(id+"F84.wireOp",EDGE,"E168.40.1"),sQuery(id+"F84.wireOp",EDGE,"E168.40.2"),sQuery(id+"F84.wireOp",EDGE,"E168.40.3"),sQuery(id+"F84.wireOp",EDGE,"E168.41.0"),sQuery(id+"F84.wireOp",EDGE,"E168.41.1"),sQuery(id+"F84.wireOp",EDGE,"E168.41.2"),sQuery(id+"F84.wireOp",EDGE,"E168.41.3"),sQuery(id+"F84.wireOp",EDGE,"E168.42.0"),sQuery(id+"F84.wireOp",EDGE,"E168.42.1"),sQuery(id+"F84.wireOp",EDGE,"E168.42.2"),sQuery(id+"F84.wireOp",EDGE,"E168.42.3"),sQuery(id+"F84.wireOp",EDGE,"E168.43.0"),sQuery(id+"F84.wireOp",EDGE,"E168.43.1"),sQuery(id+"F84.wireOp",EDGE,"E168.43.2"),sQuery(id+"F84.wireOp",EDGE,"E168.43.3"),sQuery(id+"F84.wireOp",EDGE,"E168.44.0"),sQuery(id+"F84.wireOp",EDGE,"E168.44.1"),sQuery(id+"F84.wireOp",EDGE,"E168.44.2"),sQuery(id+"F84.wireOp",EDGE,"E168.44.3"),sQuery(id+"F84.wireOp",EDGE,"E168.45.0"),sQuery(id+"F84.wireOp",EDGE,"E168.45.1"),sQuery(id+"F84.wireOp",EDGE,"E168.45.2"),sQuery(id+"F84.wireOp",EDGE,"E168.45.3"),sQuery(id+"F84.wireOp",EDGE,"E168.46.0"),sQuery(id+"F84.wireOp",EDGE,"E168.46.1"),sQuery(id+"F84.wireOp",EDGE,"E168.46.2"),sQuery(id+"F84.wireOp",EDGE,"E168.46.3"),sQuery(id+"F84.wireOp",EDGE,"E168.47.0"),sQuery(id+"F84.wireOp",EDGE,"E168.47.1"),sQuery(id+"F84.wireOp",EDGE,"E168.47.2"),sQuery(id+"F84.wireOp",EDGE,"E168.47.3")])],"isStart":false});
            var sketch = newSketch(context, id + "F86", { "sketchPlane" : qUnion([Q0])});
            skCircle(sketch, "E169", {"center": v(28.46, 0) * mm, "radius": 3 * mm});
            skArc(sketch, "E170.0", {"start": v(27.75, 14.58) * mm, "mid": v(27.48, 14.82) * mm, "end": v(27.25, 14.55) * mm});
            skLineSegment(sketch, "E171.0", {"start": v(27.75, 14.58) * mm, "end": v(27.75, 14.52) * mm});
            skArc(sketch, "E172.0", {"start": v(27.75, 14.52) * mm, "mid": v(28.46, 13.85) * mm, "end": v(29.16, 14.52) * mm});
            skLineSegment(sketch, "E173.0", {"start": v(27.25, 14.55) * mm, "end": v(27.26, 14.49) * mm});
            skArc(sketch, "E174.1.0", {"start": v(25.85, 14.37) * mm, "mid": v(25.56, 14.56) * mm, "end": v(25.36, 14.27) * mm});
            skArc(sketch, "E174.1.1", {"start": v(25.86, 14.3) * mm, "mid": v(26.65, 13.73) * mm, "end": v(27.26, 14.49) * mm});
            skLineSegment(sketch, "E174.1.2", {"start": v(25.36, 14.27) * mm, "end": v(25.38, 14.2) * mm});
            skLineSegment(sketch, "E174.1.3", {"start": v(25.85, 14.37) * mm, "end": v(25.86, 14.3) * mm});
            skArc(sketch, "E174.2.0", {"start": v(24, 13.9) * mm, "mid": v(23.68, 14.06) * mm, "end": v(23.53, 13.74) * mm});
            skArc(sketch, "E174.2.1", {"start": v(24.02, 13.84) * mm, "mid": v(24.87, 13.38) * mm, "end": v(25.38, 14.2) * mm});
            skLineSegment(sketch, "E174.2.2", {"start": v(23.53, 13.74) * mm, "end": v(23.55, 13.68) * mm});
            skLineSegment(sketch, "E174.2.3", {"start": v(24, 13.9) * mm, "end": v(24.02, 13.84) * mm});
            skArc(sketch, "E174.3.0", {"start": v(22.22, 13.2) * mm, "mid": v(21.89, 13.32) * mm, "end": v(21.78, 12.98) * mm});
            skArc(sketch, "E174.3.1", {"start": v(22.25, 13.15) * mm, "mid": v(23.15, 12.8) * mm, "end": v(23.55, 13.68) * mm});
            skLineSegment(sketch, "E174.3.2", {"start": v(21.78, 12.98) * mm, "end": v(21.8, 12.93) * mm});
            skLineSegment(sketch, "E174.3.3", {"start": v(22.22, 13.2) * mm, "end": v(22.25, 13.15) * mm});
            skArc(sketch, "E174.4.0", {"start": v(20.55, 12.28) * mm, "mid": v(20.2, 12.35) * mm, "end": v(20.14, 12) * mm});
            skArc(sketch, "E174.4.1", {"start": v(20.58, 12.22) * mm, "mid": v(21.53, 12) * mm, "end": v(21.8, 12.93) * mm});
            skLineSegment(sketch, "E174.4.2", {"start": v(20.14, 12) * mm, "end": v(20.17, 11.95) * mm});
            skLineSegment(sketch, "E174.4.3", {"start": v(20.55, 12.28) * mm, "end": v(20.58, 12.22) * mm});
            skArc(sketch, "E174.5.0", {"start": v(19.02, 11.14) * mm, "mid": v(18.66, 11.16) * mm, "end": v(18.64, 10.81) * mm});
            skArc(sketch, "E174.5.1", {"start": v(19.06, 11.1) * mm, "mid": v(20.02, 10.99) * mm, "end": v(20.17, 11.95) * mm});
            skLineSegment(sketch, "E174.5.2", {"start": v(18.64, 10.81) * mm, "end": v(18.69, 10.77) * mm});
            skLineSegment(sketch, "E174.5.3", {"start": v(19.02, 11.14) * mm, "end": v(19.06, 11.1) * mm});
            skArc(sketch, "E174.6.0", {"start": v(17.64, 9.81) * mm, "mid": v(17.3, 9.8) * mm, "end": v(17.32, 9.44) * mm});
            skArc(sketch, "E174.6.1", {"start": v(17.69, 9.77) * mm, "mid": v(18.66, 9.8) * mm, "end": v(18.69, 10.77) * mm});
            skLineSegment(sketch, "E174.6.2", {"start": v(17.32, 9.44) * mm, "end": v(17.36, 9.4) * mm});
            skLineSegment(sketch, "E174.6.3", {"start": v(17.64, 9.81) * mm, "end": v(17.69, 9.77) * mm});
            skArc(sketch, "E174.7.0", {"start": v(16.46, 8.32) * mm, "mid": v(16.1, 8.25) * mm, "end": v(16.18, 7.9) * mm});
            skArc(sketch, "E174.7.1", {"start": v(16.5, 8.28) * mm, "mid": v(17.47, 8.43) * mm, "end": v(17.36, 9.4) * mm});
            skLineSegment(sketch, "E174.7.2", {"start": v(16.18, 7.9) * mm, "end": v(16.23, 7.87) * mm});
            skLineSegment(sketch, "E174.7.3", {"start": v(16.46, 8.32) * mm, "end": v(16.5, 8.28) * mm});
            skArc(sketch, "E174.8.0", {"start": v(15.47, 6.68) * mm, "mid": v(15.14, 6.57) * mm, "end": v(15.25, 6.23) * mm});
            skArc(sketch, "E174.8.1", {"start": v(15.53, 6.65) * mm, "mid": v(16.46, 6.92) * mm, "end": v(16.23, 7.87) * mm});
            skLineSegment(sketch, "E174.8.2", {"start": v(15.25, 6.23) * mm, "end": v(15.3, 6.2) * mm});
            skLineSegment(sketch, "E174.8.3", {"start": v(15.47, 6.68) * mm, "end": v(15.53, 6.65) * mm});
            skArc(sketch, "E174.9.0", {"start": v(14.71, 4.93) * mm, "mid": v(14.4, 4.77) * mm, "end": v(14.55, 4.46) * mm});
            skArc(sketch, "E174.9.1", {"start": v(14.77, 4.9) * mm, "mid": v(15.66, 5.3) * mm, "end": v(15.3, 6.2) * mm});
            skLineSegment(sketch, "E174.9.2", {"start": v(14.55, 4.46) * mm, "end": v(14.61, 4.44) * mm});
            skLineSegment(sketch, "E174.9.3", {"start": v(14.71, 4.93) * mm, "end": v(14.77, 4.9) * mm});
            skArc(sketch, "E174.10.0", {"start": v(14.19, 3.1) * mm, "mid": v(13.9, 2.9) * mm, "end": v(14.09, 2.6) * mm});
            skArc(sketch, "E174.10.1", {"start": v(14.25, 3.08) * mm, "mid": v(15.08, 3.58) * mm, "end": v(14.61, 4.44) * mm});
            skLineSegment(sketch, "E174.10.2", {"start": v(14.09, 2.6) * mm, "end": v(14.15, 2.6) * mm});
            skLineSegment(sketch, "E174.10.3", {"start": v(14.19, 3.1) * mm, "end": v(14.25, 3.08) * mm});
            skArc(sketch, "E174.11.0", {"start": v(13.9, 1.2) * mm, "mid": v(13.64, 0.97) * mm, "end": v(13.87, 0.7) * mm});
            skArc(sketch, "E174.11.1", {"start": v(13.97, 1.2) * mm, "mid": v(14.72, 1.8) * mm, "end": v(14.15, 2.6) * mm});
            skLineSegment(sketch, "E174.11.2", {"start": v(13.87, 0.7) * mm, "end": v(13.93, 0.7) * mm});
            skLineSegment(sketch, "E174.11.3", {"start": v(13.9, 1.2) * mm, "end": v(13.97, 1.2) * mm});
            skArc(sketch, "E174.12.0", {"start": v(13.87, -0.7) * mm, "mid": v(13.64, -0.97) * mm, "end": v(13.9, -1.2) * mm});
            skArc(sketch, "E174.12.1", {"start": v(13.93, -0.7) * mm, "mid": v(14.6, 0) * mm, "end": v(13.93, 0.7) * mm});
            skLineSegment(sketch, "E174.12.2", {"start": v(13.9, -1.2) * mm, "end": v(13.97, -1.2) * mm});
            skLineSegment(sketch, "E174.12.3", {"start": v(13.87, -0.7) * mm, "end": v(13.93, -0.7) * mm});
            skArc(sketch, "E174.13.0", {"start": v(14.09, -2.6) * mm, "mid": v(13.9, -2.9) * mm, "end": v(14.19, -3.1) * mm});
            skArc(sketch, "E174.13.1", {"start": v(14.15, -2.6) * mm, "mid": v(14.72, -1.8) * mm, "end": v(13.97, -1.2) * mm});
            skLineSegment(sketch, "E174.13.2", {"start": v(14.19, -3.1) * mm, "end": v(14.25, -3.08) * mm});
            skLineSegment(sketch, "E174.13.3", {"start": v(14.09, -2.6) * mm, "end": v(14.15, -2.6) * mm});
            skArc(sketch, "E174.14.0", {"start": v(14.55, -4.46) * mm, "mid": v(14.4, -4.77) * mm, "end": v(14.71, -4.93) * mm});
            skArc(sketch, "E174.14.1", {"start": v(14.61, -4.44) * mm, "mid": v(15.08, -3.58) * mm, "end": v(14.25, -3.08) * mm});
            skLineSegment(sketch, "E174.14.2", {"start": v(14.71, -4.93) * mm, "end": v(14.77, -4.9) * mm});
            skLineSegment(sketch, "E174.14.3", {"start": v(14.55, -4.46) * mm, "end": v(14.61, -4.44) * mm});
            skArc(sketch, "E174.15.0", {"start": v(15.25, -6.23) * mm, "mid": v(15.14, -6.57) * mm, "end": v(15.47, -6.68) * mm});
            skArc(sketch, "E174.15.1", {"start": v(15.3, -6.2) * mm, "mid": v(15.66, -5.3) * mm, "end": v(14.77, -4.9) * mm});
            skLineSegment(sketch, "E174.15.2", {"start": v(15.47, -6.68) * mm, "end": v(15.53, -6.65) * mm});
            skLineSegment(sketch, "E174.15.3", {"start": v(15.25, -6.23) * mm, "end": v(15.3, -6.2) * mm});
            skArc(sketch, "E174.16.0", {"start": v(16.18, -7.9) * mm, "mid": v(16.1, -8.25) * mm, "end": v(16.46, -8.32) * mm});
            skArc(sketch, "E174.16.1", {"start": v(16.23, -7.87) * mm, "mid": v(16.46, -6.93) * mm, "end": v(15.53, -6.65) * mm});
            skLineSegment(sketch, "E174.16.2", {"start": v(16.46, -8.32) * mm, "end": v(16.5, -8.28) * mm});
            skLineSegment(sketch, "E174.16.3", {"start": v(16.18, -7.9) * mm, "end": v(16.23, -7.87) * mm});
            skArc(sketch, "E174.17.0", {"start": v(17.32, -9.44) * mm, "mid": v(17.3, -9.8) * mm, "end": v(17.64, -9.81) * mm});
            skArc(sketch, "E174.17.1", {"start": v(17.36, -9.4) * mm, "mid": v(17.47, -8.43) * mm, "end": v(16.5, -8.28) * mm});
            skLineSegment(sketch, "E174.17.2", {"start": v(17.64, -9.81) * mm, "end": v(17.69, -9.77) * mm});
            skLineSegment(sketch, "E174.17.3", {"start": v(17.32, -9.44) * mm, "end": v(17.36, -9.4) * mm});
            skArc(sketch, "E174.18.0", {"start": v(18.64, -10.81) * mm, "mid": v(18.66, -11.16) * mm, "end": v(19.02, -11.14) * mm});
            skArc(sketch, "E174.18.1", {"start": v(18.69, -10.77) * mm, "mid": v(18.66, -9.8) * mm, "end": v(17.69, -9.77) * mm});
            skLineSegment(sketch, "E174.18.2", {"start": v(19.02, -11.14) * mm, "end": v(19.06, -11.1) * mm});
            skLineSegment(sketch, "E174.18.3", {"start": v(18.64, -10.81) * mm, "end": v(18.69, -10.77) * mm});
            skArc(sketch, "E174.19.0", {"start": v(20.14, -12) * mm, "mid": v(20.2, -12.35) * mm, "end": v(20.55, -12.28) * mm});
            skArc(sketch, "E174.19.1", {"start": v(20.17, -11.95) * mm, "mid": v(20.02, -10.99) * mm, "end": v(19.06, -11.1) * mm});
            skLineSegment(sketch, "E174.19.2", {"start": v(20.55, -12.28) * mm, "end": v(20.58, -12.22) * mm});
            skLineSegment(sketch, "E174.19.3", {"start": v(20.14, -12) * mm, "end": v(20.17, -11.95) * mm});
            skArc(sketch, "E174.20.0", {"start": v(21.78, -12.98) * mm, "mid": v(21.89, -13.32) * mm, "end": v(22.22, -13.2) * mm});
            skArc(sketch, "E174.20.1", {"start": v(21.8, -12.93) * mm, "mid": v(21.53, -12) * mm, "end": v(20.58, -12.22) * mm});
            skLineSegment(sketch, "E174.20.2", {"start": v(22.22, -13.2) * mm, "end": v(22.25, -13.15) * mm});
            skLineSegment(sketch, "E174.20.3", {"start": v(21.78, -12.98) * mm, "end": v(21.8, -12.93) * mm});
            skArc(sketch, "E174.21.0", {"start": v(23.53, -13.74) * mm, "mid": v(23.68, -14.06) * mm, "end": v(24, -13.9) * mm});
            skArc(sketch, "E174.21.1", {"start": v(23.55, -13.68) * mm, "mid": v(23.15, -12.8) * mm, "end": v(22.25, -13.15) * mm});
            skLineSegment(sketch, "E174.21.2", {"start": v(24, -13.9) * mm, "end": v(24.02, -13.84) * mm});
            skLineSegment(sketch, "E174.21.3", {"start": v(23.53, -13.74) * mm, "end": v(23.55, -13.68) * mm});
            skArc(sketch, "E174.22.0", {"start": v(25.36, -14.27) * mm, "mid": v(25.56, -14.56) * mm, "end": v(25.85, -14.37) * mm});
            skArc(sketch, "E174.22.1", {"start": v(25.38, -14.2) * mm, "mid": v(24.87, -13.38) * mm, "end": v(24.02, -13.84) * mm});
            skLineSegment(sketch, "E174.22.2", {"start": v(25.85, -14.37) * mm, "end": v(25.86, -14.3) * mm});
            skLineSegment(sketch, "E174.22.3", {"start": v(25.36, -14.27) * mm, "end": v(25.38, -14.2) * mm});
            skArc(sketch, "E174.23.0", {"start": v(27.25, -14.55) * mm, "mid": v(27.48, -14.82) * mm, "end": v(27.75, -14.58) * mm});
            skArc(sketch, "E174.23.1", {"start": v(27.26, -14.49) * mm, "mid": v(26.65, -13.73) * mm, "end": v(25.86, -14.3) * mm});
            skLineSegment(sketch, "E174.23.2", {"start": v(27.75, -14.58) * mm, "end": v(27.75, -14.52) * mm});
            skLineSegment(sketch, "E174.23.3", {"start": v(27.25, -14.55) * mm, "end": v(27.26, -14.49) * mm});
            skArc(sketch, "E174.24.0", {"start": v(29.16, -14.58) * mm, "mid": v(29.43, -14.82) * mm, "end": v(29.66, -14.55) * mm});
            skArc(sketch, "E174.24.1", {"start": v(29.16, -14.52) * mm, "mid": v(28.46, -13.85) * mm, "end": v(27.75, -14.52) * mm});
            skLineSegment(sketch, "E174.24.2", {"start": v(29.66, -14.55) * mm, "end": v(29.65, -14.49) * mm});
            skLineSegment(sketch, "E174.24.3", {"start": v(29.16, -14.58) * mm, "end": v(29.16, -14.52) * mm});
            skArc(sketch, "E174.25.0", {"start": v(31.06, -14.37) * mm, "mid": v(31.35, -14.56) * mm, "end": v(31.55, -14.27) * mm});
            skArc(sketch, "E174.25.1", {"start": v(31.05, -14.3) * mm, "mid": v(30.26, -13.73) * mm, "end": v(29.65, -14.49) * mm});
            skLineSegment(sketch, "E174.25.2", {"start": v(31.55, -14.27) * mm, "end": v(31.53, -14.2) * mm});
            skLineSegment(sketch, "E174.25.3", {"start": v(31.06, -14.37) * mm, "end": v(31.05, -14.3) * mm});
            skArc(sketch, "E174.26.0", {"start": v(32.91, -13.9) * mm, "mid": v(33.23, -14.06) * mm, "end": v(33.38, -13.74) * mm});
            skArc(sketch, "E174.26.1", {"start": v(32.9, -13.84) * mm, "mid": v(32.04, -13.38) * mm, "end": v(31.53, -14.2) * mm});
            skLineSegment(sketch, "E174.26.2", {"start": v(33.38, -13.74) * mm, "end": v(33.36, -13.68) * mm});
            skLineSegment(sketch, "E174.26.3", {"start": v(32.91, -13.9) * mm, "end": v(32.9, -13.84) * mm});
            skArc(sketch, "E174.27.0", {"start": v(34.69, -13.2) * mm, "mid": v(35.02, -13.32) * mm, "end": v(35.13, -12.98) * mm});
            skArc(sketch, "E174.27.1", {"start": v(34.66, -13.15) * mm, "mid": v(33.76, -12.8) * mm, "end": v(33.36, -13.68) * mm});
            skLineSegment(sketch, "E174.27.2", {"start": v(35.13, -12.98) * mm, "end": v(35.1, -12.93) * mm});
            skLineSegment(sketch, "E174.27.3", {"start": v(34.69, -13.2) * mm, "end": v(34.66, -13.15) * mm});
            skArc(sketch, "E174.28.0", {"start": v(36.36, -12.28) * mm, "mid": v(36.7, -12.35) * mm, "end": v(36.77, -12) * mm});
            skArc(sketch, "E174.28.1", {"start": v(36.33, -12.22) * mm, "mid": v(35.38, -12) * mm, "end": v(35.1, -12.93) * mm});
            skLineSegment(sketch, "E174.28.2", {"start": v(36.77, -12) * mm, "end": v(36.74, -11.95) * mm});
            skLineSegment(sketch, "E174.28.3", {"start": v(36.36, -12.28) * mm, "end": v(36.33, -12.22) * mm});
            skArc(sketch, "E174.29.0", {"start": v(37.9, -11.14) * mm, "mid": v(38.25, -11.16) * mm, "end": v(38.27, -10.81) * mm});
            skArc(sketch, "E174.29.1", {"start": v(37.85, -11.1) * mm, "mid": v(36.89, -10.99) * mm, "end": v(36.74, -11.95) * mm});
            skLineSegment(sketch, "E174.29.2", {"start": v(38.27, -10.81) * mm, "end": v(38.22, -10.77) * mm});
            skLineSegment(sketch, "E174.29.3", {"start": v(37.9, -11.14) * mm, "end": v(37.85, -11.1) * mm});
            skArc(sketch, "E174.30.0", {"start": v(39.27, -9.81) * mm, "mid": v(39.62, -9.8) * mm, "end": v(39.6, -9.44) * mm});
            skArc(sketch, "E174.30.1", {"start": v(39.22, -9.77) * mm, "mid": v(38.25, -9.8) * mm, "end": v(38.22, -10.77) * mm});
            skLineSegment(sketch, "E174.30.2", {"start": v(39.6, -9.44) * mm, "end": v(39.55, -9.4) * mm});
            skLineSegment(sketch, "E174.30.3", {"start": v(39.27, -9.81) * mm, "end": v(39.22, -9.77) * mm});
            skArc(sketch, "E174.31.0", {"start": v(40.45, -8.32) * mm, "mid": v(40.8, -8.25) * mm, "end": v(40.73, -7.9) * mm});
            skArc(sketch, "E174.31.1", {"start": v(40.4, -8.28) * mm, "mid": v(39.44, -8.43) * mm, "end": v(39.55, -9.4) * mm});
            skLineSegment(sketch, "E174.31.2", {"start": v(40.73, -7.9) * mm, "end": v(40.68, -7.87) * mm});
            skLineSegment(sketch, "E174.31.3", {"start": v(40.45, -8.32) * mm, "end": v(40.4, -8.28) * mm});
            skArc(sketch, "E174.32.0", {"start": v(41.44, -6.68) * mm, "mid": v(41.77, -6.57) * mm, "end": v(41.66, -6.23) * mm});
            skArc(sketch, "E174.32.1", {"start": v(41.38, -6.65) * mm, "mid": v(40.45, -6.92) * mm, "end": v(40.68, -7.87) * mm});
            skLineSegment(sketch, "E174.32.2", {"start": v(41.66, -6.23) * mm, "end": v(41.6, -6.2) * mm});
            skLineSegment(sketch, "E174.32.3", {"start": v(41.44, -6.68) * mm, "end": v(41.38, -6.65) * mm});
            skArc(sketch, "E174.33.0", {"start": v(42.2, -4.93) * mm, "mid": v(42.52, -4.77) * mm, "end": v(42.36, -4.46) * mm});
            skArc(sketch, "E174.33.1", {"start": v(42.14, -4.9) * mm, "mid": v(41.25, -5.3) * mm, "end": v(41.6, -6.2) * mm});
            skLineSegment(sketch, "E174.33.2", {"start": v(42.36, -4.46) * mm, "end": v(42.3, -4.44) * mm});
            skLineSegment(sketch, "E174.33.3", {"start": v(42.2, -4.93) * mm, "end": v(42.14, -4.9) * mm});
            skArc(sketch, "E174.34.0", {"start": v(42.72, -3.1) * mm, "mid": v(43.02, -2.9) * mm, "end": v(42.82, -2.6) * mm});
            skArc(sketch, "E174.34.1", {"start": v(42.66, -3.08) * mm, "mid": v(41.83, -3.58) * mm, "end": v(42.3, -4.44) * mm});
            skLineSegment(sketch, "E174.34.2", {"start": v(42.82, -2.6) * mm, "end": v(42.76, -2.6) * mm});
            skLineSegment(sketch, "E174.34.3", {"start": v(42.72, -3.1) * mm, "end": v(42.66, -3.08) * mm});
            skArc(sketch, "E174.35.0", {"start": v(43, -1.2) * mm, "mid": v(43.27, -0.97) * mm, "end": v(43.04, -0.7) * mm});
            skArc(sketch, "E174.35.1", {"start": v(42.94, -1.2) * mm, "mid": v(42.19, -1.8) * mm, "end": v(42.76, -2.6) * mm});
            skLineSegment(sketch, "E174.35.2", {"start": v(43.04, -0.7) * mm, "end": v(42.98, -0.7) * mm});
            skLineSegment(sketch, "E174.35.3", {"start": v(43, -1.2) * mm, "end": v(42.94, -1.2) * mm});
            skArc(sketch, "E174.36.0", {"start": v(43.04, 0.7) * mm, "mid": v(43.27, 0.97) * mm, "end": v(43, 1.2) * mm});
            skArc(sketch, "E174.36.1", {"start": v(42.98, 0.7) * mm, "mid": v(42.3, 0) * mm, "end": v(42.98, -0.7) * mm});
            skLineSegment(sketch, "E174.36.2", {"start": v(43, 1.2) * mm, "end": v(42.94, 1.2) * mm});
            skLineSegment(sketch, "E174.36.3", {"start": v(43.04, 0.7) * mm, "end": v(42.98, 0.7) * mm});
            skArc(sketch, "E174.37.0", {"start": v(42.82, 2.6) * mm, "mid": v(43.02, 2.9) * mm, "end": v(42.72, 3.1) * mm});
            skArc(sketch, "E174.37.1", {"start": v(42.76, 2.6) * mm, "mid": v(42.19, 1.8) * mm, "end": v(42.94, 1.2) * mm});
            skLineSegment(sketch, "E174.37.2", {"start": v(42.72, 3.1) * mm, "end": v(42.66, 3.08) * mm});
            skLineSegment(sketch, "E174.37.3", {"start": v(42.82, 2.6) * mm, "end": v(42.76, 2.6) * mm});
            skArc(sketch, "E174.38.0", {"start": v(42.36, 4.46) * mm, "mid": v(42.52, 4.77) * mm, "end": v(42.2, 4.93) * mm});
            skArc(sketch, "E174.38.1", {"start": v(42.3, 4.44) * mm, "mid": v(41.83, 3.58) * mm, "end": v(42.66, 3.08) * mm});
            skLineSegment(sketch, "E174.38.2", {"start": v(42.2, 4.93) * mm, "end": v(42.14, 4.9) * mm});
            skLineSegment(sketch, "E174.38.3", {"start": v(42.36, 4.46) * mm, "end": v(42.3, 4.44) * mm});
            skArc(sketch, "E174.39.0", {"start": v(41.66, 6.23) * mm, "mid": v(41.77, 6.57) * mm, "end": v(41.44, 6.68) * mm});
            skArc(sketch, "E174.39.1", {"start": v(41.6, 6.2) * mm, "mid": v(41.25, 5.3) * mm, "end": v(42.14, 4.9) * mm});
            skLineSegment(sketch, "E174.39.2", {"start": v(41.44, 6.68) * mm, "end": v(41.38, 6.65) * mm});
            skLineSegment(sketch, "E174.39.3", {"start": v(41.66, 6.23) * mm, "end": v(41.6, 6.2) * mm});
            skArc(sketch, "E174.40.0", {"start": v(40.73, 7.9) * mm, "mid": v(40.8, 8.25) * mm, "end": v(40.45, 8.32) * mm});
            skArc(sketch, "E174.40.1", {"start": v(40.68, 7.87) * mm, "mid": v(40.45, 6.93) * mm, "end": v(41.38, 6.65) * mm});
            skLineSegment(sketch, "E174.40.2", {"start": v(40.45, 8.32) * mm, "end": v(40.4, 8.28) * mm});
            skLineSegment(sketch, "E174.40.3", {"start": v(40.73, 7.9) * mm, "end": v(40.68, 7.87) * mm});
            skArc(sketch, "E174.41.0", {"start": v(39.6, 9.44) * mm, "mid": v(39.62, 9.8) * mm, "end": v(39.27, 9.81) * mm});
            skArc(sketch, "E174.41.1", {"start": v(39.55, 9.4) * mm, "mid": v(39.44, 8.43) * mm, "end": v(40.4, 8.28) * mm});
            skLineSegment(sketch, "E174.41.2", {"start": v(39.27, 9.81) * mm, "end": v(39.22, 9.77) * mm});
            skLineSegment(sketch, "E174.41.3", {"start": v(39.6, 9.44) * mm, "end": v(39.55, 9.4) * mm});
            skArc(sketch, "E174.42.0", {"start": v(38.27, 10.81) * mm, "mid": v(38.25, 11.16) * mm, "end": v(37.9, 11.14) * mm});
            skArc(sketch, "E174.42.1", {"start": v(38.22, 10.77) * mm, "mid": v(38.25, 9.8) * mm, "end": v(39.22, 9.77) * mm});
            skLineSegment(sketch, "E174.42.2", {"start": v(37.9, 11.14) * mm, "end": v(37.85, 11.1) * mm});
            skLineSegment(sketch, "E174.42.3", {"start": v(38.27, 10.81) * mm, "end": v(38.22, 10.77) * mm});
            skArc(sketch, "E174.43.0", {"start": v(36.77, 12) * mm, "mid": v(36.7, 12.35) * mm, "end": v(36.36, 12.28) * mm});
            skArc(sketch, "E174.43.1", {"start": v(36.74, 11.95) * mm, "mid": v(36.89, 10.99) * mm, "end": v(37.85, 11.1) * mm});
            skLineSegment(sketch, "E174.43.2", {"start": v(36.36, 12.28) * mm, "end": v(36.33, 12.22) * mm});
            skLineSegment(sketch, "E174.43.3", {"start": v(36.77, 12) * mm, "end": v(36.74, 11.95) * mm});
            skArc(sketch, "E174.44.0", {"start": v(35.13, 12.98) * mm, "mid": v(35.02, 13.32) * mm, "end": v(34.69, 13.2) * mm});
            skArc(sketch, "E174.44.1", {"start": v(35.1, 12.93) * mm, "mid": v(35.38, 12) * mm, "end": v(36.33, 12.22) * mm});
            skLineSegment(sketch, "E174.44.2", {"start": v(34.69, 13.2) * mm, "end": v(34.66, 13.15) * mm});
            skLineSegment(sketch, "E174.44.3", {"start": v(35.13, 12.98) * mm, "end": v(35.1, 12.93) * mm});
            skArc(sketch, "E174.45.0", {"start": v(33.38, 13.74) * mm, "mid": v(33.23, 14.06) * mm, "end": v(32.91, 13.9) * mm});
            skArc(sketch, "E174.45.1", {"start": v(33.36, 13.68) * mm, "mid": v(33.76, 12.8) * mm, "end": v(34.66, 13.15) * mm});
            skLineSegment(sketch, "E174.45.2", {"start": v(32.91, 13.9) * mm, "end": v(32.9, 13.84) * mm});
            skLineSegment(sketch, "E174.45.3", {"start": v(33.38, 13.74) * mm, "end": v(33.36, 13.68) * mm});
            skArc(sketch, "E174.46.0", {"start": v(31.55, 14.27) * mm, "mid": v(31.35, 14.56) * mm, "end": v(31.06, 14.37) * mm});
            skArc(sketch, "E174.46.1", {"start": v(31.53, 14.2) * mm, "mid": v(32.04, 13.38) * mm, "end": v(32.9, 13.84) * mm});
            skLineSegment(sketch, "E174.46.2", {"start": v(31.06, 14.37) * mm, "end": v(31.05, 14.3) * mm});
            skLineSegment(sketch, "E174.46.3", {"start": v(31.55, 14.27) * mm, "end": v(31.53, 14.2) * mm});
            skArc(sketch, "E174.47.0", {"start": v(29.66, 14.55) * mm, "mid": v(29.43, 14.82) * mm, "end": v(29.16, 14.58) * mm});
            skArc(sketch, "E174.47.1", {"start": v(29.65, 14.49) * mm, "mid": v(30.26, 13.73) * mm, "end": v(31.05, 14.3) * mm});
            skLineSegment(sketch, "E174.47.2", {"start": v(29.16, 14.58) * mm, "end": v(29.16, 14.52) * mm});
            skLineSegment(sketch, "E174.47.3", {"start": v(29.66, 14.55) * mm, "end": v(29.65, 14.49) * mm});
            skSolve(sketch);
        }
        {
            var Q0;
            Q0 = qSketchRegion(id + "F86", true);
            extrude(context, id + "F87", {"entities" : qUnion([Q0]), "operationType" : NewBodyOperationType.ADD, "depth" : 3.8 * mm});
        }
        {
            var Q0;
            Q0=makeQuery(id+"F87.opExtrude","CAP_FACE",FACE,{"disambiguationData":[OSD([sQuery(id+"F86.wireOp",EDGE,"E169"),sQuery(id+"F86.wireOp",EDGE,"E170.0"),sQuery(id+"F86.wireOp",EDGE,"E171.0"),sQuery(id+"F86.wireOp",EDGE,"E172.0"),sQuery(id+"F86.wireOp",EDGE,"E173.0"),sQuery(id+"F86.wireOp",EDGE,"E174.1.0"),sQuery(id+"F86.wireOp",EDGE,"E174.1.1"),sQuery(id+"F86.wireOp",EDGE,"E174.1.2"),sQuery(id+"F86.wireOp",EDGE,"E174.1.3"),sQuery(id+"F86.wireOp",EDGE,"E174.2.0"),sQuery(id+"F86.wireOp",EDGE,"E174.2.1"),sQuery(id+"F86.wireOp",EDGE,"E174.2.2"),sQuery(id+"F86.wireOp",EDGE,"E174.2.3"),sQuery(id+"F86.wireOp",EDGE,"E174.3.0"),sQuery(id+"F86.wireOp",EDGE,"E174.3.1"),sQuery(id+"F86.wireOp",EDGE,"E174.3.2"),sQuery(id+"F86.wireOp",EDGE,"E174.3.3"),sQuery(id+"F86.wireOp",EDGE,"E174.4.0"),sQuery(id+"F86.wireOp",EDGE,"E174.4.1"),sQuery(id+"F86.wireOp",EDGE,"E174.4.2"),sQuery(id+"F86.wireOp",EDGE,"E174.4.3"),sQuery(id+"F86.wireOp",EDGE,"E174.5.0"),sQuery(id+"F86.wireOp",EDGE,"E174.5.1"),sQuery(id+"F86.wireOp",EDGE,"E174.5.2"),sQuery(id+"F86.wireOp",EDGE,"E174.5.3"),sQuery(id+"F86.wireOp",EDGE,"E174.6.0"),sQuery(id+"F86.wireOp",EDGE,"E174.6.1"),sQuery(id+"F86.wireOp",EDGE,"E174.6.2"),sQuery(id+"F86.wireOp",EDGE,"E174.6.3"),sQuery(id+"F86.wireOp",EDGE,"E174.7.0"),sQuery(id+"F86.wireOp",EDGE,"E174.7.1"),sQuery(id+"F86.wireOp",EDGE,"E174.7.2"),sQuery(id+"F86.wireOp",EDGE,"E174.7.3"),sQuery(id+"F86.wireOp",EDGE,"E174.8.0"),sQuery(id+"F86.wireOp",EDGE,"E174.8.1"),sQuery(id+"F86.wireOp",EDGE,"E174.8.2"),sQuery(id+"F86.wireOp",EDGE,"E174.8.3"),sQuery(id+"F86.wireOp",EDGE,"E174.9.0"),sQuery(id+"F86.wireOp",EDGE,"E174.9.1"),sQuery(id+"F86.wireOp",EDGE,"E174.9.2"),sQuery(id+"F86.wireOp",EDGE,"E174.9.3"),sQuery(id+"F86.wireOp",EDGE,"E174.10.0"),sQuery(id+"F86.wireOp",EDGE,"E174.10.1"),sQuery(id+"F86.wireOp",EDGE,"E174.10.2"),sQuery(id+"F86.wireOp",EDGE,"E174.10.3"),sQuery(id+"F86.wireOp",EDGE,"E174.11.0"),sQuery(id+"F86.wireOp",EDGE,"E174.11.1"),sQuery(id+"F86.wireOp",EDGE,"E174.11.2"),sQuery(id+"F86.wireOp",EDGE,"E174.11.3"),sQuery(id+"F86.wireOp",EDGE,"E174.12.0"),sQuery(id+"F86.wireOp",EDGE,"E174.12.1"),sQuery(id+"F86.wireOp",EDGE,"E174.12.2"),sQuery(id+"F86.wireOp",EDGE,"E174.12.3"),sQuery(id+"F86.wireOp",EDGE,"E174.13.0"),sQuery(id+"F86.wireOp",EDGE,"E174.13.1"),sQuery(id+"F86.wireOp",EDGE,"E174.13.2"),sQuery(id+"F86.wireOp",EDGE,"E174.13.3"),sQuery(id+"F86.wireOp",EDGE,"E174.14.0"),sQuery(id+"F86.wireOp",EDGE,"E174.14.1"),sQuery(id+"F86.wireOp",EDGE,"E174.14.2"),sQuery(id+"F86.wireOp",EDGE,"E174.14.3"),sQuery(id+"F86.wireOp",EDGE,"E174.15.0"),sQuery(id+"F86.wireOp",EDGE,"E174.15.1"),sQuery(id+"F86.wireOp",EDGE,"E174.15.2"),sQuery(id+"F86.wireOp",EDGE,"E174.15.3"),sQuery(id+"F86.wireOp",EDGE,"E174.16.0"),sQuery(id+"F86.wireOp",EDGE,"E174.16.1"),sQuery(id+"F86.wireOp",EDGE,"E174.16.2"),sQuery(id+"F86.wireOp",EDGE,"E174.16.3"),sQuery(id+"F86.wireOp",EDGE,"E174.17.0"),sQuery(id+"F86.wireOp",EDGE,"E174.17.1"),sQuery(id+"F86.wireOp",EDGE,"E174.17.2"),sQuery(id+"F86.wireOp",EDGE,"E174.17.3"),sQuery(id+"F86.wireOp",EDGE,"E174.18.0"),sQuery(id+"F86.wireOp",EDGE,"E174.18.1"),sQuery(id+"F86.wireOp",EDGE,"E174.18.2"),sQuery(id+"F86.wireOp",EDGE,"E174.18.3"),sQuery(id+"F86.wireOp",EDGE,"E174.19.0"),sQuery(id+"F86.wireOp",EDGE,"E174.19.1"),sQuery(id+"F86.wireOp",EDGE,"E174.19.2"),sQuery(id+"F86.wireOp",EDGE,"E174.19.3"),sQuery(id+"F86.wireOp",EDGE,"E174.20.0"),sQuery(id+"F86.wireOp",EDGE,"E174.20.1"),sQuery(id+"F86.wireOp",EDGE,"E174.20.2"),sQuery(id+"F86.wireOp",EDGE,"E174.20.3"),sQuery(id+"F86.wireOp",EDGE,"E174.21.0"),sQuery(id+"F86.wireOp",EDGE,"E174.21.1"),sQuery(id+"F86.wireOp",EDGE,"E174.21.2"),sQuery(id+"F86.wireOp",EDGE,"E174.21.3"),sQuery(id+"F86.wireOp",EDGE,"E174.22.0"),sQuery(id+"F86.wireOp",EDGE,"E174.22.1"),sQuery(id+"F86.wireOp",EDGE,"E174.22.2"),sQuery(id+"F86.wireOp",EDGE,"E174.22.3"),sQuery(id+"F86.wireOp",EDGE,"E174.23.0"),sQuery(id+"F86.wireOp",EDGE,"E174.23.1"),sQuery(id+"F86.wireOp",EDGE,"E174.23.2"),sQuery(id+"F86.wireOp",EDGE,"E174.23.3"),sQuery(id+"F86.wireOp",EDGE,"E174.24.0"),sQuery(id+"F86.wireOp",EDGE,"E174.24.1"),sQuery(id+"F86.wireOp",EDGE,"E174.24.2"),sQuery(id+"F86.wireOp",EDGE,"E174.24.3"),sQuery(id+"F86.wireOp",EDGE,"E174.25.0"),sQuery(id+"F86.wireOp",EDGE,"E174.25.1"),sQuery(id+"F86.wireOp",EDGE,"E174.25.2"),sQuery(id+"F86.wireOp",EDGE,"E174.25.3"),sQuery(id+"F86.wireOp",EDGE,"E174.26.0"),sQuery(id+"F86.wireOp",EDGE,"E174.26.1"),sQuery(id+"F86.wireOp",EDGE,"E174.26.2"),sQuery(id+"F86.wireOp",EDGE,"E174.26.3"),sQuery(id+"F86.wireOp",EDGE,"E174.27.0"),sQuery(id+"F86.wireOp",EDGE,"E174.27.1"),sQuery(id+"F86.wireOp",EDGE,"E174.27.2"),sQuery(id+"F86.wireOp",EDGE,"E174.27.3"),sQuery(id+"F86.wireOp",EDGE,"E174.28.0"),sQuery(id+"F86.wireOp",EDGE,"E174.28.1"),sQuery(id+"F86.wireOp",EDGE,"E174.28.2"),sQuery(id+"F86.wireOp",EDGE,"E174.28.3"),sQuery(id+"F86.wireOp",EDGE,"E174.29.0"),sQuery(id+"F86.wireOp",EDGE,"E174.29.1"),sQuery(id+"F86.wireOp",EDGE,"E174.29.2"),sQuery(id+"F86.wireOp",EDGE,"E174.29.3"),sQuery(id+"F86.wireOp",EDGE,"E174.30.0"),sQuery(id+"F86.wireOp",EDGE,"E174.30.1"),sQuery(id+"F86.wireOp",EDGE,"E174.30.2"),sQuery(id+"F86.wireOp",EDGE,"E174.30.3"),sQuery(id+"F86.wireOp",EDGE,"E174.31.0"),sQuery(id+"F86.wireOp",EDGE,"E174.31.1"),sQuery(id+"F86.wireOp",EDGE,"E174.31.2"),sQuery(id+"F86.wireOp",EDGE,"E174.31.3"),sQuery(id+"F86.wireOp",EDGE,"E174.32.0"),sQuery(id+"F86.wireOp",EDGE,"E174.32.1"),sQuery(id+"F86.wireOp",EDGE,"E174.32.2"),sQuery(id+"F86.wireOp",EDGE,"E174.32.3"),sQuery(id+"F86.wireOp",EDGE,"E174.33.0"),sQuery(id+"F86.wireOp",EDGE,"E174.33.1"),sQuery(id+"F86.wireOp",EDGE,"E174.33.2"),sQuery(id+"F86.wireOp",EDGE,"E174.33.3"),sQuery(id+"F86.wireOp",EDGE,"E174.34.0"),sQuery(id+"F86.wireOp",EDGE,"E174.34.1"),sQuery(id+"F86.wireOp",EDGE,"E174.34.2"),sQuery(id+"F86.wireOp",EDGE,"E174.34.3"),sQuery(id+"F86.wireOp",EDGE,"E174.35.0"),sQuery(id+"F86.wireOp",EDGE,"E174.35.1"),sQuery(id+"F86.wireOp",EDGE,"E174.35.2"),sQuery(id+"F86.wireOp",EDGE,"E174.35.3"),sQuery(id+"F86.wireOp",EDGE,"E174.36.0"),sQuery(id+"F86.wireOp",EDGE,"E174.36.1"),sQuery(id+"F86.wireOp",EDGE,"E174.36.2"),sQuery(id+"F86.wireOp",EDGE,"E174.36.3"),sQuery(id+"F86.wireOp",EDGE,"E174.37.0"),sQuery(id+"F86.wireOp",EDGE,"E174.37.1"),sQuery(id+"F86.wireOp",EDGE,"E174.37.2"),sQuery(id+"F86.wireOp",EDGE,"E174.37.3"),sQuery(id+"F86.wireOp",EDGE,"E174.38.0"),sQuery(id+"F86.wireOp",EDGE,"E174.38.1"),sQuery(id+"F86.wireOp",EDGE,"E174.38.2"),sQuery(id+"F86.wireOp",EDGE,"E174.38.3"),sQuery(id+"F86.wireOp",EDGE,"E174.39.0"),sQuery(id+"F86.wireOp",EDGE,"E174.39.1"),sQuery(id+"F86.wireOp",EDGE,"E174.39.2"),sQuery(id+"F86.wireOp",EDGE,"E174.39.3"),sQuery(id+"F86.wireOp",EDGE,"E174.40.0"),sQuery(id+"F86.wireOp",EDGE,"E174.40.1"),sQuery(id+"F86.wireOp",EDGE,"E174.40.2"),sQuery(id+"F86.wireOp",EDGE,"E174.40.3"),sQuery(id+"F86.wireOp",EDGE,"E174.41.0"),sQuery(id+"F86.wireOp",EDGE,"E174.41.1"),sQuery(id+"F86.wireOp",EDGE,"E174.41.2"),sQuery(id+"F86.wireOp",EDGE,"E174.41.3"),sQuery(id+"F86.wireOp",EDGE,"E174.42.0"),sQuery(id+"F86.wireOp",EDGE,"E174.42.1"),sQuery(id+"F86.wireOp",EDGE,"E174.42.2"),sQuery(id+"F86.wireOp",EDGE,"E174.42.3"),sQuery(id+"F86.wireOp",EDGE,"E174.43.0"),sQuery(id+"F86.wireOp",EDGE,"E174.43.1"),sQuery(id+"F86.wireOp",EDGE,"E174.43.2"),sQuery(id+"F86.wireOp",EDGE,"E174.43.3"),sQuery(id+"F86.wireOp",EDGE,"E174.44.0"),sQuery(id+"F86.wireOp",EDGE,"E174.44.1"),sQuery(id+"F86.wireOp",EDGE,"E174.44.2"),sQuery(id+"F86.wireOp",EDGE,"E174.44.3"),sQuery(id+"F86.wireOp",EDGE,"E174.45.0"),sQuery(id+"F86.wireOp",EDGE,"E174.45.1"),sQuery(id+"F86.wireOp",EDGE,"E174.45.2"),sQuery(id+"F86.wireOp",EDGE,"E174.45.3"),sQuery(id+"F86.wireOp",EDGE,"E174.46.0"),sQuery(id+"F86.wireOp",EDGE,"E174.46.1"),sQuery(id+"F86.wireOp",EDGE,"E174.46.2"),sQuery(id+"F86.wireOp",EDGE,"E174.46.3"),sQuery(id+"F86.wireOp",EDGE,"E174.47.0"),sQuery(id+"F86.wireOp",EDGE,"E174.47.1"),sQuery(id+"F86.wireOp",EDGE,"E174.47.2"),sQuery(id+"F86.wireOp",EDGE,"E174.47.3")])],"isStart":false});
            var sketch = newSketch(context, id + "F88", { "sketchPlane" : qUnion([Q0])});
            skCircle(sketch, "E175.0", {"center": v(28.46, 0) * mm, "radius": 3 * mm});
            skCircle(sketch, "E176.0", {"center": v(28.46, 0) * mm, "radius": 16 * mm});
            skSolve(sketch);
        }
        {
            var Q0;
            Q0 = qSketchRegion(id + "F88", true);
            extrude(context, id + "F89", {"entities" : qUnion([Q0]), "operationType" : NewBodyOperationType.ADD, "depth" : 1 * mm});
        }
        {
            var Q0;
            Q0=makeQuery(id+"F89.opExtrude","CAP_FACE",FACE,{"disambiguationData":[OSD([sQuery(id+"F88.wireOp",EDGE,"E175.0"),sQuery(id+"F88.wireOp",EDGE,"E176.0")])],"isStart":false});
            var sketch = newSketch(context, id + "F90", { "sketchPlane" : qUnion([Q0])});
            skLineSegment(sketch, "E177.0", {"start": v(29.3, 7.55) * mm, "end": v(28.95, 6.58) * mm});
            skArc(sketch, "E178.0", {"start": v(27.96, 6.58) * mm, "mid": v(28.46, 6.6) * mm, "end": v(28.95, 6.58) * mm});
            skLineSegment(sketch, "E179.0", {"start": v(27.6, 7.55) * mm, "end": v(27.96, 6.58) * mm});
            skArc(sketch, "E180.0", {"start": v(29.3, 7.55) * mm, "mid": v(29.64, 7.5) * mm, "end": v(29.98, 7.45) * mm});
            skLineSegment(sketch, "E181.1.0", {"start": v(25.31, 6.92) * mm, "end": v(25.95, 6.1) * mm});
            skArc(sketch, "E181.1.1", {"start": v(25.95, 6.1) * mm, "mid": v(26.42, 6.28) * mm, "end": v(26.9, 6.41) * mm});
            skLineSegment(sketch, "E181.1.2", {"start": v(26.93, 7.45) * mm, "end": v(26.9, 6.41) * mm});
            skArc(sketch, "E181.1.3", {"start": v(26.93, 7.45) * mm, "mid": v(27.27, 7.5) * mm, "end": v(27.6, 7.55) * mm});
            skLineSegment(sketch, "E181.2.0", {"start": v(23.33, 5.61) * mm, "end": v(24.18, 5.03) * mm});
            skArc(sketch, "E181.2.1", {"start": v(24.18, 5.03) * mm, "mid": v(24.58, 5.34) * mm, "end": v(24.99, 5.62) * mm});
            skLineSegment(sketch, "E181.2.2", {"start": v(24.7, 6.6) * mm, "end": v(24.99, 5.62) * mm});
            skArc(sketch, "E181.2.3", {"start": v(24.7, 6.6) * mm, "mid": v(25, 6.77) * mm, "end": v(25.31, 6.92) * mm});
            skLineSegment(sketch, "E181.3.0", {"start": v(21.85, 3.75) * mm, "end": v(22.84, 3.47) * mm});
            skArc(sketch, "E181.3.1", {"start": v(22.84, 3.47) * mm, "mid": v(23.12, 3.88) * mm, "end": v(23.42, 4.27) * mm});
            skLineSegment(sketch, "E181.3.2", {"start": v(22.84, 5.13) * mm, "end": v(23.42, 4.27) * mm});
            skArc(sketch, "E181.3.3", {"start": v(22.84, 5.13) * mm, "mid": v(23.08, 5.37) * mm, "end": v(23.33, 5.61) * mm});
            skLineSegment(sketch, "E181.4.0", {"start": v(21, 1.53) * mm, "end": v(22.04, 1.56) * mm});
            skArc(sketch, "E181.4.1", {"start": v(22.04, 1.56) * mm, "mid": v(22.18, 2.04) * mm, "end": v(22.35, 2.5) * mm});
            skLineSegment(sketch, "E181.4.2", {"start": v(21.53, 3.14) * mm, "end": v(22.35, 2.5) * mm});
            skArc(sketch, "E181.4.3", {"start": v(21.53, 3.14) * mm, "mid": v(21.68, 3.45) * mm, "end": v(21.85, 3.75) * mm});
            skLineSegment(sketch, "E181.5.0", {"start": v(20.9, -0.85) * mm, "end": v(21.87, -0.5) * mm});
            skArc(sketch, "E181.5.1", {"start": v(21.87, -0.5) * mm, "mid": v(21.86, 0) * mm, "end": v(21.87, 0.5) * mm});
            skLineSegment(sketch, "E181.5.2", {"start": v(20.9, 0.85) * mm, "end": v(21.87, 0.5) * mm});
            skArc(sketch, "E181.5.3", {"start": v(20.9, 0.85) * mm, "mid": v(20.95, 1.19) * mm, "end": v(21, 1.53) * mm});
            skLineSegment(sketch, "E181.6.0", {"start": v(21.53, -3.14) * mm, "end": v(22.35, -2.5) * mm});
            skArc(sketch, "E181.6.1", {"start": v(22.35, -2.5) * mm, "mid": v(22.18, -2.04) * mm, "end": v(22.04, -1.56) * mm});
            skLineSegment(sketch, "E181.6.2", {"start": v(21, -1.53) * mm, "end": v(22.04, -1.56) * mm});
            skArc(sketch, "E181.6.3", {"start": v(21, -1.53) * mm, "mid": v(20.95, -1.19) * mm, "end": v(20.9, -0.85) * mm});
            skLineSegment(sketch, "E181.7.0", {"start": v(22.84, -5.13) * mm, "end": v(23.42, -4.27) * mm});
            skArc(sketch, "E181.7.1", {"start": v(23.42, -4.27) * mm, "mid": v(23.12, -3.88) * mm, "end": v(22.84, -3.47) * mm});
            skLineSegment(sketch, "E181.7.2", {"start": v(21.85, -3.75) * mm, "end": v(22.84, -3.47) * mm});
            skArc(sketch, "E181.7.3", {"start": v(21.85, -3.75) * mm, "mid": v(21.68, -3.45) * mm, "end": v(21.53, -3.14) * mm});
            skLineSegment(sketch, "E181.8.0", {"start": v(24.7, -6.6) * mm, "end": v(24.99, -5.62) * mm});
            skArc(sketch, "E181.8.1", {"start": v(24.99, -5.62) * mm, "mid": v(24.58, -5.34) * mm, "end": v(24.18, -5.03) * mm});
            skLineSegment(sketch, "E181.8.2", {"start": v(23.33, -5.61) * mm, "end": v(24.18, -5.03) * mm});
            skArc(sketch, "E181.8.3", {"start": v(23.33, -5.61) * mm, "mid": v(23.08, -5.37) * mm, "end": v(22.84, -5.13) * mm});
            skLineSegment(sketch, "E181.9.0", {"start": v(26.93, -7.45) * mm, "end": v(26.9, -6.41) * mm});
            skArc(sketch, "E181.9.1", {"start": v(26.9, -6.41) * mm, "mid": v(26.42, -6.28) * mm, "end": v(25.95, -6.1) * mm});
            skLineSegment(sketch, "E181.9.2", {"start": v(25.31, -6.92) * mm, "end": v(25.95, -6.1) * mm});
            skArc(sketch, "E181.9.3", {"start": v(25.31, -6.92) * mm, "mid": v(25, -6.77) * mm, "end": v(24.7, -6.6) * mm});
            skLineSegment(sketch, "E181.10.0", {"start": v(29.3, -7.55) * mm, "end": v(28.95, -6.58) * mm});
            skArc(sketch, "E181.10.1", {"start": v(28.95, -6.58) * mm, "mid": v(28.46, -6.6) * mm, "end": v(27.96, -6.58) * mm});
            skLineSegment(sketch, "E181.10.2", {"start": v(27.6, -7.55) * mm, "end": v(27.96, -6.58) * mm});
            skArc(sketch, "E181.10.3", {"start": v(27.6, -7.55) * mm, "mid": v(27.27, -7.5) * mm, "end": v(26.93, -7.45) * mm});
            skLineSegment(sketch, "E181.11.0", {"start": v(31.6, -6.92) * mm, "end": v(30.96, -6.1) * mm});
            skArc(sketch, "E181.11.1", {"start": v(30.96, -6.1) * mm, "mid": v(30.5, -6.28) * mm, "end": v(30.02, -6.41) * mm});
            skLineSegment(sketch, "E181.11.2", {"start": v(29.98, -7.45) * mm, "end": v(30.02, -6.41) * mm});
            skArc(sketch, "E181.11.3", {"start": v(29.98, -7.45) * mm, "mid": v(29.64, -7.5) * mm, "end": v(29.3, -7.55) * mm});
            skLineSegment(sketch, "E181.12.0", {"start": v(33.58, -5.61) * mm, "end": v(32.73, -5.03) * mm});
            skArc(sketch, "E181.12.1", {"start": v(32.73, -5.03) * mm, "mid": v(32.33, -5.34) * mm, "end": v(31.92, -5.62) * mm});
            skLineSegment(sketch, "E181.12.2", {"start": v(32.2, -6.6) * mm, "end": v(31.92, -5.62) * mm});
            skArc(sketch, "E181.12.3", {"start": v(32.2, -6.6) * mm, "mid": v(31.9, -6.77) * mm, "end": v(31.6, -6.92) * mm});
            skLineSegment(sketch, "E181.13.0", {"start": v(35.06, -3.75) * mm, "end": v(34.07, -3.47) * mm});
            skArc(sketch, "E181.13.1", {"start": v(34.07, -3.47) * mm, "mid": v(33.8, -3.88) * mm, "end": v(33.49, -4.27) * mm});
            skLineSegment(sketch, "E181.13.2", {"start": v(34.07, -5.13) * mm, "end": v(33.49, -4.27) * mm});
            skArc(sketch, "E181.13.3", {"start": v(34.07, -5.13) * mm, "mid": v(33.83, -5.37) * mm, "end": v(33.58, -5.61) * mm});
            skLineSegment(sketch, "E181.14.0", {"start": v(35.9, -1.53) * mm, "end": v(34.87, -1.56) * mm});
            skArc(sketch, "E181.14.1", {"start": v(34.87, -1.56) * mm, "mid": v(34.73, -2.04) * mm, "end": v(34.56, -2.5) * mm});
            skLineSegment(sketch, "E181.14.2", {"start": v(35.38, -3.14) * mm, "end": v(34.56, -2.5) * mm});
            skArc(sketch, "E181.14.3", {"start": v(35.38, -3.14) * mm, "mid": v(35.23, -3.45) * mm, "end": v(35.06, -3.75) * mm});
            skLineSegment(sketch, "E181.15.0", {"start": v(36, 0.85) * mm, "end": v(35.04, 0.5) * mm});
            skArc(sketch, "E181.15.1", {"start": v(35.04, 0.5) * mm, "mid": v(35.06, 0) * mm, "end": v(35.04, -0.5) * mm});
            skLineSegment(sketch, "E181.15.2", {"start": v(36, -0.85) * mm, "end": v(35.04, -0.5) * mm});
            skArc(sketch, "E181.15.3", {"start": v(36, -0.85) * mm, "mid": v(35.96, -1.19) * mm, "end": v(35.9, -1.53) * mm});
            skLineSegment(sketch, "E181.16.0", {"start": v(35.38, 3.14) * mm, "end": v(34.56, 2.5) * mm});
            skArc(sketch, "E181.16.1", {"start": v(34.56, 2.5) * mm, "mid": v(34.73, 2.04) * mm, "end": v(34.87, 1.56) * mm});
            skLineSegment(sketch, "E181.16.2", {"start": v(35.9, 1.53) * mm, "end": v(34.87, 1.56) * mm});
            skArc(sketch, "E181.16.3", {"start": v(35.9, 1.53) * mm, "mid": v(35.96, 1.19) * mm, "end": v(36, 0.85) * mm});
            skLineSegment(sketch, "E181.17.0", {"start": v(34.07, 5.13) * mm, "end": v(33.49, 4.27) * mm});
            skArc(sketch, "E181.17.1", {"start": v(33.49, 4.27) * mm, "mid": v(33.8, 3.88) * mm, "end": v(34.07, 3.47) * mm});
            skLineSegment(sketch, "E181.17.2", {"start": v(35.06, 3.75) * mm, "end": v(34.07, 3.47) * mm});
            skArc(sketch, "E181.17.3", {"start": v(35.06, 3.75) * mm, "mid": v(35.23, 3.45) * mm, "end": v(35.38, 3.14) * mm});
            skLineSegment(sketch, "E181.18.0", {"start": v(32.2, 6.6) * mm, "end": v(31.92, 5.62) * mm});
            skArc(sketch, "E181.18.1", {"start": v(31.92, 5.62) * mm, "mid": v(32.33, 5.34) * mm, "end": v(32.73, 5.03) * mm});
            skLineSegment(sketch, "E181.18.2", {"start": v(33.58, 5.61) * mm, "end": v(32.73, 5.03) * mm});
            skArc(sketch, "E181.18.3", {"start": v(33.58, 5.61) * mm, "mid": v(33.83, 5.37) * mm, "end": v(34.07, 5.13) * mm});
            skLineSegment(sketch, "E181.19.0", {"start": v(29.98, 7.45) * mm, "end": v(30.02, 6.41) * mm});
            skArc(sketch, "E181.19.1", {"start": v(30.02, 6.41) * mm, "mid": v(30.5, 6.28) * mm, "end": v(30.96, 6.1) * mm});
            skLineSegment(sketch, "E181.19.2", {"start": v(31.6, 6.92) * mm, "end": v(30.96, 6.1) * mm});
            skArc(sketch, "E181.19.3", {"start": v(31.6, 6.92) * mm, "mid": v(31.9, 6.77) * mm, "end": v(32.2, 6.6) * mm});
            skCircle(sketch, "E182", {"center": v(28.46, 0) * mm, "radius": 3 * mm});
            skCircle(sketch, "E183.0", {"center": v(28.46, 0) * mm, "radius": 3 * mm, "construction": true});
            skSolve(sketch);
        }
        {
            var Q0;
            Q0 = qSketchRegion(id + "F90", true);
            extrude(context, id + "F91", {"entities" : qUnion([Q0]), "operationType" : NewBodyOperationType.ADD, "depth" : 7.8 * mm});
        }
        {
            var Q0;
            Q0=makeQuery(id+"F91.opExtrude","CAP_FACE",FACE,{"disambiguationData":[OSD([sQuery(id+"F90.wireOp",EDGE,"E177.0"),sQuery(id+"F90.wireOp",EDGE,"E178.0"),sQuery(id+"F90.wireOp",EDGE,"E179.0"),sQuery(id+"F90.wireOp",EDGE,"E180.0"),sQuery(id+"F90.wireOp",EDGE,"E181.1.0"),sQuery(id+"F90.wireOp",EDGE,"E181.1.1"),sQuery(id+"F90.wireOp",EDGE,"E181.1.2"),sQuery(id+"F90.wireOp",EDGE,"E181.1.3"),sQuery(id+"F90.wireOp",EDGE,"E181.2.0"),sQuery(id+"F90.wireOp",EDGE,"E181.2.1"),sQuery(id+"F90.wireOp",EDGE,"E181.2.2"),sQuery(id+"F90.wireOp",EDGE,"E181.2.3"),sQuery(id+"F90.wireOp",EDGE,"E181.3.0"),sQuery(id+"F90.wireOp",EDGE,"E181.3.1"),sQuery(id+"F90.wireOp",EDGE,"E181.3.2"),sQuery(id+"F90.wireOp",EDGE,"E181.3.3"),sQuery(id+"F90.wireOp",EDGE,"E181.4.0"),sQuery(id+"F90.wireOp",EDGE,"E181.4.1"),sQuery(id+"F90.wireOp",EDGE,"E181.4.2"),sQuery(id+"F90.wireOp",EDGE,"E181.4.3"),sQuery(id+"F90.wireOp",EDGE,"E181.5.0"),sQuery(id+"F90.wireOp",EDGE,"E181.5.1"),sQuery(id+"F90.wireOp",EDGE,"E181.5.2"),sQuery(id+"F90.wireOp",EDGE,"E181.5.3"),sQuery(id+"F90.wireOp",EDGE,"E181.6.0"),sQuery(id+"F90.wireOp",EDGE,"E181.6.1"),sQuery(id+"F90.wireOp",EDGE,"E181.6.2"),sQuery(id+"F90.wireOp",EDGE,"E181.6.3"),sQuery(id+"F90.wireOp",EDGE,"E181.7.0"),sQuery(id+"F90.wireOp",EDGE,"E181.7.1"),sQuery(id+"F90.wireOp",EDGE,"E181.7.2"),sQuery(id+"F90.wireOp",EDGE,"E181.7.3"),sQuery(id+"F90.wireOp",EDGE,"E181.8.0"),sQuery(id+"F90.wireOp",EDGE,"E181.8.1"),sQuery(id+"F90.wireOp",EDGE,"E181.8.2"),sQuery(id+"F90.wireOp",EDGE,"E181.8.3"),sQuery(id+"F90.wireOp",EDGE,"E181.9.0"),sQuery(id+"F90.wireOp",EDGE,"E181.9.1"),sQuery(id+"F90.wireOp",EDGE,"E181.9.2"),sQuery(id+"F90.wireOp",EDGE,"E181.9.3"),sQuery(id+"F90.wireOp",EDGE,"E181.10.0"),sQuery(id+"F90.wireOp",EDGE,"E181.10.1"),sQuery(id+"F90.wireOp",EDGE,"E181.10.2"),sQuery(id+"F90.wireOp",EDGE,"E181.10.3"),sQuery(id+"F90.wireOp",EDGE,"E181.11.0"),sQuery(id+"F90.wireOp",EDGE,"E181.11.1"),sQuery(id+"F90.wireOp",EDGE,"E181.11.2"),sQuery(id+"F90.wireOp",EDGE,"E181.11.3"),sQuery(id+"F90.wireOp",EDGE,"E181.12.0"),sQuery(id+"F90.wireOp",EDGE,"E181.12.1"),sQuery(id+"F90.wireOp",EDGE,"E181.12.2"),sQuery(id+"F90.wireOp",EDGE,"E181.12.3"),sQuery(id+"F90.wireOp",EDGE,"E181.13.0"),sQuery(id+"F90.wireOp",EDGE,"E181.13.1"),sQuery(id+"F90.wireOp",EDGE,"E181.13.2"),sQuery(id+"F90.wireOp",EDGE,"E181.13.3"),sQuery(id+"F90.wireOp",EDGE,"E181.14.0"),sQuery(id+"F90.wireOp",EDGE,"E181.14.1"),sQuery(id+"F90.wireOp",EDGE,"E181.14.2"),sQuery(id+"F90.wireOp",EDGE,"E181.14.3"),sQuery(id+"F90.wireOp",EDGE,"E181.15.0"),sQuery(id+"F90.wireOp",EDGE,"E181.15.1"),sQuery(id+"F90.wireOp",EDGE,"E181.15.2"),sQuery(id+"F90.wireOp",EDGE,"E181.15.3"),sQuery(id+"F90.wireOp",EDGE,"E181.16.0"),sQuery(id+"F90.wireOp",EDGE,"E181.16.1"),sQuery(id+"F90.wireOp",EDGE,"E181.16.2"),sQuery(id+"F90.wireOp",EDGE,"E181.16.3"),sQuery(id+"F90.wireOp",EDGE,"E181.17.0"),sQuery(id+"F90.wireOp",EDGE,"E181.17.1"),sQuery(id+"F90.wireOp",EDGE,"E181.17.2"),sQuery(id+"F90.wireOp",EDGE,"E181.17.3"),sQuery(id+"F90.wireOp",EDGE,"E181.18.0"),sQuery(id+"F90.wireOp",EDGE,"E181.18.1"),sQuery(id+"F90.wireOp",EDGE,"E181.18.2"),sQuery(id+"F90.wireOp",EDGE,"E181.18.3"),sQuery(id+"F90.wireOp",EDGE,"E181.19.0"),sQuery(id+"F90.wireOp",EDGE,"E181.19.1"),sQuery(id+"F90.wireOp",EDGE,"E181.19.2"),sQuery(id+"F90.wireOp",EDGE,"E181.19.3"),sQuery(id+"F90.wireOp",EDGE,"E182")])],"isStart":false});
            var sketch = newSketch(context, id + "F92", { "sketchPlane" : qUnion([Q0])});
            skCircle(sketch, "E184", {"center": v(28.46, 0) * mm, "radius": 5.1 * mm});
            skLineSegment(sketch, "E185.0", {"start": v(27.6, 7.55) * mm, "end": v(27.96, 6.58) * mm});
            skArc(sketch, "E186.0", {"start": v(27.96, 6.58) * mm, "mid": v(28.46, 6.6) * mm, "end": v(28.95, 6.58) * mm});
            skLineSegment(sketch, "E187.0", {"start": v(29.3, 7.55) * mm, "end": v(28.95, 6.58) * mm});
            skArc(sketch, "E188.0", {"start": v(26.93, 7.45) * mm, "mid": v(27.27, 7.5) * mm, "end": v(27.6, 7.55) * mm});
            skArc(sketch, "E189.1.0", {"start": v(25.95, 6.1) * mm, "mid": v(26.42, 6.28) * mm, "end": v(26.9, 6.41) * mm});
            skLineSegment(sketch, "E189.1.1", {"start": v(25.31, 6.92) * mm, "end": v(25.95, 6.1) * mm});
            skArc(sketch, "E189.1.2", {"start": v(24.7, 6.6) * mm, "mid": v(25, 6.77) * mm, "end": v(25.31, 6.92) * mm});
            skLineSegment(sketch, "E189.1.3", {"start": v(26.93, 7.45) * mm, "end": v(26.9, 6.41) * mm});
            skArc(sketch, "E189.2.0", {"start": v(24.18, 5.03) * mm, "mid": v(24.58, 5.34) * mm, "end": v(24.99, 5.62) * mm});
            skLineSegment(sketch, "E189.2.1", {"start": v(23.33, 5.61) * mm, "end": v(24.18, 5.03) * mm});
            skArc(sketch, "E189.2.2", {"start": v(22.84, 5.13) * mm, "mid": v(23.08, 5.37) * mm, "end": v(23.33, 5.61) * mm});
            skLineSegment(sketch, "E189.2.3", {"start": v(24.7, 6.6) * mm, "end": v(24.99, 5.62) * mm});
            skArc(sketch, "E189.3.0", {"start": v(22.84, 3.47) * mm, "mid": v(23.12, 3.88) * mm, "end": v(23.42, 4.27) * mm});
            skLineSegment(sketch, "E189.3.1", {"start": v(21.85, 3.75) * mm, "end": v(22.84, 3.47) * mm});
            skArc(sketch, "E189.3.2", {"start": v(21.53, 3.14) * mm, "mid": v(21.68, 3.45) * mm, "end": v(21.85, 3.75) * mm});
            skLineSegment(sketch, "E189.3.3", {"start": v(22.84, 5.13) * mm, "end": v(23.42, 4.27) * mm});
            skArc(sketch, "E189.4.0", {"start": v(22.04, 1.56) * mm, "mid": v(22.18, 2.04) * mm, "end": v(22.35, 2.5) * mm});
            skLineSegment(sketch, "E189.4.1", {"start": v(21, 1.53) * mm, "end": v(22.04, 1.56) * mm});
            skArc(sketch, "E189.4.2", {"start": v(20.9, 0.85) * mm, "mid": v(20.95, 1.19) * mm, "end": v(21, 1.53) * mm});
            skLineSegment(sketch, "E189.4.3", {"start": v(21.53, 3.14) * mm, "end": v(22.35, 2.5) * mm});
            skArc(sketch, "E189.5.0", {"start": v(21.87, -0.5) * mm, "mid": v(21.86, 0) * mm, "end": v(21.87, 0.5) * mm});
            skLineSegment(sketch, "E189.5.1", {"start": v(20.9, -0.85) * mm, "end": v(21.87, -0.5) * mm});
            skArc(sketch, "E189.5.2", {"start": v(21, -1.53) * mm, "mid": v(20.95, -1.19) * mm, "end": v(20.9, -0.85) * mm});
            skLineSegment(sketch, "E189.5.3", {"start": v(20.9, 0.85) * mm, "end": v(21.87, 0.5) * mm});
            skArc(sketch, "E189.6.0", {"start": v(22.35, -2.5) * mm, "mid": v(22.18, -2.04) * mm, "end": v(22.04, -1.56) * mm});
            skLineSegment(sketch, "E189.6.1", {"start": v(21.53, -3.14) * mm, "end": v(22.35, -2.5) * mm});
            skArc(sketch, "E189.6.2", {"start": v(21.85, -3.75) * mm, "mid": v(21.68, -3.45) * mm, "end": v(21.53, -3.14) * mm});
            skLineSegment(sketch, "E189.6.3", {"start": v(21, -1.53) * mm, "end": v(22.04, -1.56) * mm});
            skArc(sketch, "E189.7.0", {"start": v(23.42, -4.27) * mm, "mid": v(23.12, -3.88) * mm, "end": v(22.84, -3.47) * mm});
            skLineSegment(sketch, "E189.7.1", {"start": v(22.84, -5.13) * mm, "end": v(23.42, -4.27) * mm});
            skArc(sketch, "E189.7.2", {"start": v(23.33, -5.61) * mm, "mid": v(23.08, -5.37) * mm, "end": v(22.84, -5.13) * mm});
            skLineSegment(sketch, "E189.7.3", {"start": v(21.85, -3.75) * mm, "end": v(22.84, -3.47) * mm});
            skArc(sketch, "E189.8.0", {"start": v(24.99, -5.62) * mm, "mid": v(24.58, -5.34) * mm, "end": v(24.18, -5.03) * mm});
            skLineSegment(sketch, "E189.8.1", {"start": v(24.7, -6.6) * mm, "end": v(24.99, -5.62) * mm});
            skArc(sketch, "E189.8.2", {"start": v(25.31, -6.92) * mm, "mid": v(25, -6.77) * mm, "end": v(24.7, -6.6) * mm});
            skLineSegment(sketch, "E189.8.3", {"start": v(23.33, -5.61) * mm, "end": v(24.18, -5.03) * mm});
            skArc(sketch, "E189.9.0", {"start": v(26.9, -6.41) * mm, "mid": v(26.42, -6.28) * mm, "end": v(25.95, -6.1) * mm});
            skLineSegment(sketch, "E189.9.1", {"start": v(26.93, -7.45) * mm, "end": v(26.9, -6.41) * mm});
            skArc(sketch, "E189.9.2", {"start": v(27.6, -7.55) * mm, "mid": v(27.27, -7.5) * mm, "end": v(26.93, -7.45) * mm});
            skLineSegment(sketch, "E189.9.3", {"start": v(25.31, -6.92) * mm, "end": v(25.95, -6.1) * mm});
            skArc(sketch, "E189.10.0", {"start": v(28.95, -6.58) * mm, "mid": v(28.46, -6.6) * mm, "end": v(27.96, -6.58) * mm});
            skLineSegment(sketch, "E189.10.1", {"start": v(29.3, -7.55) * mm, "end": v(28.95, -6.58) * mm});
            skArc(sketch, "E189.10.2", {"start": v(29.98, -7.45) * mm, "mid": v(29.64, -7.5) * mm, "end": v(29.3, -7.55) * mm});
            skLineSegment(sketch, "E189.10.3", {"start": v(27.6, -7.55) * mm, "end": v(27.96, -6.58) * mm});
            skArc(sketch, "E189.11.0", {"start": v(30.96, -6.1) * mm, "mid": v(30.5, -6.28) * mm, "end": v(30.02, -6.41) * mm});
            skLineSegment(sketch, "E189.11.1", {"start": v(31.6, -6.92) * mm, "end": v(30.96, -6.1) * mm});
            skArc(sketch, "E189.11.2", {"start": v(32.2, -6.6) * mm, "mid": v(31.9, -6.77) * mm, "end": v(31.6, -6.92) * mm});
            skLineSegment(sketch, "E189.11.3", {"start": v(29.98, -7.45) * mm, "end": v(30.02, -6.41) * mm});
            skArc(sketch, "E189.12.0", {"start": v(32.73, -5.03) * mm, "mid": v(32.33, -5.34) * mm, "end": v(31.92, -5.62) * mm});
            skLineSegment(sketch, "E189.12.1", {"start": v(33.58, -5.61) * mm, "end": v(32.73, -5.03) * mm});
            skArc(sketch, "E189.12.2", {"start": v(34.07, -5.13) * mm, "mid": v(33.83, -5.37) * mm, "end": v(33.58, -5.61) * mm});
            skLineSegment(sketch, "E189.12.3", {"start": v(32.2, -6.6) * mm, "end": v(31.92, -5.62) * mm});
            skArc(sketch, "E189.13.0", {"start": v(34.07, -3.47) * mm, "mid": v(33.8, -3.88) * mm, "end": v(33.49, -4.27) * mm});
            skLineSegment(sketch, "E189.13.1", {"start": v(35.06, -3.75) * mm, "end": v(34.07, -3.47) * mm});
            skArc(sketch, "E189.13.2", {"start": v(35.38, -3.14) * mm, "mid": v(35.23, -3.45) * mm, "end": v(35.06, -3.75) * mm});
            skLineSegment(sketch, "E189.13.3", {"start": v(34.07, -5.13) * mm, "end": v(33.49, -4.27) * mm});
            skArc(sketch, "E189.14.0", {"start": v(34.87, -1.56) * mm, "mid": v(34.73, -2.04) * mm, "end": v(34.56, -2.5) * mm});
            skLineSegment(sketch, "E189.14.1", {"start": v(35.9, -1.53) * mm, "end": v(34.87, -1.56) * mm});
            skArc(sketch, "E189.14.2", {"start": v(36, -0.85) * mm, "mid": v(35.96, -1.19) * mm, "end": v(35.9, -1.53) * mm});
            skLineSegment(sketch, "E189.14.3", {"start": v(35.38, -3.14) * mm, "end": v(34.56, -2.5) * mm});
            skArc(sketch, "E189.15.0", {"start": v(35.04, 0.5) * mm, "mid": v(35.06, 0) * mm, "end": v(35.04, -0.5) * mm});
            skLineSegment(sketch, "E189.15.1", {"start": v(36, 0.85) * mm, "end": v(35.04, 0.5) * mm});
            skArc(sketch, "E189.15.2", {"start": v(35.9, 1.53) * mm, "mid": v(35.96, 1.19) * mm, "end": v(36, 0.85) * mm});
            skLineSegment(sketch, "E189.15.3", {"start": v(36, -0.85) * mm, "end": v(35.04, -0.5) * mm});
            skArc(sketch, "E189.16.0", {"start": v(34.56, 2.5) * mm, "mid": v(34.73, 2.04) * mm, "end": v(34.87, 1.56) * mm});
            skLineSegment(sketch, "E189.16.1", {"start": v(35.38, 3.14) * mm, "end": v(34.56, 2.5) * mm});
            skArc(sketch, "E189.16.2", {"start": v(35.06, 3.75) * mm, "mid": v(35.23, 3.45) * mm, "end": v(35.38, 3.14) * mm});
            skLineSegment(sketch, "E189.16.3", {"start": v(35.9, 1.53) * mm, "end": v(34.87, 1.56) * mm});
            skArc(sketch, "E189.17.0", {"start": v(33.49, 4.27) * mm, "mid": v(33.8, 3.88) * mm, "end": v(34.07, 3.47) * mm});
            skLineSegment(sketch, "E189.17.1", {"start": v(34.07, 5.13) * mm, "end": v(33.49, 4.27) * mm});
            skArc(sketch, "E189.17.2", {"start": v(33.58, 5.61) * mm, "mid": v(33.83, 5.37) * mm, "end": v(34.07, 5.13) * mm});
            skLineSegment(sketch, "E189.17.3", {"start": v(35.06, 3.75) * mm, "end": v(34.07, 3.47) * mm});
            skArc(sketch, "E189.18.0", {"start": v(31.92, 5.62) * mm, "mid": v(32.33, 5.34) * mm, "end": v(32.73, 5.03) * mm});
            skLineSegment(sketch, "E189.18.1", {"start": v(32.2, 6.6) * mm, "end": v(31.92, 5.62) * mm});
            skArc(sketch, "E189.18.2", {"start": v(31.6, 6.92) * mm, "mid": v(31.9, 6.77) * mm, "end": v(32.2, 6.6) * mm});
            skLineSegment(sketch, "E189.18.3", {"start": v(33.58, 5.61) * mm, "end": v(32.73, 5.03) * mm});
            skArc(sketch, "E189.19.0", {"start": v(30.02, 6.41) * mm, "mid": v(30.5, 6.28) * mm, "end": v(30.96, 6.1) * mm});
            skLineSegment(sketch, "E189.19.1", {"start": v(29.98, 7.45) * mm, "end": v(30.02, 6.41) * mm});
            skArc(sketch, "E189.19.2", {"start": v(29.3, 7.55) * mm, "mid": v(29.64, 7.5) * mm, "end": v(29.98, 7.45) * mm});
            skLineSegment(sketch, "E189.19.3", {"start": v(31.6, 6.92) * mm, "end": v(30.96, 6.1) * mm});
            skSolve(sketch);
        }
        {
            var Q0;
            Q0 = qSketchRegion(id + "F92", true);
            extrude(context, id + "F93", {"entities" : qUnion([Q0]), "operationType" : NewBodyOperationType.ADD, "depth" : 3.2 * mm});
        }
        {
            var Q0;
            Q0=makeQuery(id+"F93.opExtrude","CAP_FACE",FACE,{"disambiguationData":[OSD([sQuery(id+"F92.wireOp",EDGE,"E184"),sQuery(id+"F92.wireOp",EDGE,"E185.0"),sQuery(id+"F92.wireOp",EDGE,"E186.0"),sQuery(id+"F92.wireOp",EDGE,"E187.0"),sQuery(id+"F92.wireOp",EDGE,"E188.0"),sQuery(id+"F92.wireOp",EDGE,"E189.1.0"),sQuery(id+"F92.wireOp",EDGE,"E189.1.1"),sQuery(id+"F92.wireOp",EDGE,"E189.1.2"),sQuery(id+"F92.wireOp",EDGE,"E189.1.3"),sQuery(id+"F92.wireOp",EDGE,"E189.2.0"),sQuery(id+"F92.wireOp",EDGE,"E189.2.1"),sQuery(id+"F92.wireOp",EDGE,"E189.2.2"),sQuery(id+"F92.wireOp",EDGE,"E189.2.3"),sQuery(id+"F92.wireOp",EDGE,"E189.3.0"),sQuery(id+"F92.wireOp",EDGE,"E189.3.1"),sQuery(id+"F92.wireOp",EDGE,"E189.3.2"),sQuery(id+"F92.wireOp",EDGE,"E189.3.3"),sQuery(id+"F92.wireOp",EDGE,"E189.4.0"),sQuery(id+"F92.wireOp",EDGE,"E189.4.1"),sQuery(id+"F92.wireOp",EDGE,"E189.4.2"),sQuery(id+"F92.wireOp",EDGE,"E189.4.3"),sQuery(id+"F92.wireOp",EDGE,"E189.5.0"),sQuery(id+"F92.wireOp",EDGE,"E189.5.1"),sQuery(id+"F92.wireOp",EDGE,"E189.5.2"),sQuery(id+"F92.wireOp",EDGE,"E189.5.3"),sQuery(id+"F92.wireOp",EDGE,"E189.6.0"),sQuery(id+"F92.wireOp",EDGE,"E189.6.1"),sQuery(id+"F92.wireOp",EDGE,"E189.6.2"),sQuery(id+"F92.wireOp",EDGE,"E189.6.3"),sQuery(id+"F92.wireOp",EDGE,"E189.7.0"),sQuery(id+"F92.wireOp",EDGE,"E189.7.1"),sQuery(id+"F92.wireOp",EDGE,"E189.7.2"),sQuery(id+"F92.wireOp",EDGE,"E189.7.3"),sQuery(id+"F92.wireOp",EDGE,"E189.8.0"),sQuery(id+"F92.wireOp",EDGE,"E189.8.1"),sQuery(id+"F92.wireOp",EDGE,"E189.8.2"),sQuery(id+"F92.wireOp",EDGE,"E189.8.3"),sQuery(id+"F92.wireOp",EDGE,"E189.9.0"),sQuery(id+"F92.wireOp",EDGE,"E189.9.1"),sQuery(id+"F92.wireOp",EDGE,"E189.9.2"),sQuery(id+"F92.wireOp",EDGE,"E189.9.3"),sQuery(id+"F92.wireOp",EDGE,"E189.10.0"),sQuery(id+"F92.wireOp",EDGE,"E189.10.1"),sQuery(id+"F92.wireOp",EDGE,"E189.10.2"),sQuery(id+"F92.wireOp",EDGE,"E189.10.3"),sQuery(id+"F92.wireOp",EDGE,"E189.11.0"),sQuery(id+"F92.wireOp",EDGE,"E189.11.1"),sQuery(id+"F92.wireOp",EDGE,"E189.11.2"),sQuery(id+"F92.wireOp",EDGE,"E189.11.3"),sQuery(id+"F92.wireOp",EDGE,"E189.12.0"),sQuery(id+"F92.wireOp",EDGE,"E189.12.1"),sQuery(id+"F92.wireOp",EDGE,"E189.12.2"),sQuery(id+"F92.wireOp",EDGE,"E189.12.3"),sQuery(id+"F92.wireOp",EDGE,"E189.13.0"),sQuery(id+"F92.wireOp",EDGE,"E189.13.1"),sQuery(id+"F92.wireOp",EDGE,"E189.13.2"),sQuery(id+"F92.wireOp",EDGE,"E189.13.3"),sQuery(id+"F92.wireOp",EDGE,"E189.14.0"),sQuery(id+"F92.wireOp",EDGE,"E189.14.1"),sQuery(id+"F92.wireOp",EDGE,"E189.14.2"),sQuery(id+"F92.wireOp",EDGE,"E189.14.3"),sQuery(id+"F92.wireOp",EDGE,"E189.15.0"),sQuery(id+"F92.wireOp",EDGE,"E189.15.1"),sQuery(id+"F92.wireOp",EDGE,"E189.15.2"),sQuery(id+"F92.wireOp",EDGE,"E189.15.3"),sQuery(id+"F92.wireOp",EDGE,"E189.16.0"),sQuery(id+"F92.wireOp",EDGE,"E189.16.1"),sQuery(id+"F92.wireOp",EDGE,"E189.16.2"),sQuery(id+"F92.wireOp",EDGE,"E189.16.3"),sQuery(id+"F92.wireOp",EDGE,"E189.17.0"),sQuery(id+"F92.wireOp",EDGE,"E189.17.1"),sQuery(id+"F92.wireOp",EDGE,"E189.17.2"),sQuery(id+"F92.wireOp",EDGE,"E189.17.3"),sQuery(id+"F92.wireOp",EDGE,"E189.18.0"),sQuery(id+"F92.wireOp",EDGE,"E189.18.1"),sQuery(id+"F92.wireOp",EDGE,"E189.18.2"),sQuery(id+"F92.wireOp",EDGE,"E189.18.3"),sQuery(id+"F92.wireOp",EDGE,"E189.19.0"),sQuery(id+"F92.wireOp",EDGE,"E189.19.1"),sQuery(id+"F92.wireOp",EDGE,"E189.19.2"),sQuery(id+"F92.wireOp",EDGE,"E189.19.3")])],"isStart":false});
            var sketch = newSketch(context, id + "F94", { "sketchPlane" : qUnion([Q0])});
            skCircle(sketch, "E190", {"center": v(28.46, 0) * mm, "radius": 5.65 * mm});
            skCircle(sketch, "E191", {"center": v(28.46, 0) * mm, "radius": 8.5 * mm});
            skSolve(sketch);
        }
        {
            var Q0;
            Q0 = qSketchRegion(id + "F94", true);
            extrude(context, id + "F95", {"entities" : qUnion([Q0]), "operationType" : NewBodyOperationType.ADD, "depth" : 1 * mm});
        }
        {
            var Q0;
            Q0=makeQuery(id+"F83.opExtrude","CAP_EDGE",EDGE,{"disambiguationData":[OSD([sQuery(id+"F82.wireOp",EDGE,"E153")])],"isStart":false});
            var Q1;
            Q1=makeQuery(id+"F89.opExtrude","CAP_EDGE",EDGE,{"disambiguationData":[OSD([sQuery(id+"F88.wireOp",EDGE,"E176.0")])],"isStart":true});
            var Q2;
            Q2=makeQuery(id+"F95.opExtrude","CAP_EDGE",EDGE,{"disambiguationData":[OSD([sQuery(id+"F94.wireOp",EDGE,"E191")])],"isStart":true});
            chamfer(context, id + "F96", {"entities" : qUnion([Q0, Q1, Q2]), "width" : 0.8 * mm, "tangentPropagation" : true});
        }
        {
            var Q0;
            Q0=makeQuery(id+"F95.opExtrude","CAP_EDGE",EDGE,{"disambiguationData":[OSD([sQuery(id+"F94.wireOp",EDGE,"E190")])],"isStart":false});
            var Q1;
            Q1=makeQuery(id+"F83.opExtrude","CAP_EDGE",EDGE,{"disambiguationData":[OSD([sQuery(id+"F82.wireOp",EDGE,"E154")])],"isStart":true});
            chamfer(context, id + "F97", {"entities" : qUnion([Q0, Q1]), "width" : 0.4 * mm, "tangentPropagation" : true});
        }
        {
            var Q0;
            Q0=makeQuery(id+"F87.opExtrude","CAP_EDGE",EDGE,{"disambiguationData":[OSD([sQuery(id+"F86.wireOp",EDGE,"E169")])],"isStart":true});
            chamfer(context, id + "F98", {"entities" : qUnion([Q0]), "width" : 1.7 * mm, "tangentPropagation" : true});
        }
        {
            var Q0;
            Q0=qCreatedBy(makeId("Top.planeOp"),FACE);
            var sketch = newSketch(context, id + "F99", { "sketchPlane" : qUnion([Q0])});
            skLineSegment(sketch, "E192.bottom", {"start": v(48.16, 45.07) * mm, "end": v(20.36, 45.07) * mm, "construction": true});
            skLineSegment(sketch, "E192.top", {"start": v(48.16, 29.17) * mm, "end": v(20.36, 29.17) * mm, "construction": true});
            skLineSegment(sketch, "E192.left", {"start": v(48.16, 45.07) * mm, "end": v(48.16, 29.17) * mm});
            skLineSegment(sketch, "E192.right", {"start": v(20.36, 45.07) * mm, "end": v(20.36, 29.17) * mm, "construction": true});
            skCircle(sketch, "E193", {"center": v(23.16, 42.27) * mm, "radius": 1.55 * mm});
            skCircle(sketch, "E194", {"center": v(45.36, 31.97) * mm, "radius": 1.55 * mm});
            skLineSegment(sketch, "E195", {"start": v(20.36, 45.07) * mm, "end": v(20.36, 40.42) * mm});
            skLineSegment(sketch, "E196", {"start": v(20.36, 40.42) * mm, "end": v(10.36, 40.42) * mm});
            skLineSegment(sketch, "E197", {"start": v(10.36, 40.42) * mm, "end": v(10.36, 33.82) * mm});
            skLineSegment(sketch, "E198", {"start": v(10.36, 33.82) * mm, "end": v(20.36, 33.82) * mm});
            skLineSegment(sketch, "E199", {"start": v(20.36, 33.82) * mm, "end": v(20.36, 29.17) * mm});
            skLineSegment(sketch, "E200", {"start": v(22.1, 29.17) * mm, "end": v(22.1, 26.07) * mm});
            skLineSegment(sketch, "E201", {"start": v(22.1, 26.07) * mm, "end": v(32.9, 26.07) * mm});
            skLineSegment(sketch, "E202", {"start": v(32.9, 26.07) * mm, "end": v(32.9, 29.17) * mm});
            skLineSegment(sketch, "E203", {"start": v(32.9, 29.17) * mm, "end": v(48.16, 29.17) * mm});
            skLineSegment(sketch, "E204", {"start": v(10.36, 37.12) * mm, "end": v(20.36, 37.12) * mm, "construction": true});
            skPoint(sketch, "E205.endSnap0", {"position": v(22.1, 27.62) * mm});
            skLineSegment(sketch, "E206", {"start": v(48.16, 45.07) * mm, "end": v(46.4, 45.07) * mm});
            skLineSegment(sketch, "E207", {"start": v(46.4, 45.07) * mm, "end": v(46.4, 52.23) * mm});
            skLineSegment(sketch, "E208", {"start": v(46.4, 52.23) * mm, "end": v(41.6, 52.23) * mm});
            skLineSegment(sketch, "E209", {"start": v(41.6, 52.23) * mm, "end": v(41.6, 46.77) * mm});
            skLineSegment(sketch, "E210", {"start": v(41.6, 46.77) * mm, "end": v(31.26, 46.77) * mm});
            skLineSegment(sketch, "E211", {"start": v(31.26, 46.77) * mm, "end": v(31.26, 45.07) * mm});
            skLineSegment(sketch, "E212", {"start": v(31.26, 45.07) * mm, "end": v(20.36, 45.07) * mm});
            skLineSegment(sketch, "E213", {"start": v(22.1, 29.17) * mm, "end": v(20.36, 29.17) * mm});
            skSolve(sketch);
        }
        {
            var Q0;
            Q0 = qSketchRegion(id + "F99", true);
            extrude(context, id + "F100", {"entities" : qUnion([Q0]), "depth" : 10.5 * mm});
        }
        {
            var Q0;
            Q0=makeQuery(id+"F100.opExtrude","SWEPT_EDGE",EDGE,{"disambiguationData":[OSD([sQuery(id+"F99.wireOp",EDGE,"E195"),sQuery(id+"F99.wireOp",EDGE,"E212")])]});
            var Q1;
            Q1=makeQuery(id+"F100.opExtrude","SWEPT_EDGE",EDGE,{"disambiguationData":[OSD([sQuery(id+"F99.wireOp",EDGE,"E192.left"),sQuery(id+"F99.wireOp",EDGE,"E203")])]});
            var Q2;
            Q2=makeQuery(id+"F100.opExtrude","SWEPT_EDGE",EDGE,{"disambiguationData":[OSD([sQuery(id+"F99.wireOp",EDGE,"E192.left"),sQuery(id+"F99.wireOp",EDGE,"E206")])]});
            var Q3;
            Q3=makeQuery(id+"F100.opExtrude","SWEPT_EDGE",EDGE,{"disambiguationData":[OSD([sQuery(id+"F99.wireOp",EDGE,"E201"),sQuery(id+"F99.wireOp",EDGE,"E202")])]});
            var Q4;
            Q4=makeQuery(id+"F100.opExtrude","SWEPT_EDGE",EDGE,{"disambiguationData":[OSD([sQuery(id+"F99.wireOp",EDGE,"E199"),sQuery(id+"F99.wireOp",EDGE,"E213")])]});
            var Q5;
            Q5=makeQuery(id+"F100.opExtrude","SWEPT_EDGE",EDGE,{"disambiguationData":[OSD([sQuery(id+"F99.wireOp",EDGE,"E210"),sQuery(id+"F99.wireOp",EDGE,"E211")])]});
            var Q6;
            Q6=makeQuery(id+"F100.opExtrude","SWEPT_EDGE",EDGE,{"disambiguationData":[OSD([sQuery(id+"F99.wireOp",EDGE,"E208"),sQuery(id+"F99.wireOp",EDGE,"E209")])]});
            var Q7;
            Q7=makeQuery(id+"F100.opExtrude","SWEPT_EDGE",EDGE,{"disambiguationData":[OSD([sQuery(id+"F99.wireOp",EDGE,"E207"),sQuery(id+"F99.wireOp",EDGE,"E208")])]});
            fillet(context, id + "F101", {"entities" : qUnion([Q0, Q1, Q2, Q3, Q4, Q5, Q6, Q7]), "radius" : 2.4 * mm, "tangentPropagation" : true, "allowEdgeOverflow" : false});
        }
    });
